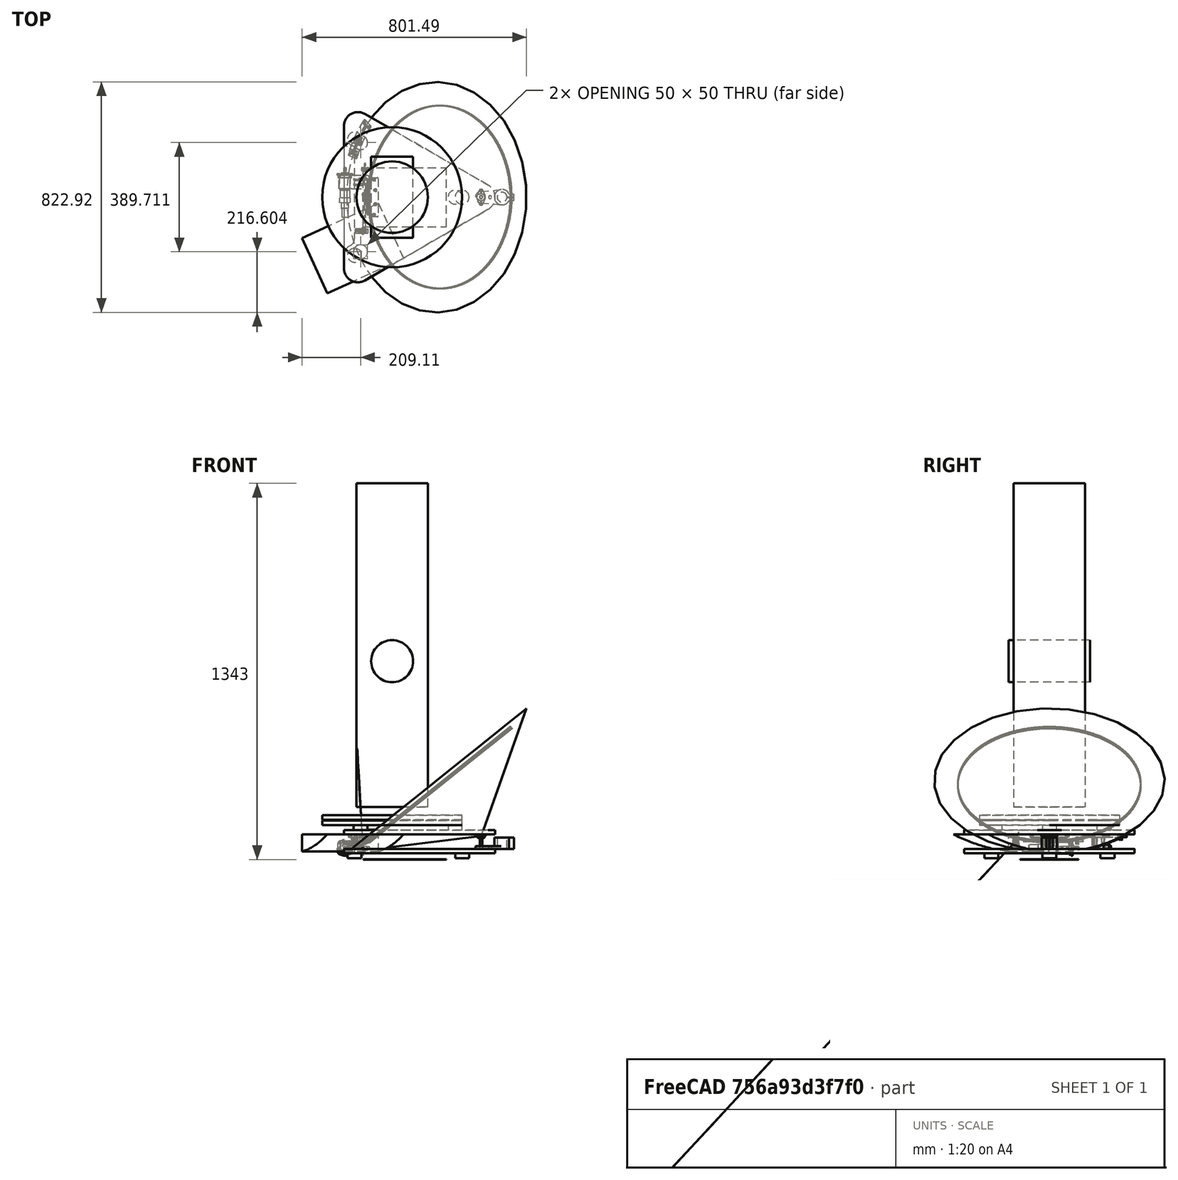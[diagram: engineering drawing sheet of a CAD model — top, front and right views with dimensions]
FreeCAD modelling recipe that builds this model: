
FCSTD DOCUMENT  (FreeCAD 2022.111R30764 (Git))
Label: DobsonEQPlatformGearBearing
License: All rights reserved
LicenseURL: http://en.wikipedia.org/wiki/All_rights_reserved
objects: Sketcher::SketchExport×38, PartDesign::Pad×30, Sketcher::SketchObject×28, PartDesign::Fillet×20, PartDesign::SubShapeBinder×17, PartDesign::Pocket×15, PartDesign::Body×14, PartDesign::Chamfer×13, Part::SubShapeBinder×10, TechDraw::DrawViewDimension×8, PartDesign::Plane×7, PartDesign::ShapeBinder×6, Part::FeaturePython×4, Part::Mirroring×4, Part::Cylinder×3, PartDesign::Revolution×3, TechDraw::DrawProjGroup×3, TechDraw::DrawProjGroupItem×3, TechDraw::DrawSVGTemplate×2, Part::Box×2, +7 more types
note: 381 computed .brp shape members not serialized (recipe doc carries the construction recipe); baked Part::Feature solids carry a one-line shape summary decoded from their .brp

FEATURE [Part::Cylinder] Cylinder  label="Newton"
  Angle = 360
  AttacherType = Attacher::AttachEngine3D
  FirstAngle = 0
  Height = 1155
  Placement = pos=(0,0,83) rot=(0,0,1;0rad)
  Radius = 127.5
  SecondAngle = 0
  TreeRank = 0
FEATURE [Part::Cylinder] Cylinder003
  Angle = 360
  AttacherType = Attacher::AttachEngine3D
  FirstAngle = 0
  Height = 290
  Placement = pos=(0,-145,603) rot=(-1,0,0;1.5708rad)
  Radius = 75
  SecondAngle = 0
  TreeRank = 0
FEATURE [Spreadsheet::Sheet] Spreadsheet  label="measures"
  PythonMode = false
  ShowCells = 0
  TreeRank = 0
  cells = A1=Foot of Elipse; D1=Newton; A2=Drill sIze; B2(FootDrillSize)=6.2; D2=Height; E2=1155; A3=Nut size radius; B3(elipsefeednutsizeradius)=11.25; D3=Center of Gravitiy; E3(CoG)==315 + 60; A4=Nut pcket size; B4(elipsefeednutpocket)=4.8; A5=Foot size; B5(elipsefootSize)=35; D5=Radius; E5=127.5; A6=Foot thickness; B6(elipsefootthickness)=10; D6=Over ground; E6=83; A7=Roundness; B7(elipsefootroundness)=4; A9=Elipse; D9=MidPart over ground; E9=603; A10=Elipse position angle; B10(ElipsePositionAngle)=36; D10=Midpart radius ; E10=75; A11=Elipse max deg; B11(ElipseMaxDeg)=17.5; D11=Midpart height; E11=290; A12=Elipse tickness; B12(ElipseThickness)=7.2; A13=Distance Center; B13(ElipseDistanceCenterP)=480; A14=Stopper max deg; B14(elipsestoppermaxdeg)=1; A15=StopperHeight; B15(ElipseStopperHeight)=10; A16=Screw head diameter; B16(elipsescrewheaddia)=10; A17=Screw hole diameter; B17(elipsescrewholedia)=6; A18=Screw distance; B18(elipsescrewdistance)=10; A20=Rockerbox; A21=Diameter; B21(RockerboxDiameter)=500; A22=FeedDiameter; B22(RockerboxFeedDiameter)=50; A23=Teflonpad gap; B23(teflonpadgap)=3; A24=Thickness; B24(Rockerboxthickness)=16; A25=MinFeedHight; B25(RockerboxMinFeedHight)=18; A26=Cone; A27=Midpoint to south bearing; B27(MidpointToSouthBearing)=300; A28=Pol Angle deg; B28(PolarisAngle)=51.3; A29=Cone Angle; B29(ConeAngle)=58.3; A30=South Bearing height; B30(southbearingheigt)=6.5; C30=for mid point of bearing; A31=South Bearing axis diameter; B31(southbearingaxisdia)=10; A32=Plattform; A33=Thickness; B33(plattformthickness)=15; A34=Platform gap; B34(platformgap)=52; A35=Midpoint to north end top; B35(platformmidpointnorth)=172; A36=Midpoint to north end bottom; B36(platformmidpointnorthbottom)=360; A37=Roller X from midpoint; B37(rollerXmidpoint)=130; A38=Roller Y from midpoint; B38(rollerYmidpoint)=190
FEATURE [Sketcher::SketchObject] Sketch  label="MasterXZ"
  FullyConstrained = true
  MapMode = 5
  Placement = pos=(0,0,0) rot=(1,0,0;1.5708rad)
  Support = -> [XZ_Plane]
  TreeRank = 11
  expr: Constraints[12] = <<measures>>.CoG
  expr: Constraints[3] = <<measures>>.PolarisAngle
  expr: Constraints[4] = <<measures>>.ConeAngle
  expr: Constraints[5] = -<<measures>>.plattformthickness - <<measures>>.southbearingheigt
  expr: Constraints[8] = <<measures>>.ElipseDistanceCenterP
  sketch-geometry (5):
    g0: LineSegment StartX=317.656 StartY=-21.5 StartZ=0 EndX=158.769 EndY=176.823 EndZ=0
    g1: LineSegment StartX=158.769 StartY=176.823 StartZ=0 EndX=-162.344 EndY=-80.4366 EndZ=0
    g2: LineSegment StartX=-162.344 StartY=-80.4366 StartZ=0 EndX=317.656 EndY=-21.5 EndZ=0
    g3: LineSegment [constr] StartX=158.769 StartY=176.823 StartZ=0 EndX=-245.062 EndY=680.887 EndZ=0
    g4: LineSegment [constr] StartX=0 StartY=0 StartZ=0 EndX=0 EndY=375 EndZ=0
  constraints (14):
    c: Coincident(g0,g1)
    c: Coincident(g1,g2)
    c: Coincident(g2,g0)
    c: Angle(g0,g-1) = 0.895354
    c: Angle(g0,g2) = 1.01753
    c: DistanceY(g0) = -21.5
    c: Perpendicular(g0,g1)
    c: Tangent(g3,g0) = -1.5708
    c: DistanceX(g1,g0) = 480
    c: Distance(g3,g0) = 900
    c: Coincident(g4,g-1)
    c: Vertical(g4)
    c: DistanceY(g4,g4) = 375
    c: PointOnObject(g4,g3)
FEATURE [Sketcher::SketchObject] Sketch001  label="MasterXY"
  ExternalGeometry = -> [Sketch]
  FullyConstrained = true
  MapMode = 5
  Support = -> [XY_Plane]
  TreeRank = 12
  expr: Constraints[35] = <<measures>>.southbearingaxisdia
  expr: Constraints[62] = <<measures>>.RockerboxDiameter - <<measures>>.RockerboxFeedDiameter
  expr: Constraints[63] = <<measures>>.RockerboxDiameter
  expr: Constraints[72] = <<measures>>.RockerboxFeedDiameter
  sketch-geometry (31):
    g0: Circle CenterX=317.656 CenterY=4.1e-15 CenterZ=0 NormalX=0 NormalY=0 NormalZ=1 AngleXU=0 Radius=5
    g1: Circle CenterX=317.656 CenterY=0 CenterZ=0 NormalX=0 NormalY=0 NormalZ=1 AngleXU=0 Radius=10.95
    g2: LineSegment [constr] StartX=330.656 StartY=13 StartZ=0 EndX=304.656 EndY=13 EndZ=0
    g3: LineSegment [constr] StartX=304.656 StartY=13 StartZ=0 EndX=304.656 EndY=-13 EndZ=0
    g4: LineSegment [constr] StartX=304.656 StartY=-13 StartZ=0 EndX=304.656 EndY=13 EndZ=0
    g5: LineSegment [constr] StartX=304.656 StartY=13 StartZ=0 EndX=330.656 EndY=13 EndZ=0
    g6: Circle [constr] CenterX=317.656 CenterY=4.8e-15 CenterZ=0 NormalX=0 NormalY=0 NormalZ=1 AngleXU=0 Radius=18.3848
    g7: Circle CenterX=304.656 CenterY=-13 CenterZ=0 NormalX=0 NormalY=0 NormalZ=1 AngleXU=0 Radius=2.65
    g8: Circle CenterX=304.656 CenterY=13 CenterZ=0 NormalX=0 NormalY=0 NormalZ=1 AngleXU=0 Radius=2.65
    g9: Circle CenterX=304.656 CenterY=13 CenterZ=0 NormalX=0 NormalY=0 NormalZ=1 AngleXU=0 Radius=2.65
    g10: Circle CenterX=330.656 CenterY=13 CenterZ=0 NormalX=0 NormalY=0 NormalZ=1 AngleXU=0 Radius=2.65
    g11: LineSegment StartX=298.656 StartY=-13 StartZ=0 EndX=298.656 EndY=13 EndZ=0
    g12: ArcOfCircle CenterX=304.656 CenterY=13 CenterZ=0 NormalX=0 NormalY=0 NormalZ=1 AngleXU=0 Radius=6 StartAngle=1.5708 EndAngle=3.14159
    g13: LineSegment StartX=304.656 StartY=19 StartZ=0 EndX=330.656 EndY=19 EndZ=0
    g14: ArcOfCircle CenterX=330.656 CenterY=13 CenterZ=0 NormalX=0 NormalY=0 NormalZ=1 AngleXU=0 Radius=6 StartAngle=2e-16 EndAngle=1.5708
    g15: LineSegment StartX=336.656 StartY=13 StartZ=0 EndX=336.656 EndY=-13 EndZ=0
    g16: ArcOfCircle CenterX=330.656 CenterY=-13 CenterZ=0 NormalX=0 NormalY=0 NormalZ=1 AngleXU=0 Radius=6 StartAngle=4.71239 EndAngle=6.28319
    g17: LineSegment StartX=330.656 StartY=-19 StartZ=0 EndX=304.656 EndY=-19 EndZ=0
    g18: ArcOfCircle CenterX=304.656 CenterY=-13 CenterZ=0 NormalX=0 NormalY=0 NormalZ=1 AngleXU=0 Radius=6 StartAngle=3.14159 EndAngle=4.71239
    g19: LineSegment [constr] StartX=330.656 StartY=13 StartZ=0 EndX=330.656 EndY=-13 EndZ=0
    g20: LineSegment [constr] StartX=330.656 StartY=-13 StartZ=0 EndX=304.656 EndY=-13 EndZ=0
    g21: Circle CenterX=330.656 CenterY=-13 CenterZ=0 NormalX=0 NormalY=0 NormalZ=1 AngleXU=0 Radius=2.65
    g22: Circle CenterX=0 CenterY=0 CenterZ=0 NormalX=0 NormalY=0 NormalZ=1 AngleXU=0 Radius=250
    g23: LineSegment StartX=-112.5 StartY=194.856 StartZ=0 EndX=-112.5 EndY=-194.856 EndZ=0
    g24: LineSegment StartX=-112.5 StartY=-194.856 StartZ=0 EndX=225 EndY=0 EndZ=0
    g25: LineSegment StartX=225 StartY=0 StartZ=0 EndX=-112.5 EndY=194.856 EndZ=0
    g26: Circle [constr] CenterX=0 CenterY=0 CenterZ=0 NormalX=0 NormalY=0 NormalZ=1 AngleXU=0 Radius=225
    g27: Circle CenterX=-112.5 CenterY=194.856 CenterZ=0 NormalX=0 NormalY=0 NormalZ=1 AngleXU=0 Radius=25
    g28: Circle CenterX=-112.5 CenterY=-194.856 CenterZ=0 NormalX=0 NormalY=0 NormalZ=1 AngleXU=0 Radius=7.1e-15
    g29: Circle CenterX=-112.5 CenterY=-194.856 CenterZ=0 NormalX=0 NormalY=0 NormalZ=1 AngleXU=0 Radius=25
    g30: Circle CenterX=225 CenterY=0 CenterZ=0 NormalX=0 NormalY=0 NormalZ=1 AngleXU=0 Radius=25
  constraints (73):
    c: Coincident(g0,g-3)
    c: Coincident(g1,g-3)
    c: Coincident(g2,g3)
    c: Coincident(g3,g4)
    c: Coincident(g4,g5)
    c: Coincident(g5,g2)
    c: Equal(g2,g3)
    c: Equal(g2,g4)
    c: Equal(g2,g5)
    c: PointOnObject(g2,g6)
    c: PointOnObject(g3,g6)
    c: PointOnObject(g5,g6)
    c: Coincident(g6,g-3)
    c: Coincident(g7,g3)
    c: Coincident(g8,g2)
    c: Coincident(g9,g4)
    c: Coincident(g10,g2)
    c: Tangent(g11,g12) = 1.5708
    c: Tangent(g12,g13) = 1.5708
    c: Tangent(g13,g14) = 1.5708
    c: Tangent(g14,g15) = 1.5708
    c: Tangent(g15,g16) = 1.5708
    c: Tangent(g16,g17) = 1.5708
    c: Tangent(g17,g18) = 1.5708
    c: Equal(g17,g13)
    c: Equal(g15,g11)
    c: Radius(g18) = 6
    c: Equal(g18,g16)
    c: Equal(g18,g12)
    c: Equal(g18,g14)
    c: Tangent(g11,g18) = 1.5708
    c: Equal(g7,g8)
    c: Equal(g8,g9)
    c: Equal(g9,g10)
    c: Diameter(g7) = 5.3
    c: Diameter(g0) = 10
    c: Diameter(g1) = 21.9
    c: Equal(g11,g17)
    c: Symmetric(g14,g15,g-1)
    c: Horizontal(g13)
    c: DistanceY(g16,g13) = 38
    c: DistanceY(g7,g8) = 26
    c: Vertical(g3)
    c: Horizontal(g2)
    c: Coincident(g19,g14)
    c: PointOnObject(g19,g6)
    c: Vertical(g19)
    c: Coincident(g20,g19)
    c: Coincident(g20,g7)
    c: Horizontal(g20)
    c: Coincident(g21,g16)
    c: Equal(g21,g10)
    c: Coincident(g23,g24)
    c: Coincident(g24,g25)
    c: Coincident(g25,g23)
    c: Equal(g23,g24)
    c: Equal(g23,g25)
    c: PointOnObject(g23,g26)
    c: PointOnObject(g24,g26)
    c: PointOnObject(g25,g26)
    c: Coincident(g26,g22)
    c: Vertical(g23)
    c: Diameter(g26) = 450
    c: Diameter(g22) = 500
    c: Coincident(g22,g-1)
    c: Coincident(g27,g23)
    c: Coincident(g28,g23)
    c: Tangent(g28,g26)
    c: Coincident(g29,g23)
    c: Coincident(g30,g24)
    c: Equal(g30,g27)
    c: Equal(g27,g29)
    c: Diameter(g29) = 50
FEATURE [PartDesign::ShapeBinder] ShapeBinder
  Support = -> [Sketch]
  TraceSupport = false
  TreeRank = 24
FEATURE [Part::SubShapeBinder] Import  label="Import(MasterXZ)"
  BindCopyOnChange = 0
  BindMode = 0
  ClaimChildren = false
  Context = -> Body001 [Import.]
  FillStyle = 0
  Fuse = false
  MakeFace = false
  PartialLoad = false
  Relative = true
  Support = -> [Body[Sketch.]]
  TreeRank = 26
  _Version = 8
FEATURE [Sketcher::SketchObject] Sketch002  label="ConeSkatch"
  ExternalGeometry = -> [ShapeBinder,Import]
  FullyConstrained = true
  MapMode = 5
  Placement = pos=(0,0,0) rot=(1,0,0;1.5708rad)
  Support = -> [XZ_Plane001]
  TreeRank = 27
  sketch-geometry (3):
    g0: LineSegment StartX=317.656 StartY=-21.5 StartZ=0 EndX=158.769 EndY=176.823 EndZ=0
    g1: LineSegment StartX=158.769 StartY=176.823 StartZ=0 EndX=-162.344 EndY=-80.4366 EndZ=0
    g2: LineSegment StartX=-162.344 StartY=-80.4366 StartZ=0 EndX=317.656 EndY=-21.5 EndZ=0
  constraints (6):
    c: Coincident(g0,g-3)
    c: Coincident(g0,g-4)
    c: Coincident(g0,g1)
    c: Coincident(g1,g-5)
    c: Coincident(g1,g2)
    c: Coincident(g2,g0)
FEATURE [PartDesign::Revolution] Revolution
  AddSubType = 0
  Angle = 360
  Axis = (-0.625243,-2e-16,0.78043)
  Base = (317.656,4.8e-15,-21.5)
  ClaimChildren = false
  Fit = 0
  FitJoin = 0
  InnerFit = 0
  InnerFitJoin = 0
  NewSolid = false
  Placement = pos=(0,0,0) rot=(1,0,0;1.5708rad)
  Profile = -> Sketch002
  ReferenceAxis = -> ShapeBinder [Edge2]
  Suppress = false
  TreeRank = 28
  _ProfileBasedVersion = 1
FEATURE [PartDesign::Body] Body001  label="Cone"
  AutoGroupSolids = false
  ExportMode = 0
  Group = -> [ShapeBinder,Import,Sketch002,Revolution]
  Origin = -> Origin001
  Tip = -> Revolution
  TreeRank = 23
  _ExportChildren = -> [ShapeBinder,Import,Revolution]
  _GroupVersion = 1
FEATURE [PartDesign::ShapeBinder] ShapeBinder001
  Support = -> [Sketch001]
  TraceSupport = false
  TreeRank = 39
FEATURE [Part::SubShapeBinder] Import001  label="Import001(MasterXY)"
  BindCopyOnChange = 0
  BindMode = 0
  ClaimChildren = false
  Context = -> Body002 [Import001.]
  FillStyle = 0
  Fuse = false
  MakeFace = false
  PartialLoad = false
  Relative = true
  Support = -> [Body[Sketch001.]]
  TreeRank = 41
  _Version = 8
FEATURE [Sketcher::SketchObject] Sketch004  label="PlatformTop"
  ExternalGeometry = -> [Sketch001]
  FullyConstrained = true
  MapMode = 5
  Support = -> [XY_Plane]
  TreeRank = 53
  expr: Constraints[15] = <<measures>>.platformmidpointnorth
  sketch-geometry (7):
    g0: LineSegment StartX=342.656 StartY=43.3013 StartZ=0 EndX=-97 EndY=297.137 EndZ=0
    g1: ArcOfCircle CenterX=-122 CenterY=253.836 CenterZ=0 NormalX=0 NormalY=0 NormalZ=1 AngleXU=0 Radius=50 StartAngle=1.0472 EndAngle=3.14159
    g2: LineSegment StartX=-172 StartY=253.836 StartZ=0 EndX=-172 EndY=-253.836 EndZ=0
    g3: ArcOfCircle CenterX=-122 CenterY=-253.836 CenterZ=0 NormalX=0 NormalY=0 NormalZ=1 AngleXU=0 Radius=50 StartAngle=3.14159 EndAngle=5.23599
    g4: LineSegment StartX=-97 StartY=-297.137 StartZ=0 EndX=342.656 EndY=-43.3013 EndZ=0
    g5: ArcOfCircle CenterX=317.656 CenterY=2e-16 CenterZ=0 NormalX=0 NormalY=0 NormalZ=1 AngleXU=0 Radius=50 StartAngle=5.23599 EndAngle=7.33038
    g6: LineSegment [constr] StartX=-172 StartY=0 StartZ=0 EndX=367.656 EndY=0 EndZ=0
  constraints (17):
    c: Tangent(g0,g1) = -1.5708
    c: Tangent(g1,g2) = -1.5708
    c: Tangent(g2,g3) = -1.5708
    c: Tangent(g3,g4) = -1.5708
    c: Tangent(g4,g5) = -1.5708
    c: Tangent(g5,g0) = -1.5708
    c: Symmetric(g0,g4,g-1)
    c: Symmetric(g1,g2,g-1)
    c: Radius(g5) = 50
    c: Radius(g1) = 50
    c: Equal(g4,g2)
    c: PointOnObject(g6,g5)
    c: Horizontal(g6)
    c: PointOnObject(g6,g2)
    c: DistanceX(g-3,g6) = 50
    c: DistanceX(g6,g-1) = 172
    c: PointOnObject(g6,g-1)
FEATURE [PartDesign::Body] Body  label="MasterBody"
  AutoGroupSolids = false
  ExportMode = 0
  Group = -> [Sketch,Sketch001,Sketch004]
  Origin = -> Origin
  TreeRank = 22
  _ExportChildren = -> [Sketch,Sketch001,Sketch004]
  _GroupVersion = 1
FEATURE [PartDesign::ShapeBinder] ShapeBinder002
  Support = -> [Sketch004,Sketch001]
  TraceSupport = false
  TreeRank = 100
FEATURE [Part::SubShapeBinder] Import002  label="Import002(PlatformTop)"
  BindCopyOnChange = 0
  BindMode = 0
  ClaimChildren = false
  Context = -> Body003 [Import002.]
  FillStyle = 0
  Fuse = false
  MakeFace = false
  PartialLoad = false
  Relative = true
  Support = -> [Sketch004]
  TreeRank = 102
  _Version = 8
FEATURE [Sketcher::SketchObject] Sketch005  label="plattop"
  ExternalGeometry = -> [Import002]
  FullyConstrained = true
  MapMode = 5
  Support = -> [XY_Plane003]
  TreeRank = 101
FEATURE [PartDesign::Pad] Pad006
  AddSubType = 0
  CheckUpToFaceLimits = true
  ClaimChildren = false
  Direction = (0,0,1)
  Fit = 0
  FitJoin = 0
  InnerFit = 0
  InnerFitJoin = 0
  InnerTaperAngle = 0
  InnerTaperAngleRev = 0
  Length = 15
  Length2 = 100
  Linearize = true
  NewSolid = false
  Profile = -> Sketch005
  Reversed = true
  Suppress = false
  TreeRank = 103
  Type = 0
  _ProfileBasedVersion = 1
  expr: Length = <<measures>>.plattformthickness
FEATURE [Part::SubShapeBinder] Import003  label="Import003(MasterXY)"
  BindCopyOnChange = 0
  BindMode = 0
  ClaimChildren = false
  Context = -> Body003 [Import003.]
  FillStyle = 0
  Fuse = false
  MakeFace = false
  PartialLoad = false
  Relative = true
  Support = -> [Sketch001]
  TreeRank = 105
  _Version = 8
FEATURE [PartDesign::ShapeBinder] ShapeBinder003
  Support = -> [Sketch004,Sketch001]
  TraceSupport = false
  TreeRank = 118
FEATURE [PartDesign::ShapeBinder] ShapeBinder004
  Support = -> [Sketch001]
  TraceSupport = false
  TreeRank = 120
FEATURE [PartDesign::SubShapeBinder] Binder001  label="Binder001(Pad037)"
  BindCopyOnChange = 0
  BindMode = 0
  ClaimChildren = false
  Context = -> Body004 [Binder001.]
  FillStyle = 0
  Fuse = false
  MakeFace = true
  PartialLoad = false
  Relative = true
  Support = -> [Pad037[Face41]]
  TreeRank = 176
  _Version = 8
FEATURE [PartDesign::SubShapeBinder] Binder  label="Binder(Revolution)"
  BindCopyOnChange = 0
  BindMode = 0
  ClaimChildren = false
  Context = -> Body008 [Binder.]
  FillStyle = 0
  Fuse = false
  MakeFace = true
  PartialLoad = false
  Relative = true
  Support = -> [Body001[Revolution.Edge1]]
  TreeRank = 290
  _Version = 8
FEATURE [PartDesign::SubShapeBinder] Binder004  label="Binder004(Fillet009)"
  BindCopyOnChange = 0
  BindMode = 0
  ClaimChildren = false
  Context = -> Body008 [Binder004.]
  FillStyle = 0
  Fuse = false
  MakeFace = true
  PartialLoad = false
  Relative = true
  Support = -> [Body003[Fillet009.Face33]]
  TreeRank = 318
  _Version = 8
FEATURE [Part::SubShapeBinder] Import009  label="Import009(Sketch011)"
  BindCopyOnChange = 0
  BindMode = 0
  ClaimChildren = false
  Context = -> Body006 [Import009.]
  FillStyle = 0
  Fuse = false
  MakeFace = false
  PartialLoad = false
  Relative = true
  Support = -> [Sketch011]
  TreeRank = 323
  _Version = 8
FEATURE [Part::SubShapeBinder] Import011  label="Import011(Fillet006)"
  BindCopyOnChange = 0
  BindMode = 0
  ClaimChildren = false
  Context = -> Body009 [Import011.]
  FillStyle = 0
  Fuse = false
  MakeFace = false
  PartialLoad = false
  Relative = true
  Support = -> [Body006[Fillet006.]]
  TreeRank = 357
  _Version = 8
FEATURE [PartDesign::Plane] DatumPlane002
  Length = 440.135
  MapMode = 5
  MinimumLength = 10
  MinimumWidth = 10
  Placement = pos=(-185.022,-83.9977,0) rot=(0.739203,-0.476224,-0.476224;1.86848rad)
  ResizeMode = 0
  Support = -> [Import011]
  TreeRank = 356
  Width = 75.6692
FEATURE [PartDesign::SubShapeBinder] Binder006  label="Binder006(Revolution)"
  BindCopyOnChange = 0
  BindMode = 0
  ClaimChildren = false
  Context = -> Body009 [Binder006.]
  FillStyle = 0
  Fuse = false
  MakeFace = true
  PartialLoad = false
  Relative = true
  Support = -> [Body001[Revolution.Edge1]]
  TreeRank = 359
  _Version = 8
FEATURE [Part::SubShapeBinder] Import012  label="Import012(MasterXZ)"
  BindCopyOnChange = 0
  BindMode = 0
  ClaimChildren = false
  Context = -> Body009 [Import012.]
  FillStyle = 0
  Fuse = false
  MakeFace = false
  PartialLoad = false
  Relative = true
  Support = -> [Body[Sketch.]]
  TreeRank = 360
  _Version = 8
FEATURE [Sketcher::SketchObject] Sketch013
  ExternalGeometry = -> [Binder006,Import012]
  FullyConstrained = true
  MapMode = 5
  Placement = pos=(-185.022,-83.9977,0) rot=(0.739203,-0.476224,-0.476224;1.86848rad)
  Support = -> [DatumPlane002]
  TreeRank = 358
  expr: Constraints[13] = <<measures>>.plattformthickness
  sketch-geometry (7):
    g0: ArcOfEllipse CenterX=65.6324 CenterY=176.823 CenterZ=0 NormalX=0 NormalY=0 NormalZ=1 MajorRadius=411.456 MinorRadius=234.25 AngleXU=0.319813 StartAngle=4.36015 EndAngle=4.91482
    g1: LineSegment [constr] StartX=456.226 StartY=306.181 StartZ=0 EndX=-324.961 EndY=47.4662 EndZ=0
    g2: LineSegment [constr] StartX=-8.01316 StartY=399.196 StartZ=0 EndX=139.278 EndY=-45.5488 EndZ=0
    g3: GeomPoint [constr] X=386.745 Y=283.17 Z=0
    g4: GeomPoint [constr] X=-255.481 Y=70.4767 Z=0
    g5: LineSegment StartX=-5.68e-14 StartY=-76.5242 StartZ=0 EndX=0 EndY=-15 EndZ=0
    g6: LineSegment StartX=0 StartY=-15 StartZ=0 EndX=216.305 EndY=-15 EndZ=0
  constraints (11):
    c: InternalAlignment(g1-g4 -> g0) x4
    c: Coincident(g0,g-4)
    c: PointOnObject(g0,g-2)
    c: Coincident(g5,g0)
    c: Coincident(g6,g0)
    c: PointOnObject(g2,g-3)
    c: Coincident(g5,g6)
    c: PointOnObject(g5,g-2)
    c: Tangent(g0,g-3) = -1.5708
    c: Horizontal(g6)
    c: DistanceY(g5,g-1) = 15
FEATURE [PartDesign::Pad] Pad031
  AddSubType = 0
  AlongSketchNormal = false
  CheckUpToFaceLimits = true
  ClaimChildren = false
  Direction = (-0.910558,-0.413382,0)
  Fit = 0
  FitJoin = 0
  InnerFit = 0
  InnerFitJoin = 0
  InnerTaperAngle = 0
  InnerTaperAngleRev = 0
  Length = 300
  Length2 = 100
  Linearize = true
  Midplane = true
  NewSolid = false
  Placement = pos=(-185.022,-83.9977,0) rot=(0.739203,-0.476224,-0.476224;1.86848rad)
  Profile = -> Sketch013
  Refine = true
  Suppress = false
  TreeRank = 361
  Type = 0
  _ProfileBasedVersion = 1
FEATURE [PartDesign::Body] Body009  label="CutterElipse"
  AutoGroupSolids = false
  ExportMode = 0
  Group = -> [DatumPlane002,Import011,Sketch013,Binder006,Import012,Pad031]
  Origin = -> Origin009
  Tip = -> Pad031
  TreeRank = 355
  _ExportChildren = -> [DatumPlane002,Import011,Binder006,Import012,Pad031]
  _GroupVersion = 1
FEATURE [PartDesign::SubShapeBinder] Binder007  label="Binder007(Pad031)"
  BindCopyOnChange = 0
  BindMode = 0
  ClaimChildren = false
  Context = -> Body008 [Binder007.]
  FillStyle = 0
  Fuse = false
  MakeFace = true
  PartialLoad = false
  Relative = true
  Support = -> [Body009[Pad031.]]
  TreeRank = 362
  _Version = 8
FEATURE [PartDesign::SubShapeBinder] Reference  label="Reference(Pad026)"
  BindCopyOnChange = 0
  BindMode = 0
  ClaimChildren = false
  Context = -> Body008 [Reference.]
  FillStyle = 0
  Fuse = false
  MakeFace = true
  PartialLoad = false
  Relative = true
  Support = -> [Pad026]
  TreeRank = 364
  _Version = 8
FEATURE [PartDesign::SubShapeBinder] Reference001  label="Reference001(*Pad031)"
  BindCopyOnChange = 0
  BindMode = 0
  ClaimChildren = false
  Context = -> Body008 [Reference001.]
  FillStyle = 0
  Fuse = false
  MakeFace = true
  PartialLoad = false
  Relative = true
  Support = -> [Binder007]
  TreeRank = 365
  _Version = 8
FEATURE [PartDesign::SubShapeBinder] Binder008  label="Binder008(Chamfer003)"
  BindCopyOnChange = 0
  BindMode = 0
  ClaimChildren = false
  Context = -> Body008 [Binder008.]
  FillStyle = 0
  Fuse = false
  MakeFace = true
  PartialLoad = false
  Relative = true
  Support = -> [Chamfer003[Edge12]]
  TreeRank = 380
  _Version = 8
FEATURE [TechDraw::DrawSVGTemplate] Template
  EditableTexts = AUTHOR_NAME=Sebastian Förster; DN=DN; DRAWING_TITLE=EQ Plattform; FC-DATE=28/01/2022; FC-REV=REV A; FC-SC=1:1; FC-SH=1 / 1; FC-SI=A0; FreeCAD_DRAWING=Drawing for wood cutting and drilling; PN=PN
  Height = 841
  Orientation = 1
  TreeRank = 382
  Width = 1189
FEATURE [PartDesign::SubShapeBinder] Binder009  label="Binder009(Pad025)"
  BindCopyOnChange = 0
  BindMode = 0
  ClaimChildren = false
  Context = -> Body006 [Binder009.]
  FillStyle = 0
  Fuse = false
  MakeFace = true
  PartialLoad = false
  Relative = true
  Support = -> [Pad025[Face4]]
  TreeRank = 389
  _Version = 8
FEATURE [PartDesign::Plane] DatumPlane
  AttachmentOffset = pos=(0,0,10) rot=(0,0,1;0rad)
  Length = 131.581
  MapMode = 5
  MinimumLength = 10
  MinimumWidth = 10
  Placement = pos=(0,0,-57) rot=(0,0,1;0rad)
  ResizeMode = 0
  Support = -> [Binder009]
  TreeRank = 216
  Width = 219.924
FEATURE [Part::SubShapeBinder] Import004  label="Import004(Pad006)"
  BindCopyOnChange = 0
  BindMode = 0
  ClaimChildren = false
  Context = -> Body004 [Import004.]
  FillStyle = 0
  Fuse = false
  MakeFace = false
  PartialLoad = false
  Relative = true
  Support = -> [Body003[Pad006.]]
  TreeRank = 391
  _Version = 8
FEATURE [Part::Box] Box  label="A4Ref"
  AttacherType = Attacher::AttachEngine3D
  Height = 1
  Length = 297
  Placement = pos=(-103,-105,0) rot=(0,0,1;0rad)
  TreeRank = 400
  Width = 210
  expr: Placement.Base.y = -210 / 2
FEATURE [Part::Box] Box001  label="A4Ref2"
  AttacherType = Attacher::AttachEngine3D
  Height = 1
  Length = 297
  Placement = pos=(-103,-105,-105) rot=(0,0,1;0rad)
  TreeRank = 413
  Width = 210
  expr: Placement.Base.y = -210 / 2
FEATURE [TechDraw::DrawSVGTemplate] Template001
  EditableTexts = AUTHOR_NAME=AUTHOR NAME; DN=DN; DRAWING_TITLE=DRAWING TITLE; FC-DATE=DD/MM/YYYY; FC-REV=REV A; FC-SC=SCALE; FC-SH=X / Y; FC-SI=A0; FreeCAD_DRAWING=FreeCAD DRAWING; PN=PN
  Height = 841
  Orientation = 1
  TreeRank = 415
  Width = 1189
FEATURE [TechDraw::DrawViewAnnotation] Annotation
  Font = osifont
  LineSpace = 80
  LockPosition = false
  MaxWidth = -1
  Rotation = 0
  ScaleType = 0
  Text = M10
  TextSize = 5
  TextStyle = 0
  TreeRank = 441
  X = 727.492
  Y = 684.045
FEATURE [Part::SubShapeBinder] Import013  label="Import013(Revolution)"
  BindCopyOnChange = 0
  BindMode = 0
  ClaimChildren = false
  Context = -> Body010 [Import013.]
  FillStyle = 0
  Fuse = false
  MakeFace = false
  PartialLoad = false
  Relative = true
  Support = -> [Body001[Revolution.]]
  TreeRank = 472
  _Version = 8
FEATURE [PartDesign::Plane] DatumPlane003
  AttachmentOffset = pos=(65,0,-27) rot=(0,0,1;0rad)
  Length = 162.579
  MapMode = 5
  MinimumLength = 10
  MinimumWidth = 10
  Placement = pos=(43.3945,0,49.7944) rot=(0,-1,0;0.675442rad)
  ResizeMode = 0
  Support = -> [Import013]
  TreeRank = 471
  Width = 140
FEATURE [PartDesign::SubShapeBinder] Binder010  label="Binder010(Pad037)"
  BindCopyOnChange = 0
  BindMode = 0
  ClaimChildren = false
  Context = -> Body010 [Binder010.]
  FillStyle = 0
  Fuse = false
  MakeFace = true
  PartialLoad = false
  Relative = true
  Support = -> [Body003[Pad037.Face33]]
  TreeRank = 475
  _Version = 8
FEATURE [Sketcher::SketchObject] Sketch018  label="GearCut"
  ExternalGeometry = -> [Binder010]
  FullyConstrained = true
  MapMode = 5
  Placement = pos=(0,0,0) rot=(0.57735,0.57735,0.57735;2.0944rad)
  Support = -> [YZ_Plane010]
  TreeRank = 477
  expr: Constraints[9] = <<measures>>.platformgap
  sketch-geometry (4):
    g0: LineSegment StartX=75 StartY=-15 StartZ=0 EndX=-75 EndY=-15 EndZ=0
    g1: LineSegment StartX=-75 StartY=-15 StartZ=0 EndX=-75 EndY=-67 EndZ=0
    g2: LineSegment StartX=-75 StartY=-67 StartZ=0 EndX=75 EndY=-67 EndZ=0
    g3: LineSegment StartX=75 StartY=-67 StartZ=0 EndX=75 EndY=-15 EndZ=0
  constraints (11):
    c: Coincident(g0,g1)
    c: Coincident(g1,g2)
    c: Coincident(g2,g3)
    c: Coincident(g3,g0)
    c: Horizontal(g2)
    c: Vertical(g1)
    c: Vertical(g3)
    c: Symmetric(g0,g0,g-2)
    c: PointOnObject(g0,g-3)
    c: DistanceY(g1,g1) = 52
    c: DistanceX(g2,g2) = 150
FEATURE [Part::SubShapeBinder] Import014  label="Import014(MasterXZ)"
  BindCopyOnChange = 0
  BindMode = 0
  ClaimChildren = false
  Context = -> Body010 [Import014.]
  FillStyle = 0
  Fuse = false
  MakeFace = false
  PartialLoad = false
  Relative = true
  Support = -> [Body[Sketch.]]
  TreeRank = 479
  _Version = 8
FEATURE [Part::FeaturePython] involutegear  # WARN: FeaturePython — macro-defined, semantics opaque (R4)
  AttacherType = Attacher::AttachEngine3D
  Placement = pos=(173.632,0,158.326) rot=(0,-1,0;0.675442rad)
  TreeRank = 488
  backlash = 0
  beta = 0
  clearance = 0.25
  da = 654.4
  df = 650.8
  double_helix = false
  dw = 652.8
  head = 0
  height = 10
  module = 0.8
  numpoints = 6
  pressure_angle = 20
  properties_from_tool = false
  reversed_backlash = false
  shift = 0
  simple = false
  teeth = 816
  transverse_pitch = 2.51327
  undercut = false
  version = 0.0.3
FEATURE [Sketcher::SketchObject] Sketch019
  FullyConstrained = true
  MapMode = 5
  Placement = pos=(0,0,0) rot=(0.57735,0.57735,0.57735;2.0944rad)
  Support = -> [YZ_Plane010]
  TreeRank = 490
FEATURE [PartDesign::SubShapeBinder] Binder011  label="Binder011(involutegear)"
  BindCopyOnChange = 0
  BindMode = 0
  ClaimChildren = false
  Context = -> Body010 [Binder011.]
  FillStyle = 0
  Fuse = false
  MakeFace = true
  PartialLoad = false
  Relative = true
  Support = -> [involutegear[Face3266]]
  TreeRank = 491
  _Version = 8
FEATURE [Sketcher::SketchObject] Sketch020
  ExternalGeometry = -> [Import014,Binder011]
  FullyConstrained = true
  MapMode = 5
  Placement = pos=(-15.6311,0,19.5108) rot=(0,-1,0;0.675442rad)
  Support = -> [Binder011]
  TreeRank = 492
  sketch-geometry (2):
    g0: LineSegment StartX=-84.6997 StartY=63.2197 StartZ=0 EndX=234.466 EndY=0 EndZ=0
    g1: LineSegment StartX=-84.6997 StartY=-63.2197 StartZ=0 EndX=234.466 EndY=0 EndZ=0
  constraints (4):
    c: Coincident(g0,g-210)
    c: Coincident(g1,g-170)
    c: Coincident(g0,g-68)
    c: Coincident(g1,g0)
FEATURE [PartDesign::Pad] Pad038
  AddSubType = 0
  AlongSketchNormal = false
  CheckUpToFaceLimits = true
  ClaimChildren = false
  Direction = (-0.625243,0,0.78043)
  Fit = 0
  FitJoin = 0
  InnerFit = 0
  InnerFitJoin = 0
  InnerTaperAngle = 0
  InnerTaperAngleRev = 0
  Length = 10
  Length2 = 100
  Linearize = true
  NewSolid = false
  Profile = -> Sketch020
  Refine = true
  Suppress = false
  TreeRank = 493
  Type = 0
  _ProfileBasedVersion = 1
FEATURE [PartDesign::Pocket] Pocket002
  AddSubType = 2
  BaseFeature = -> Pad038
  CheckUpToFaceLimits = true
  ClaimChildren = false
  Fit = 0
  FitJoin = 0
  InnerFit = 0
  InnerFitJoin = 0
  InnerTaperAngle = 0
  InnerTaperAngleRev = 0
  Length = 250
  Length2 = 100
  Linearize = true
  Midplane = true
  NewSolid = false
  Profile = -> Sketch018
  Refine = true
  Suppress = false
  TreeRank = 494
  Type = 0
  _ProfileBasedVersion = 1
  _Version = 1
FEATURE [PartDesign::SubShapeBinder] Binder012  label="Binder012(Pad025)"
  BindCopyOnChange = 0
  BindMode = 0
  ClaimChildren = false
  Context = -> Body011 [Binder012.]
  FillStyle = 0
  Fuse = false
  MakeFace = true
  PartialLoad = false
  Relative = true
  Support = -> [Body004[Pad025.Face4]]
  TreeRank = 515
  _Version = 8
FEATURE [Part::FeaturePython] wormgear  # WARN: FeaturePython — macro-defined, semantics opaque (R4)
  AttacherType = Attacher::AttachEngine3D
  Placement = pos=(-97,-14.5,-39) rot=(-1,0,0;1.5708rad)
  TreeRank = 553
  beta = 2.86241
  clearance = 0.25
  diameter = 16
  head = 0
  height = 30
  module = 0.8
  pressure_angle = 20
  reverse_pitch = false
  teeth = 1
  version = 0.0.3
FEATURE [Part::FeaturePython] timinggear  # WARN: FeaturePython — macro-defined, semantics opaque (R4)
  AttacherType = Attacher::AttachEngine3D
  Placement = pos=(-97,95,-38.5) rot=(-1,0,0;1.5708rad)
  TreeRank = 555
  h = 0.75
  height = 10
  offset = 0.4
  pitch = 2
  r0 = 0.555
  r1 = 1
  rs = 0.15
  teeth = 40
  type = 0
  u = 0.254
  version = 0.0.3
FEATURE [Part::Cylinder] Cylinder004  label="axel01"
  Angle = 360
  AttacherType = Attacher::AttachEngine3D
  FirstAngle = 0
  Height = 240
  Placement = pos=(-97,-120,-38.5) rot=(-1,0,0;1.5708rad)
  Radius = 3
  SecondAngle = 0
  TreeRank = 551
FEATURE [App::Part] Part  label="Axel"
  ExportMode = 1
  Group = -> [timinggear,wormgear,Cylinder004]
  Origin = -> Origin012
  TreeRank = 561
  _ExportChildren = -> [timinggear,wormgear,Cylinder004]
  _GroupVersion = 1
FEATURE [PartDesign::SubShapeBinder] Binder013  label="Binder013(Fillet020)"
  BindCopyOnChange = 0
  BindMode = 0
  ClaimChildren = false
  Context = -> Body012 [Binder013.]
  FillStyle = 0
  Fuse = false
  MakeFace = true
  PartialLoad = false
  Relative = true
  Support = -> [Body011[Fillet020.Face33]]
  TreeRank = 572
  _Version = 8
FEATURE [PartDesign::Plane] DatumPlane004  label="DatumPlanehole"
  AttachmentOffset = pos=(0,0,-5) rot=(0,0,1;0rad)
  Length = 10
  MapMode = 5
  MinimumLength = 10
  MinimumWidth = 10
  Placement = pos=(-3.69e-14,123,9.1e-15) rot=(0,0.707107,0.707107;3.14159rad)
  ResizeMode = 0
  Support = -> [Binder013]
  TreeRank = 579
  Width = 10
FEATURE [PartDesign::Plane] DatumPlane005  label="DatumPlanesupport"
  AttachmentOffset = pos=(0,0,-7.5) rot=(0,0,1;0rad)
  Length = 104.9
  MapMode = 5
  MinimumLength = 10
  MinimumWidth = 10
  Placement = pos=(-3.62e-14,120.5,8.6e-15) rot=(0,0.707107,0.707107;3.14159rad)
  ResizeMode = 0
  Support = -> [Binder013]
  TreeRank = 581
  Width = 45.5
FEATURE [PartDesign::SubShapeBinder] Binder014  label="Binder014(Pad025)"
  BindCopyOnChange = 0
  BindMode = 0
  ClaimChildren = false
  Context = -> Body013 [Binder014.]
  FillStyle = 0
  Fuse = false
  Group_EnableExport = false
  MakeFace = true
  PartialLoad = false
  Relative = true
  Support = -> [Body004[Pad025.Face4]]
  TreeRank = 622
  _Version = 8
FEATURE [PartDesign::Plane] DatumPlane006
  AttachmentOffset = pos=(0,0,4) rot=(0,0,1;0rad)
  Group_EnableExport = false
  Length = 564.778
  MapMode = 5
  MinimumLength = 10
  MinimumWidth = 10
  Placement = pos=(0,0,-63) rot=(0,0,1;0rad)
  ResizeMode = 0
  Support = -> [Binder014]
  TreeRank = 623
  Width = 607.502
FEATURE [Sketcher::SketchObject] Sketch024  label="driverot"
  AttachmentOffset = pos=(0,0,0) rot=(0,0,1;-1.5708rad)
  FullyConstrained = true
  MapMode = 5
  Placement = pos=(0,0,-63) rot=(0,0,1;4.71239rad)
  Support = -> [DatumPlane006]
  TreeRank = 603
  sketch-geometry (22):
    g0: LineSegment StartX=-104.5 StartY=-169 StartZ=0 EndX=-104.5 EndY=-165 EndZ=0
    g1: LineSegment StartX=-104.5 StartY=-165 StartZ=0 EndX=-89 EndY=-165 EndZ=0
    g2: LineSegment StartX=-89 StartY=-165 StartZ=0 EndX=-89 EndY=-164.5 EndZ=0
    g3: LineSegment StartX=-89 StartY=-164.5 StartZ=0 EndX=-86 EndY=-164.5 EndZ=0
    g4: LineSegment StartX=-86 StartY=-164.5 StartZ=0 EndX=-86 EndY=-156.5 EndZ=0
    g5: LineSegment StartX=-86 StartY=-156.5 StartZ=0 EndX=-83 EndY=-156.5 EndZ=0
    g6: LineSegment StartX=-83 StartY=-156.5 StartZ=0 EndX=-83 EndY=-140.5 EndZ=0
    g7: LineSegment StartX=-83 StartY=-140.5 StartZ=0 EndX=-78 EndY=-140.5 EndZ=0
    g8: LineSegment StartX=-78 StartY=-140.5 StartZ=0 EndX=-78 EndY=-150 EndZ=0
    g9: LineSegment StartX=-78 StartY=-150 StartZ=0 EndX=-27.5 EndY=-150 EndZ=0
    g10: LineSegment StartX=-27.5 StartY=-150 StartZ=0 EndX=-27.5 EndY=-153.2 EndZ=0
    g11: LineSegment StartX=-27.5 StartY=-153.2 StartZ=0 EndX=-25.5 EndY=-153.2 EndZ=0
    g12: LineSegment StartX=-25.5 StartY=-153.2 StartZ=0 EndX=-25.5 EndY=-151.5 EndZ=0
    g13: LineSegment StartX=-25.5 StartY=-151.5 StartZ=0 EndX=2.2 EndY=-151.5 EndZ=0
    g14: LineSegment StartX=2.2 StartY=-151.5 StartZ=0 EndX=2.2 EndY=-149.9 EndZ=0
    g15: LineSegment StartX=2.2 StartY=-149.9 StartZ=0 EndX=20.8 EndY=-149.9 EndZ=0
    g16: LineSegment StartX=20.8 StartY=-149.9 StartZ=0 EndX=20.8 EndY=-156.5 EndZ=0
    g17: LineSegment StartX=20.8 StartY=-156.5 StartZ=0 EndX=40.6 EndY=-156.5 EndZ=0
    g18: LineSegment StartX=40.6 StartY=-156.5 StartZ=0 EndX=40.6 EndY=-158 EndZ=0
    g19: LineSegment StartX=40.6 StartY=-158 StartZ=0 EndX=73.2 EndY=-158 EndZ=0
    g20: LineSegment StartX=73.2 StartY=-158 StartZ=0 EndX=73.2 EndY=-169 EndZ=0
    g21: LineSegment StartX=73.2 StartY=-169 StartZ=0 EndX=-104.5 EndY=-169 EndZ=0
  constraints (66):
    c: Vertical(g0)
    c: Coincident(g0,g1)
    c: Horizontal(g1)
    c: Coincident(g1,g2)
    c: Coincident(g2,g3)
    c: Coincident(g3,g4)
    c: Vertical(g4)
    c: Coincident(g4,g5)
    c: Coincident(g5,g6)
    c: Vertical(g6)
    c: Coincident(g6,g7)
    c: Coincident(g7,g8)
    c: Vertical(g8)
    c: Coincident(g8,g9)
    c: Horizontal(g9)
    c: Coincident(g9,g10)
    c: Vertical(g10)
    c: Coincident(g10,g11)
    c: Coincident(g11,g12)
    c: Coincident(g12,g13)
    c: Horizontal(g13)
    c: Coincident(g13,g14)
    c: Vertical(g14)
    c: Coincident(g14,g15)
    c: Horizontal(g15)
    c: Coincident(g15,g16)
    c: Vertical(g16)
    c: Coincident(g16,g17)
    c: Horizontal(g17)
    c: Coincident(g17,g18)
    c: Coincident(g18,g19)
    c: Horizontal(g19)
    c: Coincident(g19,g20)
    c: Coincident(g20,g21)
    c: Coincident(g21,g0)
    c: Horizontal(g21)
    c: Vertical(g20)
    c: Horizontal(g5)
    c: Horizontal(g3)
    c: Vertical(g2)
    c: Horizontal(g11)
    c: Vertical(g12)
    c: Vertical(g18)
    c: DistanceY(g0,g0) = 4
    c: DistanceY(g2,g2) = 0.5
    c: DistanceY(g0,g4) = 12.5
    c: DistanceY(g0,g6) = 28.5
    c: Horizontal(g7)
    c: DistanceY(g0,g8) = 19
    c: DistanceY(g0,g10) = 15.8
    c: DistanceY(g0,g12) = 17.5
    c: DistanceY(g20,g14) = 19.1
    c: DistanceY(g20,g16) = 12.5
    c: DistanceY(g20,g18) = 11
    c: DistanceX(g0,g1) = 15.5
    c: DistanceX(g1,g3) = 3
    c: DistanceX(g3,g5) = 3
    c: DistanceX(g5,g8) = 5
    c: DistanceX(g8,g9) = 50.5
    c: DistanceX(g10,g11) = 2
    c: DistanceX(g11,g13) = 27.7
    c: DistanceX(g13,g16) = 18.6
    c: DistanceX(g16,g17) = 19.8
    c: DistanceX(g18,g19) = 32.6
    c: DistanceX(g7,g-1) = 78
    c: DistanceY(g8,g-1) = 150
FEATURE [PartDesign::Revolution] Revolution002
  AddSubType = 0
  Angle = 360
  Axis = (2e-16,1,0)
  Base = (-169,-73.2,-63)
  ClaimChildren = false
  Fit = 0
  FitJoin = 0
  Group_EnableExport = false
  InnerFit = 0
  InnerFitJoin = 0
  Linearize = true
  NewSolid = false
  Placement = pos=(0,0,-63) rot=(0,0,1;0rad)
  Profile = -> Sketch024
  ReferenceAxis = -> Sketch024 [Edge22]
  Refine = true
  Suppress = false
  TreeRank = 604
  _ProfileBasedVersion = 1
FEATURE [PartDesign::Chamfer] Chamfer008
  AddSubType = 0
  Angle = 45
  Base = -> Revolution002 [Edge1]
  BaseFeature = -> Revolution002
  ChamferType = 0
  FlipDirection = false
  Group_EnableExport = false
  NewSolid = false
  Placement = pos=(0,0,-63) rot=(0,0,1;0rad)
  Refine = true
  Size = 0.2
  Size2 = 1
  SupportTransform = false
  Suppress = false
  TreeRank = 605
FEATURE [PartDesign::Chamfer] Chamfer009
  AddSubType = 0
  Angle = 45
  Base = -> Chamfer008 [Edge6]
  BaseFeature = -> Chamfer008
  ChamferType = 1
  FlipDirection = false
  Group_EnableExport = false
  NewSolid = false
  Placement = pos=(0,0,-63) rot=(0,0,1;0rad)
  Refine = true
  Size = 0.4
  Size2 = 2
  SupportTransform = false
  Suppress = false
  TreeRank = 606
FEATURE [PartDesign::Chamfer] Chamfer010
  AddSubType = 0
  Angle = 45
  Base = -> Chamfer009 [Edge11,Edge14,Edge15]
  BaseFeature = -> Chamfer009
  ChamferType = 0
  FlipDirection = false
  Group_EnableExport = false
  NewSolid = false
  Placement = pos=(0,0,-63) rot=(0,0,1;0rad)
  Refine = true
  Size = 0.4
  Size2 = 1
  SupportTransform = false
  Suppress = false
  TreeRank = 607
FEATURE [PartDesign::Chamfer] Chamfer011
  AddSubType = 0
  Angle = 45
  Base = -> Chamfer010 [Edge24,Edge36]
  BaseFeature = -> Chamfer010
  ChamferType = 0
  FlipDirection = false
  Group_EnableExport = false
  NewSolid = false
  Placement = pos=(0,0,-63) rot=(0,0,1;0rad)
  Refine = true
  Size = 0.8
  Size2 = 1
  SupportTransform = false
  Suppress = false
  TreeRank = 608
FEATURE [PartDesign::Chamfer] Chamfer012
  AddSubType = 0
  Angle = 45
  Base = -> Chamfer011 [Edge14]
  BaseFeature = -> Chamfer011
  ChamferType = 0
  FlipDirection = false
  Group_EnableExport = false
  NewSolid = false
  Placement = pos=(0,0,-63) rot=(0,0,1;0rad)
  Refine = true
  Size = 1
  Size2 = 1
  SupportTransform = false
  Suppress = false
  TreeRank = 609
FEATURE [PartDesign::Chamfer] Chamfer013
  AddSubType = 0
  Angle = 45
  Base = -> Chamfer012 [Edge13]
  BaseFeature = -> Chamfer012
  ChamferType = 1
  FlipDirection = false
  Group_EnableExport = false
  NewSolid = false
  Placement = pos=(0,0,-63) rot=(0,0,1;0rad)
  Refine = true
  Size = 1.5
  Size2 = 6
  SupportTransform = false
  Suppress = false
  TreeRank = 610
FEATURE [PartDesign::Fillet] Fillet021
  AddSubType = 0
  Base = -> Chamfer013 [Edge2]
  BaseFeature = -> Chamfer013
  Group_EnableExport = false
  NewSolid = false
  Placement = pos=(0,0,-63) rot=(0,0,1;0rad)
  Radius = 1.5
  Refine = true
  SupportTransform = false
  Suppress = false
  TreeRank = 611
FEATURE [Sketcher::SketchObject] Sketch025  label="holes"
  ExternalGeometry = -> [Fillet021]
  FullyConstrained = true
  MapMode = 5
  Placement = pos=(1.83e-14,83,-63) rot=(0,0.707107,0.707107;3.14159rad)
  Support = -> [Fillet021]
  TreeRank = 624
  sketch-geometry (9):
    g0: LineSegment [constr] StartX=151.5 StartY=-17.5 StartZ=0 EndX=151.5 EndY=17.5 EndZ=0
    g1: LineSegment [constr] StartX=151.5 StartY=17.5 StartZ=0 EndX=186.5 EndY=17.5 EndZ=0
    g2: LineSegment [constr] StartX=186.5 StartY=17.5 StartZ=0 EndX=186.5 EndY=-17.5 EndZ=0
    g3: LineSegment [constr] StartX=186.5 StartY=-17.5 StartZ=0 EndX=151.5 EndY=-17.5 EndZ=0
    g4: GeomPoint [constr] X=169 Y=0 Z=0
    g5: Circle CenterX=151.5 CenterY=17.5 CenterZ=0 NormalX=0 NormalY=0 NormalZ=1 AngleXU=0 Radius=2.5
    g6: Circle CenterX=186.5 CenterY=17.5 CenterZ=0 NormalX=0 NormalY=0 NormalZ=1 AngleXU=0 Radius=2.5
    g7: Circle CenterX=186.5 CenterY=-17.5 CenterZ=0 NormalX=0 NormalY=0 NormalZ=1 AngleXU=0 Radius=2.5
    g8: Circle CenterX=151.5 CenterY=-17.5 CenterZ=0 NormalX=0 NormalY=0 NormalZ=1 AngleXU=0 Radius=2.5
  constraints (20):
    c: Coincident(g0,g1)
    c: Coincident(g1,g2)
    c: Coincident(g2,g3)
    c: Coincident(g3,g0)
    c: Horizontal(g1)
    c: Horizontal(g3)
    c: Vertical(g0)
    c: Vertical(g2)
    c: Symmetric(g1,g0,g4)
    c: Coincident(g4,g-3)
    c: Equal(g3,g2)
    c: DistanceY(g2,g2) = 35
    c: Coincident(g5,g0)
    c: Coincident(g6,g1)
    c: Coincident(g7,g2)
    c: Coincident(g8,g0)
    c: Equal(g8,g5)
    c: Equal(g8,g7)
    c: Diameter(g8) = 5
    c: Equal(g7,g6)
FEATURE [PartDesign::Pocket] Pocket012
  AddSubType = 1
  BaseFeature = -> Fillet021
  CheckUpToFaceLimits = true
  ClaimChildren = false
  Fit = 0
  FitJoin = 0
  Group_EnableExport = false
  InnerFit = 0
  InnerFitJoin = 0
  InnerTaperAngle = 0
  InnerTaperAngleRev = 0
  Length = 6
  Length2 = 100
  Linearize = true
  NewSolid = false
  Placement = pos=(0,0,-63) rot=(0,0,1;0rad)
  Profile = -> Sketch025
  Refine = true
  Suppress = false
  TreeRank = 625
  Type = 0
  _ProfileBasedVersion = 1
  _Version = 1
FEATURE [PartDesign::Body] Body013  label="Drive"
  AutoGroupSolids = false
  ExportMode = 2
  Group = -> [Sketch024,Revolution002,Chamfer008,Chamfer009,Chamfer010,Chamfer011,Chamfer012,Chamfer013,Fillet021,Binder014,DatumPlane006,Sketch025,Pocket012]
  Origin = -> Origin014
  Tip = -> Pocket012
  TreeRank = 602
  _ExportChildren = -> [Revolution002,Chamfer008,Chamfer009,Chamfer010,Chamfer011,Chamfer012,Chamfer013,Fillet021,Binder014,DatumPlane006,Pocket012]
  _GroupVersion = 1
FEATURE [PartDesign::SubShapeBinder] Binder015  label="Binder015(Pocket012)..."
  BindCopyOnChange = 0
  BindMode = 0
  ClaimChildren = false
  Context = -> Body014 [Binder015.]
  FillStyle = 0
  Fuse = false
  MakeFace = true
  PartialLoad = false
  Relative = true
  Support = -> [Body013[Pocket012.Face25,Pocket012.Face17]]
  TreeRank = 626
  _Version = 8
FEATURE [PartDesign::Plane] DatumPlane007
  AttachmentOffset = pos=(0,0,-5) rot=(0,0,1;0rad)
  Length = 203.219
  MapMode = 5
  MinimumLength = 10
  MinimumWidth = 10
  Placement = pos=(1.72e-14,78,1.1e-15) rot=(0,0.707107,0.707107;3.14159rad)
  ResizeMode = 0
  Support = -> [Binder015]
  TreeRank = 627
  Width = 169.438
FEATURE [Sketcher::SketchObject] Sketch026  label="driveholdermaster"
  ExternalGeometry = -> [Binder015]
  FullyConstrained = true
  MapMode = 5
  Placement = pos=(1.72e-14,78,1.1e-15) rot=(0,0.707107,0.707107;3.14159rad)
  Support = -> [DatumPlane007]
  TreeRank = 628
  sketch-geometry (48):
    g0: Circle CenterX=169 CenterY=-63 CenterZ=0 NormalX=0 NormalY=0 NormalZ=1 AngleXU=0 Radius=19.15
    g1: LineSegment StartX=144.781 StartY=-38.7812 StartZ=0 EndX=144.781 EndY=-87.2188 EndZ=0
    g2: LineSegment StartX=144.781 StartY=-87.2188 StartZ=0 EndX=193.219 EndY=-87.2188 EndZ=0
    g3: LineSegment StartX=193.219 StartY=-87.2188 StartZ=0 EndX=193.219 EndY=-38.7812 EndZ=0
    g4: LineSegment StartX=193.219 StartY=-38.7812 StartZ=0 EndX=144.781 EndY=-38.7812 EndZ=0
    g5: GeomPoint [constr] X=169 Y=-63 Z=0
    g6: LineSegment StartX=189.222 StartY=-48.2224 StartZ=0 EndX=190.219 EndY=-44.5035 EndZ=0
    g7: LineSegment StartX=190.219 StartY=-44.5035 StartZ=0 EndX=187.496 EndY=-41.7812 EndZ=0
    g8: LineSegment StartX=187.496 StartY=-41.7812 StartZ=0 EndX=183.778 EndY=-42.7776 EndZ=0
    g9: LineSegment StartX=183.778 StartY=-42.7776 StartZ=0 EndX=182.781 EndY=-46.4965 EndZ=0
    g10: LineSegment StartX=182.781 StartY=-46.4965 StartZ=0 EndX=185.504 EndY=-49.2188 EndZ=0
    g11: LineSegment StartX=185.504 StartY=-49.2188 StartZ=0 EndX=189.222 EndY=-48.2224 EndZ=0
    g12: Circle [constr] CenterX=186.5 CenterY=-45.5 CenterZ=0 NormalX=0 NormalY=0 NormalZ=1 AngleXU=0 Radius=3.85
    g13: LineSegment StartX=155.156 StartY=-46.7075 StartZ=0 EndX=154.374 EndY=-42.9378 EndZ=0
    g14: LineSegment StartX=154.374 StartY=-42.9378 StartZ=0 EndX=150.718 EndY=-41.7303 EndZ=0
    g15: LineSegment StartX=150.718 StartY=-41.7303 StartZ=0 EndX=147.844 EndY=-44.2925 EndZ=0
    g16: LineSegment StartX=147.844 StartY=-44.2925 StartZ=0 EndX=148.626 EndY=-48.0622 EndZ=0
    g17: LineSegment StartX=148.626 StartY=-48.0622 StartZ=0 EndX=152.282 EndY=-49.2697 EndZ=0
    g18: LineSegment StartX=152.282 StartY=-49.2697 StartZ=0 EndX=155.156 EndY=-46.7075 EndZ=0
    g19: Circle [constr] CenterX=151.5 CenterY=-45.5 CenterZ=0 NormalX=0 NormalY=0 NormalZ=1 AngleXU=0 Radius=3.85
    g20: LineSegment StartX=154.374 StartY=-83.0622 StartZ=0 EndX=155.156 EndY=-79.2925 EndZ=0
    g21: LineSegment StartX=155.156 StartY=-79.2925 StartZ=0 EndX=152.282 EndY=-76.7303 EndZ=0
    g22: LineSegment StartX=152.282 StartY=-76.7303 StartZ=0 EndX=148.626 EndY=-77.9378 EndZ=0
    g23: LineSegment StartX=148.626 StartY=-77.9378 StartZ=0 EndX=147.844 EndY=-81.7075 EndZ=0
    g24: LineSegment StartX=147.844 StartY=-81.7075 StartZ=0 EndX=150.718 EndY=-84.2697 EndZ=0
    g25: LineSegment StartX=150.718 StartY=-84.2697 StartZ=0 EndX=154.374 EndY=-83.0622 EndZ=0
    g26: Circle [constr] CenterX=151.5 CenterY=-80.5 CenterZ=0 NormalX=0 NormalY=0 NormalZ=1 AngleXU=0 Radius=3.85
    g27: LineSegment StartX=187.496 StartY=-84.2188 StartZ=0 EndX=190.219 EndY=-81.4965 EndZ=0
    g28: LineSegment StartX=190.219 StartY=-81.4965 StartZ=0 EndX=189.222 EndY=-77.7776 EndZ=0
    g29: LineSegment StartX=189.222 StartY=-77.7776 StartZ=0 EndX=185.504 EndY=-76.7812 EndZ=0
    g30: LineSegment StartX=185.504 StartY=-76.7812 StartZ=0 EndX=182.781 EndY=-79.5035 EndZ=0
    g31: LineSegment StartX=182.781 StartY=-79.5035 StartZ=0 EndX=183.778 EndY=-83.2224 EndZ=0
    g32: LineSegment StartX=183.778 StartY=-83.2224 StartZ=0 EndX=187.496 EndY=-84.2188 EndZ=0
    g33: Circle [constr] CenterX=186.5 CenterY=-80.5 CenterZ=0 NormalX=0 NormalY=0 NormalZ=1 AngleXU=0 Radius=3.85
    g34: LineSegment [constr] StartX=144.781 StartY=-38.7812 StartZ=0 EndX=193.219 EndY=-87.2188 EndZ=0
    g35: LineSegment [constr] StartX=144.781 StartY=-87.2188 StartZ=0 EndX=193.219 EndY=-38.7812 EndZ=0
    g36: LineSegment StartX=154.958 StartY=-47.2512 StartZ=0 EndX=141.781 EndY=-59 EndZ=0
    g37: LineSegment StartX=141.781 StartY=-59 StartZ=0 EndX=81.7812 EndY=-59 EndZ=0
    g38: LineSegment StartX=81.7812 StartY=-59 StartZ=0 EndX=81.7812 EndY=-67 EndZ=0
    g39: LineSegment StartX=81.7812 StartY=-67 StartZ=0 EndX=141.781 EndY=-67 EndZ=0
    g40: LineSegment StartX=141.781 StartY=-67 StartZ=0 EndX=154.958 EndY=-78.7488 EndZ=0
    g41: LineSegment [constr] StartX=169 StartY=-63 StartZ=0 EndX=81.7812 EndY=-63 EndZ=0
    g42: GeomPoint [constr] X=141.781 Y=-63 Z=0
    g43: Circle CenterX=169 CenterY=-63 CenterZ=0 NormalX=0 NormalY=0 NormalZ=1 AngleXU=0 Radius=21.1
    g44: Circle CenterX=151.5 CenterY=-45.5 CenterZ=0 NormalX=0 NormalY=0 NormalZ=1 AngleXU=0 Radius=2.25
    g45: Circle CenterX=186.5 CenterY=-45.5 CenterZ=0 NormalX=0 NormalY=0 NormalZ=1 AngleXU=0 Radius=2.25
    g46: Circle CenterX=151.5 CenterY=-80.5 CenterZ=0 NormalX=0 NormalY=0 NormalZ=1 AngleXU=0 Radius=2.25
    g47: Circle CenterX=186.5 CenterY=-80.5 CenterZ=0 NormalX=0 NormalY=0 NormalZ=1 AngleXU=0 Radius=2.25
  constraints (111):
    c: Coincident(g0,g-4)
    c: Coincident(g1,g2)
    c: Coincident(g2,g3)
    c: Coincident(g3,g4)
    c: Coincident(g4,g1)
    c: Horizontal(g2)
    c: Horizontal(g4)
    c: Vertical(g1)
    c: Vertical(g3)
    c: Symmetric(g2,g1,g5)
    c: Coincident(g5,g0)
    c: Coincident(g6,g7)
    c: Coincident(g7,g8)
    c: Coincident(g8,g9)
    c: Coincident(g9,g10)
    c: Coincident(g10,g11)
    c: Coincident(g11,g6)
    c: Equal(g6, g7-g11) x5
    c: PointOnObject(g6,g12)
    c: PointOnObject(g7,g12)
    c: PointOnObject(g8,g12)
    c: PointOnObject(g9,g12)
    c: PointOnObject(g10,g12)
    c: PointOnObject(g11,g12)
    c: Coincident(g12,g-5)
    c: Coincident(g13,g14)
    c: Coincident(g14,g15)
    c: Coincident(g15,g16)
    c: Coincident(g16,g17)
    c: Coincident(g17,g18)
    c: Coincident(g18,g13)
    c: Equal(g13, g14-g18) x5
    c: PointOnObject(g13,g19)
    c: PointOnObject(g14,g19)
    c: PointOnObject(g15,g19)
    c: PointOnObject(g16,g19)
    c: PointOnObject(g17,g19)
    c: PointOnObject(g18,g19)
    c: Coincident(g19,g-6)
    c: Coincident(g20,g21)
    c: Coincident(g21,g22)
    c: Coincident(g22,g23)
    c: Coincident(g23,g24)
    c: Coincident(g24,g25)
    c: Coincident(g25,g20)
    c: Equal(g20, g21-g25) x5
    c: PointOnObject(g20,g26)
    c: PointOnObject(g21,g26)
    c: PointOnObject(g22,g26)
    c: PointOnObject(g23,g26)
    c: PointOnObject(g24,g26)
    c: PointOnObject(g25,g26)
    c: Coincident(g26,g-7)
    c: Coincident(g27,g28)
    c: Coincident(g28,g29)
    c: Coincident(g29,g30)
    c: Coincident(g30,g31)
    c: Coincident(g31,g32)
    c: Coincident(g32,g27)
    c: Equal(g27, g28-g32) x5
    c: PointOnObject(g27,g33)
    c: PointOnObject(g28,g33)
    c: PointOnObject(g29,g33)
    c: PointOnObject(g30,g33)
    c: PointOnObject(g31,g33)
    c: PointOnObject(g32,g33)
    c: Coincident(g33,g-8)
    c: Equal(g26,g19)
    c: Equal(g26,g12)
    c: Equal(g26,g33)
    c: Diameter(g26) = 7.7
    c: DistanceX(g6,g3) = 3
    c: DistanceY(g2,g27) = 3
    c: Diameter(g-4) = 38
    c: Diameter(g0) = 38.3
    c: Coincident(g34,g1)
    c: Coincident(g34,g2)
    c: Perpendicular(g34,g30)
    c: Coincident(g35,g1)
    c: Coincident(g35,g3)
    c: Perpendicular(g35,g10)
    c: Coincident(g36,g37)
    c: Horizontal(g37)
    c: Coincident(g37,g38)
    c: Vertical(g38)
    c: Coincident(g38,g39)
    c: Horizontal(g39)
    c: Coincident(g39,g40)
    c: DistanceY(g38,g38) = 8
    c: Equal(g39,g37)
    c: Coincident(g41,g0)
    c: PointOnObject(g41,g38)
    c: Horizontal(g41)
    c: PointOnObject(g42,g41)
    c: Symmetric(g36,g39,g42)
    c: DistanceX(g36,g1) = 3
    c: DistanceX(g38,g39) = 60
    c: Coincident(g43,g0)
    c: Diameter(g43) = 42.2
    c: Tangent(g36,g43) = -1.5708
    c: Tangent(g40,g43) = -1.5708
    c: Parallel(g21,g40)
    c: Parallel(g18,g36)
    c: Coincident(g44,g-6)
    c: Coincident(g45,g-5)
    c: Coincident(g46,g-7)
    c: Coincident(g47,g-8)
    c: Equal(g46,g44)
    c: Equal(g46,g45)
    c: Equal(g46,g47)
    c: Diameter(g46) = 4.5
FEATURE [Sketcher::SketchObject] Sketch027  label="driveholderscrewface"
  ExternalGeometry = -> [Sketch026]
  FullyConstrained = true
  MapMode = 5
  Placement = pos=(1.72e-14,78,1.1e-15) rot=(0,0.707107,0.707107;3.14159rad)
  Support = -> [DatumPlane007]
  TreeRank = 629
FEATURE [PartDesign::Pad] Pad046
  AddSubType = 0
  AlongSketchNormal = false
  CheckUpToFaceLimits = true
  ClaimChildren = false
  Direction = (2e-16,1,-2e-16)
  Fit = 0
  FitJoin = 0
  InnerFit = 0
  InnerFitJoin = 0
  InnerTaperAngle = 0
  InnerTaperAngleRev = 0
  Length = 8
  Length2 = 100
  Linearize = true
  NewSolid = false
  Placement = pos=(1.73e-14,78,1.1e-15) rot=(0,0.707107,0.707107;3.14159rad)
  Profile = -> Sketch027
  Refine = true
  Reversed = true
  Suppress = false
  TreeRank = 630
  Type = 0
  _ProfileBasedVersion = 1
FEATURE [Sketcher::SketchObject] Sketch028  label="driveholderextrude"
  ExternalGeometry = -> [Sketch026]
  FullyConstrained = true
  MapMode = 5
  Placement = pos=(1.72e-14,78,1.1e-15) rot=(0,0.707107,0.707107;3.14159rad)
  Support = -> [DatumPlane007]
  TreeRank = 631
  sketch-geometry (1):
    g0: ArcOfCircle CenterX=169 CenterY=-63 CenterZ=0 NormalX=0 NormalY=0 NormalZ=1 AngleXU=0 Radius=21.1 StartAngle=3.98421 EndAngle=8.58216
  constraints (2):
    c: Tangent(g0,g-4) = -1.5708
    c: Tangent(g0,g-3) = -1.5708
FEATURE [PartDesign::Pad] Pad047
  AddSubType = 0
  AlongSketchNormal = false
  BaseFeature = -> Pad046
  CheckUpToFaceLimits = true
  ClaimChildren = false
  Direction = (2e-16,1,-2e-16)
  Fit = 0
  FitJoin = 0
  InnerFit = 0
  InnerFitJoin = 0
  InnerTaperAngle = 0
  InnerTaperAngleRev = 0
  Length = 48
  Length2 = 100
  Linearize = true
  NewSolid = false
  Placement = pos=(1.73e-14,78,1.1e-15) rot=(0,0.707107,0.707107;3.14159rad)
  Profile = -> Sketch028
  Refine = true
  Reversed = true
  Suppress = false
  TreeRank = 632
  Type = 0
  _ProfileBasedVersion = 1
FEATURE [Sketcher::SketchObject] Sketch029  label="drivescrewholes"
  ExternalGeometry = -> [Sketch026]
  FullyConstrained = true
  MapMode = 5
  Placement = pos=(1.71e-14,70,3.7e-15) rot=(0,-0.707107,0.707107;3.14159rad)
  Support = -> [Pad047]
  TreeRank = 633
FEATURE [Part::FeaturePython] timinggear001  label="motorgearbelt"  # WARN: FeaturePython — macro-defined, semantics opaque (R4)
  AttacherType = Attacher::AttachEngine3D
  Placement = pos=(-169,96,-63) rot=(-1,0,0;1.5708rad)
  TreeRank = 641
  h = 0.75
  height = 9
  offset = 0.4
  pitch = 2
  r0 = 0.555
  r1 = 1
  rs = 0.15
  teeth = 16
  type = 0
  u = 0.254
  version = 0.0.3
FEATURE [PartDesign::Fillet] Fillet024
  AddSubType = 0
  Base = -> Pad047 [Edge13]
  BaseFeature = -> Pad047
  NewSolid = false
  Placement = pos=(1.73e-14,78,1.1e-15) rot=(0,0.707107,0.707107;3.14159rad)
  Radius = 1.3
  Refine = true
  SupportTransform = false
  Suppress = false
  TreeRank = 643
FEATURE [PartDesign::Pocket] Pocket013
  AddSubType = 1
  BaseFeature = -> Fillet024
  CheckUpToFaceLimits = true
  ClaimChildren = false
  Fit = 0
  FitJoin = 0
  InnerFit = 0
  InnerFitJoin = 0
  InnerTaperAngle = 0
  InnerTaperAngleRev = 0
  Length = 5
  Length2 = 100
  Linearize = true
  Midplane = true
  NewSolid = false
  Placement = pos=(1.73e-14,78,1.1e-15) rot=(0,0.707107,0.707107;3.14159rad)
  Profile = -> Sketch029
  Refine = true
  Suppress = false
  TreeRank = 634
  Type = 0
  _ProfileBasedVersion = 1
  _Version = 1
FEATURE [PartDesign::Fillet] Fillet022
  AddSubType = 0
  Base = -> Pocket013 [Edge100,Edge96,Edge102,Edge104,Edge135,Edge127]
  BaseFeature = -> Pocket013
  NewSolid = false
  Placement = pos=(1.73e-14,78,1.1e-15) rot=(0,0.707107,0.707107;3.14159rad)
  Radius = 8
  Refine = true
  SupportTransform = false
  Suppress = false
  TreeRank = 635
FEATURE [PartDesign::SubShapeBinder] Binder016  label="Binder016(MasterXZ)"
  BindCopyOnChange = 0
  BindMode = 0
  ClaimChildren = false
  Context = -> Body015 [Binder016.]
  FillStyle = 0
  Fuse = false
  MakeFace = true
  PartialLoad = false
  Relative = true
  Support = -> [Body[Sketch.]]
  TreeRank = 655
  _Version = 8
FEATURE [PartDesign::SubShapeBinder] Binder017  label="Binder017(Pad025)"
  BindCopyOnChange = 0
  BindMode = 0
  ClaimChildren = false
  Context = -> Body015 [Binder017.]
  FillStyle = 0
  Fuse = false
  MakeFace = true
  PartialLoad = false
  Relative = true
  Support = -> [Body004[Pad025.Face4]]
  TreeRank = 657
  _Version = 8
FEATURE [PartDesign::Body] Body002  label="Rockerbox"
  AutoGroupSolids = false
  ExportMode = 0
  Group = -> [ShapeBinder001,Sketch003,Import001,Export,Export001,Pad003,Pad,Export002,Export003,Pad004,Pad005]
  Origin = -> Origin002
  Tip = -> Pad005
  TreeRank = 38
  _ExportChildren = -> [ShapeBinder001,Sketch003,Import001,Pad003,Pad,Pad004,Pad005]
  _GroupVersion = 1
FEATURE [Sketcher::SketchObject] Sketch003  label="Rockerbox001"
  Exports = -> [Export,Export001,Export002,Export003]
  ExternalGeometry = -> [Import001]
  FullyConstrained = true
  MapMode = 2
  Support = -> [XY_Plane002]
  TreeRank = 40
FEATURE [Sketcher::SketchExport] Export  label="feeds"
  Base = -> Sketch003
  BaseRefs = -> Sketch003 [ExternalEdge2,ExternalEdge4,ExternalEdge3]
  Refs = ;e2.ExternalEdge2 | ;e4.ExternalEdge4 | ;e3.ExternalEdge3
  SyncPlacement = true
  TreeRank = 42
FEATURE [Sketcher::SketchExport] Export001  label="rotbottom"
  Base = -> Sketch003
  BaseRefs = -> Sketch003 [ExternalEdge1]
  MapMode = 5
  Placement = pos=(0,0,18) rot=(0,0,1;0rad)
  Refs = ;e1.ExternalEdge1
  Support = -> [Pad003]
  SyncPlacement = true
  TreeRank = 43
FEATURE [PartDesign::Pad] Pad
  AddSubType = 0
  BaseFeature = -> Pad003
  CheckUpToFaceLimits = true
  ClaimChildren = false
  Direction = (0,0,1)
  Fit = 0
  FitJoin = 0
  InnerFit = 0
  InnerFitJoin = 0
  InnerTaperAngle = 0
  InnerTaperAngleRev = 0
  Length = 16
  Length2 = 100
  Linearize = true
  NewSolid = false
  Profile = -> Export001
  Suppress = false
  TreeRank = 44
  Type = 0
  _ProfileBasedVersion = 1
  expr: Length = <<measures>>.Rockerboxthickness
FEATURE [PartDesign::Pad] Pad003
  AddSubType = 0
  CheckUpToFaceLimits = true
  ClaimChildren = false
  Direction = (0,0,1)
  Fit = 0
  FitJoin = 0
  InnerFit = 0
  InnerFitJoin = 0
  InnerTaperAngle = 0
  InnerTaperAngleRev = 0
  Length = 18
  Length2 = 100
  Linearize = true
  NewSolid = false
  Profile = -> Export
  Suppress = false
  TreeRank = 48
  Type = 0
  _ProfileBasedVersion = 1
  expr: Length = <<measures>>.RockerboxMinFeedHight
FEATURE [Sketcher::SketchExport] Export002  label="rottop"
  Base = -> Sketch003
  BaseRefs = -> Sketch003 [ExternalEdge1]
  MapMode = 5
  Placement = pos=(0,0,37) rot=(0,0,1;0rad)
  Refs = ;e1.ExternalEdge1
  Support = -> [Pad004]
  SyncPlacement = true
  TreeRank = 49
FEATURE [Sketcher::SketchExport] Export003  label="teflonpads"
  Base = -> Sketch003
  BaseRefs = -> Sketch003 [ExternalEdge2,ExternalEdge3,ExternalEdge4]
  MapMode = 5
  Placement = pos=(0,0,34) rot=(0,0,1;0rad)
  Refs = ;e2.ExternalEdge2 | ;e3.ExternalEdge3 | ;e4.ExternalEdge4
  Support = -> [Pad]
  SyncPlacement = true
  TreeRank = 50
FEATURE [PartDesign::Pad] Pad004
  AddSubType = 0
  BaseFeature = -> Pad
  CheckUpToFaceLimits = true
  ClaimChildren = false
  Direction = (0,0,1)
  Fit = 0
  FitJoin = 0
  InnerFit = 0
  InnerFitJoin = 0
  InnerTaperAngle = 0
  InnerTaperAngleRev = 0
  Length = 3
  Length2 = 100
  Linearize = true
  NewSolid = false
  Profile = -> Export003
  Suppress = false
  TreeRank = 51
  Type = 0
  _ProfileBasedVersion = 1
  expr: Length = <<measures>>.teflonpadgap
FEATURE [PartDesign::Pad] Pad005
  AddSubType = 0
  BaseFeature = -> Pad004
  CheckUpToFaceLimits = true
  ClaimChildren = false
  Direction = (0,0,1)
  Fit = 0
  FitJoin = 0
  InnerFit = 0
  InnerFitJoin = 0
  InnerTaperAngle = 0
  InnerTaperAngleRev = 0
  Length = 16
  Length2 = 100
  Linearize = true
  NewSolid = false
  Profile = -> Export002
  Suppress = false
  TreeRank = 52
  Type = 0
  _ProfileBasedVersion = 1
  expr: Length = <<measures>>.Rockerboxthickness
FEATURE [Sketcher::SketchObject] Sketch006  label="bearing"
  Exports = -> [Export009,Export032,Export033,Export034]
  ExternalGeometry = -> [Import003]
  FullyConstrained = true
  MapMode = 5
  Placement = pos=(0,0,-15) rot=(1,0,0;3.14159rad)
  Support = -> [Pad006]
  TreeRank = 104
  expr: Constraints[1] = <<measures>>.southbearingaxisdia - 0.5
  sketch-geometry (26):
    g0: Circle CenterX=317.656 CenterY=-4.1e-15 CenterZ=0 NormalX=0 NormalY=0 NormalZ=1 AngleXU=0 Radius=4.75
    g1: LineSegment [constr] StartX=317.656 StartY=20.5 StartZ=0 EndX=317.656 EndY=-20.5 EndZ=0
    g2: ArcOfCircle CenterX=317.656 CenterY=21.85 CenterZ=0 NormalX=0 NormalY=0 NormalZ=1 AngleXU=0 Radius=2.65 StartAngle=-1.208e-13 EndAngle=3.14159
    g3: ArcOfCircle CenterX=317.656 CenterY=19.15 CenterZ=0 NormalX=0 NormalY=0 NormalZ=1 AngleXU=0 Radius=2.65 StartAngle=3.14159 EndAngle=6.28319
    g4: LineSegment StartX=315.006 StartY=21.85 StartZ=0 EndX=315.006 EndY=19.15 EndZ=0
    g5: LineSegment StartX=320.306 StartY=19.15 StartZ=0 EndX=320.306 EndY=21.85 EndZ=0
    g6: ArcOfCircle CenterX=317.656 CenterY=-21.85 CenterZ=0 NormalX=0 NormalY=0 NormalZ=1 AngleXU=0 Radius=2.65 StartAngle=3.14159 EndAngle=6.28319
    g7: ArcOfCircle CenterX=317.656 CenterY=-19.15 CenterZ=0 NormalX=0 NormalY=0 NormalZ=1 AngleXU=0 Radius=2.65 StartAngle=-6.84e-14 EndAngle=3.14159
    g8: LineSegment StartX=320.306 StartY=-21.85 StartZ=0 EndX=320.306 EndY=-19.15 EndZ=0
    g9: LineSegment StartX=315.006 StartY=-19.15 StartZ=0 EndX=315.006 EndY=-21.85 EndZ=0
    g10: Circle CenterX=317.656 CenterY=-4.1e-15 CenterZ=0 NormalX=0 NormalY=0 NormalZ=1 AngleXU=0 Radius=6
    g11: Circle CenterX=317.656 CenterY=-4.1e-15 CenterZ=0 NormalX=0 NormalY=0 NormalZ=1 AngleXU=0 Radius=12.5
    g12: LineSegment [constr] StartX=317.656 StartY=20.5 StartZ=0 EndX=317.656 EndY=24.5 EndZ=0
    g13: LineSegment [constr] StartX=317.656 StartY=-20.5 StartZ=0 EndX=317.656 EndY=-24.5 EndZ=0
    g14: ArcOfCircle CenterX=317.656 CenterY=20.5 CenterZ=0 NormalX=0 NormalY=0 NormalZ=1 AngleXU=0 Radius=7.85 StartAngle=0.382423 EndAngle=2.75917
    g15: LineSegment StartX=324.939 StartY=23.4294 StartZ=0 EndX=332.037 EndY=5.78414 EndZ=0
    g16: ArcOfCircle CenterX=317.656 CenterY=-2.9e-15 CenterZ=0 NormalX=0 NormalY=0 NormalZ=1 AngleXU=0 Radius=15.5 StartAngle=5.90076 EndAngle=6.66561
    g17: LineSegment StartX=332.037 StartY=-5.78414 StartZ=0 EndX=324.939 EndY=-23.4294 EndZ=0
    g18: ArcOfCircle CenterX=317.656 CenterY=-20.5 CenterZ=0 NormalX=0 NormalY=0 NormalZ=1 AngleXU=0 Radius=7.85 StartAngle=3.52402 EndAngle=5.90076
    g19: LineSegment StartX=310.373 StartY=-23.4294 StartZ=0 EndX=303.276 EndY=-5.78417 EndZ=0
    g20: ArcOfCircle CenterX=317.656 CenterY=-4.1e-15 CenterZ=0 NormalX=0 NormalY=0 NormalZ=1 AngleXU=0 Radius=15.5 StartAngle=2.75917 EndAngle=3.52402
    g21: LineSegment StartX=303.276 StartY=5.78417 StartZ=0 EndX=310.373 EndY=23.4294 EndZ=0
    g22: LineSegment [constr] StartX=317.656 StartY=-24.5 StartZ=0 EndX=317.656 EndY=-28.35 EndZ=0
    g23: LineSegment [constr] StartX=317.656 StartY=24.5 StartZ=0 EndX=317.656 EndY=28.35 EndZ=0
    g24: LineSegment [constr] StartX=317.656 StartY=-4.1e-15 StartZ=0 EndX=302.156 EndY=-4.1e-15 EndZ=0
    g25: LineSegment [constr] StartX=317.656 StartY=-4.1e-15 StartZ=0 EndX=333.156 EndY=-4.1e-15 EndZ=0
  constraints (63):
    c: Coincident(g0,g-3)
    c: Diameter(g0) = 9.5
    c: Vertical(g1)
    c: Symmetric(g1,g1,g0)
    c: Tangent(g2,g4) = -1.5708
    c: Tangent(g4,g3) = -1.5708
    c: Tangent(g3,g5) = -1.5708
    c: Tangent(g5,g2) = -1.5708
    c: Equal(g2,g3)
    c: PointOnObject(g3,g1)
    c: Tangent(g6,g8) = -1.5708
    c: Tangent(g8,g7) = -1.5708
    c: Tangent(g7,g9) = -1.5708
    c: Tangent(g9,g6) = -1.5708
    c: Equal(g6,g7)
    c: PointOnObject(g7,g1)
    c: Symmetric(g6,g7,g1)
    c: Symmetric(g3,g2,g1)
    c: Coincident(g10,g0)
    c: Diameter(g10) = 12
    c: Coincident(g11,g0)
    c: Diameter(g11) = 25
    c: DistanceY(g1,g1) = 41
    c: Equal(g2,g6)
    c: DistanceX(g2,g2) = 5.3
    c: Equal(g8,g5)
    c: Coincident(g12,g1)
    c: PointOnObject(g12,g2)
    c: Vertical(g12)
    c: Coincident(g13,g1)
    c: PointOnObject(g13,g6)
    c: Vertical(g13)
    c: DistanceY(g13,g1) = 4
    c: Tangent(g14,g15) = 1.5708
    c: Tangent(g15,g16) = 1.5708
    c: Tangent(g16,g17) = 1.5708
    c: Tangent(g17,g18) = 1.5708
    c: Tangent(g18,g19) = 1.5708
    c: Tangent(g19,g20) = 1.5708
    c: Tangent(g20,g21) = 1.5708
    c: Tangent(g14,g21) = 1.5708
    c: Coincident(g18,g1)
    c: Equal(g21,g15)
    c: Equal(g15,g19)
    c: Equal(g19,g17)
    c: Equal(g20,g16)
    c: Equal(g14,g18)
    c: Coincident(g22,g13)
    c: PointOnObject(g22,g18)
    c: Vertical(g22)
    c: Coincident(g23,g12)
    c: Vertical(g23)
    c: PointOnObject(g23,g14)
    c: DistanceY(g22,g23) = 56.7
    c: Coincident(g24,g0)
    c: PointOnObject(g24,g20)
    c: Horizontal(g24)
    c: Coincident(g25,g0)
    c: PointOnObject(g25,g16)
    c: Horizontal(g25)
    c: DistanceX(g24,g25) = 31
    c: Coincident(g20,g0)
    c: PointOnObject(g14,g1)
FEATURE [Sketcher::SketchExport] Export009  label="axis"
  Base = -> Sketch006
  BaseRefs = -> Sketch006 [edge1]
  Placement = pos=(0,0,-15) rot=(1,0,0;3.14159rad)
  Refs = ;g15.edge1
  SyncPlacement = true
  TreeRank = 98
FEATURE [PartDesign::Body] Body003  label="Platformtop"
  AutoGroupSolids = false
  ExportMode = 0
  Group = -> [ShapeBinder002,Sketch005,Import002,Pad006,Sketch006,Import003,Export009,Export032,Export033,Export034,Pad035,Pad036,Pocket,Fillet008,Fillet009,Pad037]
  Origin = -> Origin003
  Tip = -> Pad037
  TreeRank = 117
  _ExportChildren = -> [ShapeBinder002,Import002,Pad006,Sketch006,Import003,Pad035,Pad036,Pocket,Fillet008,Fillet009,Pad037]
  _GroupVersion = 1
FEATURE [Sketcher::SketchObject] Sketch007
  Exports = -> [Export021,Export030]
  ExternalGeometry = -> [ShapeBinder003,ShapeBinder004]
  FullyConstrained = true
  MapMode = 5
  Support = -> [XY_Plane004]
  TreeRank = 121
  expr: Constraints[14] = <<measures>>.RockerboxFeedDiameter
  expr: Constraints[28] = <<measures>>.RockerboxFeedDiameter
  expr: Constraints[3] = <<measures>>.platformmidpointnorthbottom
  expr: Constraints[8] = <<measures>>.RockerboxFeedDiameter / 2
  sketch-geometry (14):
    g0: LineSegment StartX=-172 StartY=-253.836 StartZ=0 EndX=-172 EndY=-207.356 EndZ=0
    g1: LineSegment StartX=-172 StartY=253.836 StartZ=0 EndX=-172 EndY=207.356 EndZ=0
    g2: LineSegment [constr] StartX=225 StartY=0 StartZ=0 EndX=-135 EndY=0 EndZ=0
    g3: LineSegment [constr] StartX=225 StartY=0 StartZ=0 EndX=-134.151 EndY=207.356 EndZ=0
    g4: LineSegment [constr] StartX=225 StartY=0 StartZ=0 EndX=-134.151 EndY=-207.356 EndZ=0
    g5: LineSegment [constr] StartX=225 StartY=0 StartZ=0 EndX=250 EndY=0 EndZ=0
    g6: Circle CenterX=250 CenterY=0 CenterZ=0 NormalX=0 NormalY=0 NormalZ=1 AngleXU=0 Radius=25
    g7: Circle CenterX=-134.151 CenterY=207.356 CenterZ=0 NormalX=0 NormalY=0 NormalZ=1 AngleXU=0 Radius=25
    g8: Circle CenterX=-134.151 CenterY=-207.356 CenterZ=0 NormalX=0 NormalY=0 NormalZ=1 AngleXU=0 Radius=25
    g9: ArcOfCircle CenterX=-134.151 CenterY=207.356 CenterZ=0 NormalX=0 NormalY=0 NormalZ=1 AngleXU=0 Radius=37.8494 StartAngle=3.14159 EndAngle=4.28852
    g10: ArcOfCircle CenterX=-134.151 CenterY=-207.356 CenterZ=0 NormalX=0 NormalY=0 NormalZ=1 AngleXU=0 Radius=37.8494 StartAngle=1.99467 EndAngle=3.14159
    g11: ArcOfCircle CenterX=-160 CenterY=150.068 CenterZ=0 NormalX=0 NormalY=0 NormalZ=1 AngleXU=0 Radius=25 StartAngle=0 EndAngle=1.14693
    g12: ArcOfCircle CenterX=-160 CenterY=-150.068 CenterZ=0 NormalX=0 NormalY=0 NormalZ=1 AngleXU=0 Radius=25 StartAngle=5.13626 EndAngle=6.28319
    g13: LineSegment StartX=-135 StartY=-150.068 StartZ=0 EndX=-135 EndY=150.068 EndZ=0
  constraints (32):
    c: Tangent(g-7,g0) = 1.5708
    c: Coincident(g2,g-10)
    c: Tangent(g1,g-3) = -1.5708
    c: DistanceX(g2,g2) = 360
    c: Coincident(g3,g-10)
    c: Coincident(g4,g-10)
    c: Coincident(g5,g-10)
    c: PointOnObject(g5,g-1)
    c: Distance(g5,g-10) = 25
    c: Coincident(g6,g5)
    c: Coincident(g7,g3)
    c: Coincident(g8,g4)
    c: Equal(g8,g6)
    c: Equal(g8,g7)
    c: Diameter(g8) = 50
    c: PointOnObject(g-8,g4)
    c: PointOnObject(g-9,g3)
    c: PointOnObject(g7,g-9)
    c: Coincident(g10,g8)
    c: Tangent(g10,g0) = 1.5708
    c: Tangent(g9,g1) = -1.5708
    c: Coincident(g9,g7)
    c: Vertical(g13)
    c: Tangent(g13,g12) = -1.5708
    c: Tangent(g12,g10) = 1.5708
    c: PointOnObject(g8,g-8)
    c: Tangent(g11,g9) = 1.5708
    c: Tangent(g13,g11) = -1.5708
    c: Diameter(g11) = 50
    c: Equal(g11,g12)
    c: PointOnObject(g2,g13)
    c: PointOnObject(g2,g-1)
FEATURE [PartDesign::Body] Body004  label="Platformbottom"
  AutoGroupSolids = false
  ExportMode = 0
  Group = -> [ShapeBinder003,ShapeBinder004,Sketch007,Import004,Binder001,Export021,Pad034,Pad025,Export030]
  Origin = -> Origin004
  Tip = -> Pad025
  TreeRank = 135
  _ExportChildren = -> [ShapeBinder003,ShapeBinder004,Sketch007,Import004,Binder001,Pad034,Pad025]
  _GroupVersion = 1
FEATURE [PartDesign::Body] Body006  label="Roller"
  AutoGroupSolids = false
  ExportMode = 0
  Group = -> [Sketch009,Export017,Export018,ShapeBinder005,Pad020,Pad021,DatumPlane,Revolution001,Fillet006,Import009,Export029,Binder009]
  Origin = -> Origin006
  Tip = -> Fillet006
  TreeRank = 338
  _ExportChildren = -> [Sketch009,ShapeBinder005,Pad020,Pad021,DatumPlane,Revolution001,Fillet006,Import009,Binder009]
  _GroupVersion = 1
FEATURE [Sketcher::SketchObject] Sketch009  label="rollercage"
  Exports = -> [Export017,Export018,Export029]
  ExternalGeometry = -> [Import009]
  FullyConstrained = true
  MapMode = 5
  Placement = pos=(0,0,-67) rot=(0,0,1;0rad)
  Support = -> [Binder009]
  TreeRank = 192
  sketch-geometry (18):
    g0: LineSegment StartX=-118.833 StartY=-195.925 StartZ=0 EndX=-110.565 EndY=-214.137 EndZ=0
    g1: LineSegment StartX=-110.565 StartY=-214.137 StartZ=0 EndX=-118.76 EndY=-217.857 EndZ=0
    g2: LineSegment StartX=-118.76 StartY=-217.857 StartZ=0 EndX=-127.028 EndY=-199.646 EndZ=0
    g3: LineSegment StartX=-127.028 StartY=-199.646 StartZ=0 EndX=-118.833 EndY=-195.925 EndZ=0
    g4: LineSegment StartX=-118.833 StartY=-195.925 StartZ=0 EndX=-114.28 EndY=-193.859 EndZ=0
    g5: LineSegment StartX=-114.28 StartY=-193.859 StartZ=0 EndX=-106.012 EndY=-212.07 EndZ=0
    g6: LineSegment StartX=-106.012 StartY=-212.07 StartZ=0 EndX=-110.565 EndY=-214.137 EndZ=0
    g7: LineSegment StartX=-127.028 StartY=-199.646 StartZ=0 EndX=-131.581 EndY=-201.713 EndZ=0
    g8: LineSegment StartX=-131.581 StartY=-201.713 StartZ=0 EndX=-123.313 EndY=-219.924 EndZ=0
    g9: LineSegment StartX=-123.313 StartY=-219.924 StartZ=0 EndX=-118.76 EndY=-217.857 EndZ=0
    g10: LineSegment StartX=-118.797 StartY=-206.891 StartZ=0 EndX=-121.984 EndY=-208.338 EndZ=0
    g11: LineSegment StartX=-121.984 StartY=-208.338 StartZ=0 EndX=-125.291 EndY=-201.054 EndZ=0
    g12: LineSegment StartX=-118.917 StartY=-198.16 StartZ=0 EndX=-115.61 EndY=-205.444 EndZ=0
    g13: LineSegment StartX=-115.61 StartY=-205.444 StartZ=0 EndX=-118.797 EndY=-206.891 EndZ=0
    g14: LineSegment [constr] StartX=-122.517 StartY=-198.696 StartZ=0 EndX=-118.797 EndY=-206.891 EndZ=0
    g15: LineSegment StartX=-125.291 StartY=-201.054 StartZ=0 EndX=-123.681 EndY=-200.323 EndZ=0
    g16: LineSegment StartX=-120.526 StartY=-198.891 StartZ=0 EndX=-118.917 EndY=-198.16 EndZ=0
    g17: ArcOfCircle CenterX=-122.517 CenterY=-198.696 CenterZ=0 NormalX=0 NormalY=0 NormalZ=1 AngleXU=0 Radius=2 StartAngle=4.09136 EndAngle=6.18575
  constraints (49):
    c: Coincident(g0,g1)
    c: Coincident(g1,g2)
    c: Coincident(g2,g3)
    c: Coincident(g3,g0)
    c: Distance(g0,g0) = 20
    c: Distance(g1) = 9
    c: Coincident(g0,g4)
    c: Coincident(g4,g5)
    c: Coincident(g5,g6)
    c: Coincident(g6,g0)
    c: Distance(g4) = 5
    c: Coincident(g2,g7)
    c: Coincident(g7,g8)
    c: Coincident(g8,g9)
    c: Coincident(g9,g1)
    c: Coincident(g10,g11)
    c: Coincident(g12,g13)
    c: Distance(g13) = 3.5
    c: Perpendicular(g11,g10)
    c: Perpendicular(g13,g12)
    c: Coincident(g14,g10)
    c: Symmetric(g10,g12,g10)
    c: Coincident(g13,g10)
    c: Distance(g14) = 9
    c: Perpendicular(g2,g1)
    c: Perpendicular(g8,g9)
    c: Perpendicular(g0,g1)
    c: Perpendicular(g6,g5)
    c: Perpendicular(g9,g2)
    c: Perpendicular(g4,g0)
    c: Perpendicular(g2,g7)
    c: Perpendicular(g3,g2)
    c: Perpendicular(g6,g0)
    c: Distance(g7) = 5
    c: Symmetric(g0,g2,g10)
    c: Perpendicular(g10,g-4) = 1.5708
    c: PointOnObject(g10,g-3)
    c: Parallel(g12,g0)
    c: Equal(g11,g12)
    c: Coincident(g11,g15)
    c: Coincident(g16,g12)
    c: Equal(g16,g15)
    c: Perpendicular(g16,g12)
    c: Perpendicular(g15,g11)
    c: Coincident(g17,g14)
    c: Coincident(g17,g15)
    c: Coincident(g17,g16)
    c: Diameter(g17) = 4
    c: Distance(g12) = 8
FEATURE [Sketcher::SketchExport] Export017  label="rollercagefeet"
  Base = -> Sketch009
  BaseRefs = -> Sketch009 [edge9,edge8,edge4,edge5,edge6,edge7,edge2,edge10]
  MapMode = 5
  Placement = pos=(0,0,-67) rot=(0,0,1;0rad)
  Refs = ;g13.edge9 | ;g12.edge8 | ;g7.edge4 | ;g9.edge5 | ;g10.edge6 | ;g11.edge7 | ;g5.edge2 | ;g14.edge10
  Support = -> [Binder009]
  SyncPlacement = true
  TreeRank = 194
FEATURE [Sketcher::SketchExport] Export018  label="rollercageaxissupport"
  Base = -> Sketch009
  BaseRefs = -> Sketch009 [edge10,edge9,edge3,edge8,edge5,edge6,edge1,edge7]
  MapMode = 5
  Placement = pos=(0,0,-67) rot=(0,0,1;0rad)
  Refs = ;g14.edge10 | ;g13.edge9 | ;g6.edge3 | ;g12.edge8 | ;g9.edge5 | ;g10.edge6 | ;g4.edge1 | ;g11.edge7
  Support = -> [Binder009]
  SyncPlacement = true
  TreeRank = 195
FEATURE [PartDesign::Pad] Pad020
  AddSubType = 0
  AlongSketchNormal = false
  CheckUpToFaceLimits = true
  ClaimChildren = false
  Direction = (0,0,1)
  Fit = 0
  FitJoin = 0
  InnerFit = 0
  InnerFitJoin = 0
  InnerTaperAngle = 0
  InnerTaperAngleRev = 0
  Length = 1
  Length2 = 100
  Linearize = true
  NewSolid = false
  Profile = -> Export017
  Suppress = false
  TreeRank = 196
  Type = 0
  _ProfileBasedVersion = 1
FEATURE [PartDesign::Pad] Pad021
  AddSubType = 0
  AlongSketchNormal = false
  BaseFeature = -> Pad020
  CheckUpToFaceLimits = true
  ClaimChildren = false
  Direction = (0,0,1)
  Fit = 0
  FitJoin = 0
  InnerFit = 0
  InnerFitJoin = 0
  InnerTaperAngle = 0
  InnerTaperAngleRev = 0
  Length = 16
  Length2 = 100
  Linearize = true
  NewSolid = false
  Profile = -> Export018
  Suppress = false
  TreeRank = 197
  Type = 0
  _ProfileBasedVersion = 1
FEATURE [Sketcher::SketchObject] Sketch011  label="eli"
  Exports = -> [Export022,Export023,Export024,Export025]
  ExternalGeometry = -> [Binder]
  FullyConstrained = true
  MapMode = 5
  Placement = pos=(0,0,-15) rot=(1,0,0;3.14159rad)
  Support = -> [Binder004]
  TreeRank = 273
  expr: Constraints[0] = <<measures>>.ElipsePositionAngle
  expr: Constraints[128] = 10
  expr: Constraints[134] = <<measures>>.elipsefootSize
  expr: Constraints[166] = <<measures>>.elipsescrewholedia
  expr: Constraints[167] = <<measures>>.elipsescrewdistance
  expr: Constraints[168] = <<measures>>.elipsescrewdistance
  expr: Constraints[169] = <<measures>>.elipsescrewdistance
  expr: Constraints[170] = <<measures>>.elipsescrewdistance
  expr: Constraints[24] = <<measures>>.ElipseThickness / 2
  expr: Constraints[26] = <<measures>>.ElipseThickness / 2
  expr: Constraints[286] = <<measures>>.elipsefeednutsizeradius
  expr: Constraints[296] = <<measures>>.ElipsePositionAngle + 0.7
  expr: Constraints[328] = (<<measures>>.elipsefootSize - <<measures>>.ElipseThickness) / 4
  expr: Constraints[331] = (<<measures>>.elipsefootSize - <<measures>>.ElipseThickness) / 4
  expr: Constraints[333] = (<<measures>>.elipsefootSize - <<measures>>.ElipseThickness) / 4
  expr: Constraints[335] = (<<measures>>.elipsefootSize - <<measures>>.ElipseThickness) / 4
  expr: Constraints[38] = <<measures>>.ElipseThickness / 2
  expr: Constraints[39] = <<measures>>.ElipseThickness / 2
  expr: Constraints[57] = <<measures>>.ElipseMaxDeg / 2
  expr: Constraints[58] = <<measures>>.ElipseMaxDeg / 2
  expr: Constraints[90] = <<measures>>.elipsestoppermaxdeg
  expr: Constraints[95] = <<measures>>.elipsefootSize
  sketch-geometry (149):
    g0: LineSegment StartX=158.769 StartY=2.84e-14 StartZ=0 EndX=-245.739 EndY=293.893 EndZ=0
    g1: GeomPoint [constr] X=-120.564 Y=202.948 Z=0
    g2: LineSegment [constr] StartX=158.769 StartY=2.84e-14 StartZ=0 EndX=158.769 EndY=411.456 EndZ=0
    g3: LineSegment [constr] StartX=158.769 StartY=2.84e-14 StartZ=0 EndX=-162.344 EndY=2.84e-14 EndZ=0
    g4: ArcOfEllipse CenterX=158.769 CenterY=2.84e-14 CenterZ=0 NormalX=0 NormalY=0 NormalZ=1 MajorRadius=411.456 MinorRadius=321.113 AngleXU=1.5708 StartAngle=0.912331 EndAngle=1.18861
    g5: LineSegment [constr] StartX=158.769 StartY=411.456 StartZ=0 EndX=158.769 EndY=-411.456 EndZ=0
    g6: LineSegment [constr] StartX=-162.344 StartY=1.36215e-11 StartZ=0 EndX=479.882 EndY=-1.3543e-11 EndZ=0
    g7: GeomPoint [constr] X=158.769 Y=257.26 Z=0
    g8: GeomPoint [constr] X=158.769 Y=-257.26 Z=0
    g9: GeomPoint [constr] X=-158.744 Y=3.93e-14 Z=0
    g10: GeomPoint [constr] X=158.769 Y=407.856 Z=0
    g11: ArcOfEllipse CenterX=158.769 CenterY=2.84e-14 CenterZ=0 NormalX=0 NormalY=0 NormalZ=1 MajorRadius=407.856 MinorRadius=317.513 AngleXU=1.5708 StartAngle=0.913534 EndAngle=1.18947
    g12: LineSegment [constr] StartX=158.769 StartY=407.856 StartZ=0 EndX=158.769 EndY=-407.856 EndZ=0
    g13: LineSegment [constr] StartX=-158.744 StartY=5.41e-14 StartZ=0 EndX=476.282 EndY=2.44e-14 EndZ=0
    g14: GeomPoint [constr] X=158.769 Y=255.993 Z=0
    g15: GeomPoint [constr] X=158.769 Y=-255.993 Z=0
    g16: LineSegment [constr] StartX=-162.344 StartY=2.84e-14 StartZ=0 EndX=-165.944 EndY=0 EndZ=0
    g17: LineSegment [constr] StartX=158.769 StartY=411.456 StartZ=0 EndX=158.769 EndY=415.056 EndZ=0
    g18: LineSegment StartX=-139.176 StartY=153.452 StartZ=0 EndX=-142.414 EndY=155.12 EndZ=0
    g19: LineSegment StartX=-95.2091 StartY=251.772 StartZ=0 EndX=-97.8219 EndY=254.362 EndZ=0
    g20: ArcOfEllipse CenterX=158.769 CenterY=2.84e-14 CenterZ=0 NormalX=0 NormalY=0 NormalZ=1 MajorRadius=415.056 MinorRadius=324.713 AngleXU=1.5708 StartAngle=0.911151 EndAngle=1.18777
    g21: LineSegment [constr] StartX=158.769 StartY=415.056 StartZ=0 EndX=158.769 EndY=-415.056 EndZ=0
    g22: LineSegment [constr] StartX=-165.944 StartY=3.82e-14 StartZ=0 EndX=483.482 EndY=4.03e-14 EndZ=0
    g23: GeomPoint [constr] X=158.769 Y=258.521 Z=0
    g24: GeomPoint [constr] X=158.769 Y=-258.521 Z=0
    g25: LineSegment [constr] StartX=158.769 StartY=2.84e-14 StartZ=0 EndX=-92.5953 EndY=249.181 EndZ=0
    g26: LineSegment StartX=-92.5953 StartY=249.181 StartZ=0 EndX=-95.2091 EndY=251.772 EndZ=0
    g27: LineSegment [constr] StartX=158.769 StartY=2.84e-14 StartZ=0 EndX=-135.937 EndY=151.784 EndZ=0
    g28: LineSegment StartX=-135.937 StartY=151.784 StartZ=0 EndX=-139.176 EndY=153.452 EndZ=0
    g29: ArcOfEllipse CenterX=158.769 CenterY=2.84e-14 CenterZ=0 NormalX=0 NormalY=0 NormalZ=1 MajorRadius=411.456 MinorRadius=321.113 AngleXU=1.5708 StartAngle=0.895364 EndAngle=0.912331
    g30: LineSegment [constr] StartX=158.769 StartY=411.456 StartZ=0 EndX=158.769 EndY=-411.456 EndZ=0
    g31: LineSegment [constr] StartX=-162.344 StartY=7.85e-14 StartZ=0 EndX=479.882 EndY=0 EndZ=0
    g32: GeomPoint [constr] X=158.769 Y=257.26 Z=0
    g33: GeomPoint [constr] X=158.769 Y=-257.26 Z=0
    g34: ArcOfEllipse CenterX=158.769 CenterY=2.84e-14 CenterZ=0 NormalX=0 NormalY=0 NormalZ=1 MajorRadius=407.856 MinorRadius=317.513 AngleXU=1.5708 StartAngle=0.896577 EndAngle=0.913534
    g35: LineSegment [constr] StartX=158.769 StartY=407.856 StartZ=0 EndX=158.769 EndY=-407.856 EndZ=0
    g36: LineSegment [constr] StartX=-158.744 StartY=7.85e-14 StartZ=0 EndX=476.282 EndY=0 EndZ=0
    g37: GeomPoint [constr] X=158.769 Y=255.993 Z=0
    g38: GeomPoint [constr] X=158.769 Y=-255.993 Z=0
    g39: ArcOfEllipse CenterX=158.769 CenterY=2.84e-14 CenterZ=0 NormalX=0 NormalY=0 NormalZ=1 MajorRadius=415.056 MinorRadius=324.713 AngleXU=1.5708 StartAngle=0.894175 EndAngle=0.911151
    g40: LineSegment [constr] StartX=158.769 StartY=415.056 StartZ=0 EndX=158.769 EndY=-415.056 EndZ=0
    g41: LineSegment [constr] StartX=-165.944 StartY=7.85e-14 StartZ=0 EndX=483.482 EndY=0 EndZ=0
    g42: GeomPoint [constr] X=158.769 Y=258.521 Z=0
    g43: GeomPoint [constr] X=158.769 Y=-258.521 Z=0
    g44: LineSegment [constr] StartX=158.769 StartY=2.84e-14 StartZ=0 EndX=-89.2701 EndY=254.62 EndZ=0
    g45: LineSegment StartX=-89.2701 StartY=254.62 StartZ=0 EndX=-94.4069 EndY=259.893 EndZ=0
    g46: LineSegment StartX=-162.344 StartY=2.84e-14 StartZ=0 EndX=-179.844 EndY=0 EndZ=0
    g47: LineSegment StartX=-162.344 StartY=2.84e-14 StartZ=0 EndX=-144.844 EndY=7.85e-14 EndZ=0
    g48: ArcOfEllipse CenterX=158.769 CenterY=2.84e-14 CenterZ=0 NormalX=0 NormalY=0 NormalZ=1 MajorRadius=429.056 MinorRadius=338.613 AngleXU=1.5708 StartAngle=0.863362 EndAngle=1.20988
    g49: LineSegment [constr] StartX=158.769 StartY=429.056 StartZ=0 EndX=158.769 EndY=-429.056 EndZ=0
    g50: LineSegment [constr] StartX=-179.844 StartY=7.85e-14 StartZ=0 EndX=497.382 EndY=0 EndZ=0
    g51: GeomPoint [constr] X=158.769 Y=263.497 Z=0
    g52: GeomPoint [constr] X=158.769 Y=-263.497 Z=0
    g53: ArcOfEllipse CenterX=158.769 CenterY=2.84e-14 CenterZ=0 NormalX=0 NormalY=0 NormalZ=1 MajorRadius=393.856 MinorRadius=303.613 AngleXU=1.5708 StartAngle=0.874948 EndAngle=1.21758
    g54: LineSegment [constr] StartX=158.769 StartY=393.856 StartZ=0 EndX=158.769 EndY=-393.856 EndZ=0
    g55: LineSegment [constr] StartX=-144.844 StartY=7.85e-14 StartZ=0 EndX=462.382 EndY=0 EndZ=0
    g56: GeomPoint [constr] X=158.769 Y=250.882 Z=0
    g57: GeomPoint [constr] X=158.769 Y=-250.882 Z=0
    g58: ArcOfEllipse CenterX=158.769 CenterY=2.84e-14 CenterZ=0 NormalX=0 NormalY=0 NormalZ=1 MajorRadius=411.456 MinorRadius=321.113 AngleXU=1.5708 StartAngle=1.18861 EndAngle=1.21356
    g59: LineSegment [constr] StartX=158.769 StartY=411.456 StartZ=0 EndX=158.769 EndY=-411.456 EndZ=0
    g60: LineSegment [constr] StartX=-162.344 StartY=7.85e-14 StartZ=0 EndX=479.882 EndY=0 EndZ=0
    g61: GeomPoint [constr] X=158.769 Y=257.26 Z=0
    g62: GeomPoint [constr] X=158.769 Y=-257.26 Z=0
    g63: ArcOfEllipse CenterX=158.769 CenterY=2.84e-14 CenterZ=0 NormalX=0 NormalY=0 NormalZ=1 MajorRadius=411.456 MinorRadius=321.113 AngleXU=1.5708 StartAngle=0.868879 EndAngle=0.895364
    g64: LineSegment [constr] StartX=158.769 StartY=411.456 StartZ=0 EndX=158.769 EndY=-411.456 EndZ=0
    g65: LineSegment [constr] StartX=-162.344 StartY=7.85e-14 StartZ=0 EndX=479.882 EndY=0 EndZ=0
    g66: GeomPoint [constr] X=158.769 Y=257.26 Z=0
    g67: GeomPoint [constr] X=158.769 Y=-257.26 Z=0
    g68: LineSegment StartX=158.769 StartY=411.456 StartZ=0 EndX=158.769 EndY=428.956 EndZ=0
    g69: LineSegment StartX=158.769 StartY=411.456 StartZ=0 EndX=158.769 EndY=393.956 EndZ=0
    g70: GeomPoint [constr] X=-132.37 Y=139.241 Z=0
    g71: GeomPoint [constr] X=-78.9704 Y=257.583 Z=0
    g72: ArcOfEllipse CenterX=158.769 CenterY=2.84e-14 CenterZ=0 NormalX=0 NormalY=0 NormalZ=1 MajorRadius=400.416 MinorRadius=310.518 AngleXU=1.5708 StartAngle=0.872008 EndAngle=1.21564
    g73: LineSegment [constr] StartX=158.769 StartY=400.416 StartZ=0 EndX=158.769 EndY=-400.416 EndZ=0
    g74: LineSegment [constr] StartX=-151.749 StartY=7.85e-14 StartZ=0 EndX=469.288 EndY=0 EndZ=0
    g75: GeomPoint [constr] X=158.769 Y=252.806 Z=0
    g76: GeomPoint [constr] X=158.769 Y=-252.806 Z=0
    g77: GeomPoint [constr] X=-151.759 Y=148.513 Z=0
    g78: GeomPoint [constr] X=-93.8735 Y=273.73 Z=0
    g79: ArcOfEllipse CenterX=158.769 CenterY=2.84e-14 CenterZ=0 NormalX=0 NormalY=0 NormalZ=1 MajorRadius=422.434 MinorRadius=331.703 AngleXU=-1.5708 StartAngle=4.00746 EndAngle=4.35315
    g80: LineSegment [constr] StartX=158.769 StartY=-422.434 StartZ=0 EndX=158.769 EndY=422.434 EndZ=0
    g81: LineSegment [constr] StartX=490.472 StartY=0 StartZ=0 EndX=-172.933 EndY=7.85e-14 EndZ=0
    g82: GeomPoint [constr] X=158.769 Y=-261.58 Z=0
    g83: GeomPoint [constr] X=158.769 Y=261.58 Z=0
    g84: Circle CenterX=-84.3235 CenterY=249.137 CenterZ=0 NormalX=0 NormalY=0 NormalZ=1 AngleXU=0 Radius=3
    g85: Circle CenterX=-99.328 CenterY=265.349 CenterZ=0 NormalX=0 NormalY=0 NormalZ=1 AngleXU=0 Radius=3
    g86: Circle CenterX=-111.764 CenterY=196.554 CenterZ=0 NormalX=0 NormalY=0 NormalZ=1 AngleXU=0 Radius=3
    g87: Circle CenterX=-129.345 CenterY=209.328 CenterZ=0 NormalX=0 NormalY=0 NormalZ=1 AngleXU=0 Radius=3
    g88: Circle CenterX=-129.505 CenterY=148.821 CenterZ=0 NormalX=0 NormalY=0 NormalZ=1 AngleXU=0 Radius=3
    g89: Circle CenterX=-148.834 CenterY=158.076 CenterZ=0 NormalX=0 NormalY=0 NormalZ=1 AngleXU=0 Radius=3
    g90: LineSegment StartX=-81.6177 StartY=244.205 StartZ=0 EndX=-78.6999 EndY=249.015 EndZ=0
    g91: LineSegment StartX=-78.6999 StartY=249.015 StartZ=0 EndX=-81.4057 EndY=253.946 EndZ=0
    g92: LineSegment StartX=-81.4057 StartY=253.946 StartZ=0 EndX=-87.0294 EndY=254.068 EndZ=0
    g93: LineSegment StartX=-87.0294 StartY=254.068 StartZ=0 EndX=-89.9472 EndY=249.259 EndZ=0
    g94: LineSegment StartX=-89.9472 StartY=249.259 StartZ=0 EndX=-87.2414 EndY=244.328 EndZ=0
    g95: LineSegment StartX=-87.2414 StartY=244.328 StartZ=0 EndX=-81.6177 EndY=244.205 EndZ=0
    g96: Circle [constr] CenterX=-84.3235 CenterY=249.137 CenterZ=0 NormalX=0 NormalY=0 NormalZ=1 AngleXU=0 Radius=5.625
    g97: LineSegment StartX=-96.6861 StartY=260.383 StartZ=0 EndX=-93.7063 EndY=265.154 EndZ=0
    g98: LineSegment StartX=-93.7063 StartY=265.154 StartZ=0 EndX=-96.3482 EndY=270.12 EndZ=0
    g99: LineSegment StartX=-96.3482 StartY=270.12 StartZ=0 EndX=-101.97 EndY=270.315 EndZ=0
    g100: LineSegment StartX=-101.97 StartY=270.315 StartZ=0 EndX=-104.95 EndY=265.544 EndZ=0
    g101: LineSegment StartX=-104.95 StartY=265.544 StartZ=0 EndX=-102.308 EndY=260.578 EndZ=0
    g102: LineSegment StartX=-102.308 StartY=260.578 StartZ=0 EndX=-96.6861 EndY=260.383 EndZ=0
    g103: Circle [constr] CenterX=-99.328 CenterY=265.349 CenterZ=0 NormalX=0 NormalY=0 NormalZ=1 AngleXU=0 Radius=5.625
    g104: LineSegment StartX=-108.455 StartY=192.005 StartZ=0 EndX=-106.17 EndY=197.145 EndZ=0
    g105: LineSegment StartX=-106.17 StartY=197.145 StartZ=0 EndX=-109.479 EndY=201.694 EndZ=0
    g106: LineSegment StartX=-109.479 StartY=201.694 StartZ=0 EndX=-115.073 EndY=201.103 EndZ=0
    g107: LineSegment StartX=-115.073 StartY=201.103 StartZ=0 EndX=-117.357 EndY=195.962 EndZ=0
    g108: LineSegment StartX=-117.357 StartY=195.962 StartZ=0 EndX=-114.048 EndY=191.414 EndZ=0
    g109: LineSegment StartX=-114.048 StartY=191.414 StartZ=0 EndX=-108.455 EndY=192.005 EndZ=0
    g110: Circle [constr] CenterX=-111.764 CenterY=196.554 CenterZ=0 NormalX=0 NormalY=0 NormalZ=1 AngleXU=0 Radius=5.625
    g111: LineSegment StartX=-126.077 StartY=204.749 StartZ=0 EndX=-123.746 EndY=209.869 EndZ=0
    g112: LineSegment StartX=-123.746 StartY=209.869 StartZ=0 EndX=-127.014 EndY=214.447 EndZ=0
    g113: LineSegment StartX=-127.014 StartY=214.447 StartZ=0 EndX=-132.613 EndY=213.906 EndZ=0
    g114: LineSegment StartX=-132.613 StartY=213.906 StartZ=0 EndX=-134.944 EndY=208.786 EndZ=0
    g115: LineSegment StartX=-134.944 StartY=208.786 StartZ=0 EndX=-131.676 EndY=204.208 EndZ=0
    g116: LineSegment StartX=-131.676 StartY=204.208 StartZ=0 EndX=-126.077 EndY=204.749 EndZ=0
    g117: Circle [constr] CenterX=-129.345 CenterY=209.328 CenterZ=0 NormalX=0 NormalY=0 NormalZ=1 AngleXU=0 Radius=5.625
    g118: LineSegment StartX=-125.711 StartY=144.668 StartZ=0 EndX=-124.012 EndY=150.03 EndZ=0
    g119: LineSegment StartX=-124.012 StartY=150.03 StartZ=0 EndX=-127.806 EndY=154.183 EndZ=0
    g120: LineSegment StartX=-127.806 StartY=154.183 StartZ=0 EndX=-133.299 EndY=152.974 EndZ=0
    g121: LineSegment StartX=-133.299 StartY=152.974 StartZ=0 EndX=-134.999 EndY=147.612 EndZ=0
    g122: LineSegment StartX=-134.999 StartY=147.612 StartZ=0 EndX=-131.205 EndY=143.459 EndZ=0
    g123: LineSegment StartX=-131.205 StartY=143.459 StartZ=0 EndX=-125.711 EndY=144.668 EndZ=0
    g124: Circle [constr] CenterX=-129.505 CenterY=148.821 CenterZ=0 NormalX=0 NormalY=0 NormalZ=1 AngleXU=0 Radius=5.625
    g125: LineSegment StartX=-145.063 StartY=153.902 StartZ=0 EndX=-143.334 EndY=159.255 EndZ=0
    g126: LineSegment StartX=-143.334 StartY=159.255 StartZ=0 EndX=-147.105 EndY=163.429 EndZ=0
    g127: LineSegment StartX=-147.105 StartY=163.429 StartZ=0 EndX=-152.605 EndY=162.25 EndZ=0
    g128: LineSegment StartX=-152.605 StartY=162.25 StartZ=0 EndX=-154.334 EndY=156.898 EndZ=0
    g129: LineSegment StartX=-154.334 StartY=156.898 StartZ=0 EndX=-150.564 EndY=152.724 EndZ=0
    g130: LineSegment StartX=-150.564 StartY=152.724 StartZ=0 EndX=-145.063 EndY=153.902 EndZ=0
    g131: Circle [constr] CenterX=-148.834 CenterY=158.076 CenterZ=0 NormalX=0 NormalY=0 NormalZ=1 AngleXU=0 Radius=5.625
    g132: LineSegment StartX=158.769 StartY=2.84e-14 StartZ=0 EndX=-74.2567 EndY=252.476 EndZ=0
    g133: LineSegment StartX=-74.2567 StartY=252.476 StartZ=0 EndX=-98.5872 EndY=278.838 EndZ=0
    g134: LineSegment StartX=158.769 StartY=2.84e-14 StartZ=0 EndX=-126.1 EndY=136.242 EndZ=0
    g135: LineSegment StartX=-126.1 StartY=136.242 StartZ=0 EndX=-158.028 EndY=151.512 EndZ=0
    g136: LineSegment StartX=158.769 StartY=2.84e-14 StartZ=0 EndX=-242.118 EndY=298.813 EndZ=0
    g137: LineSegment [constr] StartX=-133.299 StartY=152.974 StartZ=0 EndX=-124.012 EndY=150.03 EndZ=0
    g138: LineSegment [constr] StartX=-152.605 StartY=162.25 StartZ=0 EndX=-143.334 EndY=159.255 EndZ=0
    g139: GeomPoint [constr] X=-147.977 Y=160.755 Z=0
    g140: GeomPoint [constr] X=-128.663 Y=151.505 Z=0
    g141: LineSegment [constr] StartX=-132.613 StartY=213.906 StartZ=0 EndX=-123.746 EndY=209.869 EndZ=0
    g142: LineSegment [constr] StartX=-115.073 StartY=201.103 StartZ=0 EndX=-106.17 EndY=197.145 EndZ=0
    g143: GeomPoint [constr] X=-110.629 Y=199.127 Z=0
    g144: GeomPoint [constr] X=-128.188 Y=211.891 Z=0
    g145: LineSegment [constr] StartX=-104.95 StartY=265.544 StartZ=0 EndX=-96.6861 EndY=260.383 EndZ=0
    g146: LineSegment [constr] StartX=-89.9472 StartY=249.259 StartZ=0 EndX=-81.6177 EndY=244.205 EndZ=0
    g147: GeomPoint [constr] X=-85.7908 Y=246.738 Z=0
    g148: GeomPoint [constr] X=-100.826 Y=262.969 Z=0
  constraints (276):
    c: Angle(g0,g-1) = 0.628319
    c: PointOnObject(g1,g0)
    c: Coincident(g2,g0)
    c: Vertical(g2)
    c: Coincident(g3,g0)
    c: Horizontal(g3)
    c: Distance(g0) = 500
    c: Coincident(g0,g-3)
    c: PointOnObject(g3,g-3)
    c: PointOnObject(g2,g-3)
    c: PointOnObject(g1,g-3)
    c: Coincident(g27,g0)
    c: PointOnObject(g28,g-3)
    c: Coincident(g25,g0)
    c: PointOnObject(g26,g-3)
    c: InternalAlignment(g5-g8 -> g4) x4
    c: Coincident(g4,g0)
    c: PointOnObject(g3,g4)
    c: Coincident(g4,g28)
    c: Coincident(g4,g26)
    c: PointOnObject(g9,g3)
    c: DistanceX(g3,g9) = 3.6
    c: PointOnObject(g10,g2)
    c: DistanceY(g10,g2) = 3.6
    c: InternalAlignment(g12-g15 -> g11) x4
    c: Coincident(g11,g0)
    c: PointOnObject(g9,g11)
    c: Coincident(g12,g10)
    c: Coincident(g16,g3)
    c: PointOnObject(g16,g-1)
    c: Coincident(g17,g2)
    c: Vertical(g17)
    c: DistanceY(g2,g17) = 3.6
    c: DistanceX(g16,g3) = 3.6
    c: Tangent(g18,g28) = -1.5708
    c: Tangent(g19,g26) = -1.5708
    c: InternalAlignment(g21-g24 -> g20) x4
    c: Coincident(g20,g0)
    c: PointOnObject(g16,g20)
    c: Coincident(g21,g17)
    c: Coincident(g19,g20)
    c: Coincident(g18,g20)
    c: PointOnObject(g11,g26)
    c: PointOnObject(g25,g11)
    c: Tangent(g25,g26) = -1.5708
    c: PointOnObject(g11,g28)
    c: PointOnObject(g27,g11)
    c: Tangent(g27,g28) = -1.5708
    c: Angle(g25,g0) = 0.152716
    c: Angle(g0,g27) = 0.152716
    c: Coincident(g44,g0)
    c: InternalAlignment(g30-g33 -> g29) x4
    c: Coincident(g29,g0)
    c: PointOnObject(g3,g29)
    c: Coincident(g29,g4)
    c: PointOnObject(g31,g-1)
    c: InternalAlignment(g35-g38 -> g34) x4
    c: Coincident(g34,g0)
    c: PointOnObject(g9,g34)
    c: Coincident(g34,g11)
    c: PointOnObject(g36,g-1)
    c: InternalAlignment(g40-g43 -> g39) x4
    c: Coincident(g39,g0)
    c: PointOnObject(g16,g39)
    c: Coincident(g39,g19)
    c: PointOnObject(g41,g-1)
    c: PointOnObject(g29,g45)
    c: PointOnObject(g34,g45)
    c: PointOnObject(g39,g45)
    c: PointOnObject(g45,g39)
    c: PointOnObject(g44,g34)
    c: Tangent(g44,g45) = -1.5708
    c: Angle(g44,g25) = 0.0174533
    c: Coincident(g46,g3)
    c: Coincident(g47,g46)
    c: Symmetric(g47,g46,g46)
    c: PointOnObject(g46,g-1)
    c: DistanceX(g46,g47) = 35
    c: Coincident(g134,g0)
    c: Coincident(g132,g0)
    c: InternalAlignment(g49-g52 -> g48) x4
    c: Coincident(g48,g0)
    c: PointOnObject(g46,g48)
    c: PointOnObject(g50,g-1)
    c: InternalAlignment(g54-g57 -> g53) x4
    c: Coincident(g53,g0)
    c: PointOnObject(g47,g53)
    c: PointOnObject(g55,g-1)
    c: InternalAlignment(g59-g62 -> g58) x4
    c: Coincident(g58,g0)
    c: PointOnObject(g46,g58)
    c: Coincident(g58,g4)
    c: PointOnObject(g60,g-1)
    c: InternalAlignment(g64-g67 -> g63) x4
    c: Coincident(g63,g0)
    c: PointOnObject(g46,g63)
    c: Coincident(g63,g29)
    c: PointOnObject(g65,g-1)
    c: Distance(g58,g4) = 10
    c: Distance(g29,g63) = 10
    c: Coincident(g68,g2)
    c: Vertical(g68)
    c: Coincident(g69,g68)
    c: Symmetric(g69,g68,g68)
    c: DistanceY(g69,g68) = 35
    c: DistanceY(g54,g69) = 0.1
    c: DistanceY(g68,g49) = 0.1
    c: Coincident(g133,g48)
    c: Coincident(g135,g48)
    c: InternalAlignment(g73-g76 -> g72) x4
    c: Coincident(g72,g0)
    c: Coincident(g72,g70)
    c: Coincident(g72,g71)
    c: PointOnObject(g74,g-1)
    c: InternalAlignment(g80-g83 -> g79) x4
    c: Coincident(g79,g0)
    c: PointOnObject(g81,g-1)
    c: Coincident(g79,g77)
    c: Coincident(g79,g78)
    c: PointOnObject(g84,g72)
    c: PointOnObject(g85,g79)
    c: PointOnObject(g86,g72)
    c: PointOnObject(g87,g79)
    c: PointOnObject(g88,g72)
    c: PointOnObject(g89,g79)
    c: Equal(g84,g85)
    c: Equal(g84,g87)
    c: Equal(g84,g86)
    c: Equal(g84,g89)
    c: Equal(g84,g88)
    c: Diameter(g84) = 6
    c: Distance(g88,g72) = 10
    c: Distance(g89,g79) = 10
    c: Distance(g84,g72) = 10
    c: Distance(g85,g79) = 10
    c: PointOnObject(g86,g0)
    c: PointOnObject(g87,g0)
    c: Coincident(g90,g91)
    c: Coincident(g91,g92)
    c: Coincident(g92,g93)
    c: Coincident(g93,g94)
    c: Coincident(g94,g95)
    c: Coincident(g95,g90)
    c: Equal(g90, g91-g95) x5
    c: PointOnObject(g90,g96)
    c: PointOnObject(g91,g96)
    c: PointOnObject(g92,g96)
    c: PointOnObject(g93,g96)
    c: PointOnObject(g94,g96)
    c: PointOnObject(g95,g96)
    c: Coincident(g96,g84)
    c: Coincident(g97,g98)
    c: Coincident(g98,g99)
    c: Coincident(g99,g100)
    c: Coincident(g100,g101)
    c: Coincident(g101,g102)
    c: Coincident(g102,g97)
    c: Equal(g97, g98-g102) x5
    c: PointOnObject(g97,g103)
    c: PointOnObject(g98,g103)
    c: PointOnObject(g99,g103)
    c: PointOnObject(g100,g103)
    c: PointOnObject(g101,g103)
    c: PointOnObject(g102,g103)
    c: Coincident(g103,g85)
    c: Coincident(g104,g105)
    c: Coincident(g105,g106)
    c: Coincident(g106,g107)
    c: Coincident(g107,g108)
    c: Coincident(g108,g109)
    c: Coincident(g109,g104)
    c: Equal(g104, g105-g109) x5
    c: PointOnObject(g104,g110)
    c: PointOnObject(g105,g110)
    c: PointOnObject(g106,g110)
    c: PointOnObject(g107,g110)
    c: PointOnObject(g108,g110)
    c: PointOnObject(g109,g110)
    c: Coincident(g110,g86)
    c: Coincident(g111,g112)
    c: Coincident(g112,g113)
    c: Coincident(g113,g114)
    c: Coincident(g114,g115)
    c: Coincident(g115,g116)
    c: Coincident(g116,g111)
    c: Equal(g111, g112-g116) x5
    c: PointOnObject(g111,g117)
    c: PointOnObject(g112,g117)
    c: PointOnObject(g113,g117)
    c: PointOnObject(g114,g117)
    c: PointOnObject(g115,g117)
    c: PointOnObject(g116,g117)
    c: Coincident(g117,g87)
    c: Coincident(g118,g119)
    c: Coincident(g119,g120)
    c: Coincident(g120,g121)
    c: Coincident(g121,g122)
    c: Coincident(g122,g123)
    c: Coincident(g123,g118)
    c: Equal(g118, g119-g123) x5
    c: PointOnObject(g118,g124)
    c: PointOnObject(g119,g124)
    c: PointOnObject(g120,g124)
    c: PointOnObject(g121,g124)
    c: PointOnObject(g122,g124)
    c: PointOnObject(g123,g124)
    c: Coincident(g124,g88)
    c: Coincident(g125,g126)
    c: Coincident(g126,g127)
    c: Coincident(g127,g128)
    c: Coincident(g128,g129)
    c: Coincident(g129,g130)
    c: Coincident(g130,g125)
    c: Equal(g125, g126-g130) x5
    c: PointOnObject(g125,g131)
    c: PointOnObject(g126,g131)
    c: PointOnObject(g127,g131)
    c: PointOnObject(g128,g131)
    c: PointOnObject(g129,g131)
    c: PointOnObject(g130,g131)
    c: Coincident(g131,g89)
    c: Equal(g96,g103)
    c: Equal(g96,g117)
    c: Equal(g96,g110)
    c: Equal(g96,g131)
    c: Equal(g96,g124)
    c: Diameter(g96) = 11.25
    c: PointOnObject(g53,g133)
    c: PointOnObject(g63,g133)
    c: PointOnObject(g53,g135)
    c: PointOnObject(g58,g135)
    c: Tangent(g134,g135) = -1.5708
    c: Tangent(g132,g133) = -1.5708
    c: PointOnObject(g132,g53)
    c: PointOnObject(g134,g53)
    c: Coincident(g136,g0)
    c: Angle(g136,g3) = 0.640536
    c: Equal(g0,g136)
    c: Coincident(g137,g120)
    c: Coincident(g137,g118)
    c: Coincident(g138,g127)
    c: Coincident(g138,g125)
    c: PointOnObject(g139,g79)
    c: PointOnObject(g139,g138)
    c: Perpendicular(g79,g138,g139) = 1.5708
    c: PointOnObject(g140,g72)
    c: PointOnObject(g140,g137)
    c: Perpendicular(g72,g137,g140) = 1.5708
    c: Coincident(g141,g113)
    c: Coincident(g141,g111)
    c: Coincident(g142,g106)
    c: Coincident(g142,g104)
    c: PointOnObject(g143,g72)
    c: PointOnObject(g143,g142)
    c: Perpendicular(g72,g142,g143) = 1.5708
    c: PointOnObject(g144,g79)
    c: PointOnObject(g144,g141)
    c: Perpendicular(g79,g141,g144) = 1.5708
    c: Coincident(g145,g100)
    c: Coincident(g145,g97)
    c: Coincident(g146,g93)
    c: Coincident(g146,g90)
    c: PointOnObject(g147,g72)
    c: PointOnObject(g147,g146)
    c: Perpendicular(g72,g146,g147) = 1.5708
    c: PointOnObject(g148,g79)
    c: PointOnObject(g148,g145)
    c: Perpendicular(g79,g145,g148) = 1.5708
    c: Distance(g53,g72) = 6.95
    c: PointOnObject(g72,g133)
    c: PointOnObject(g72,g135)
    c: Distance(g72,g53) = 6.95
    c: PointOnObject(g79,g135)
    c: Distance(g79,g48) = 6.95
    c: PointOnObject(g79,g133)
    c: Distance(g79,g48) = 6.95
FEATURE [PartDesign::Body] Body008  label="elipseXZbody"
  AutoGroupSolids = false
  ExportMode = 0
  Group = -> [Sketch011,Binder,Export022,Pad026,Export023,Binder004,Binder007,Boolean,Pad027,Export024,Export025,Pad028,Pad032,Pad033,Pocket001,Sketch012,Fillet,Fillet005,Chamfer,Chamfer003,Export027,Export028,Sketch014,Pipe,Fillet010,Fillet011,Fillet012,Fillet013,Binder008]
  Origin = -> Origin008
  Tip = -> Fillet013
  TreeRank = 339
  _ExportChildren = -> [Sketch011,Binder,Pad026,Binder004,Binder007,Boolean,Pad027,Pad028,Pad032,Pad033,Pocket001,Sketch012,Fillet,Fillet005,Chamfer,Chamfer003,Pipe,Fillet010,Fillet011,Fillet012,Fillet013]
  _GroupVersion = 1
FEATURE [Sketcher::SketchExport] Export021  label="feedsplat"
  Base = -> Sketch007
  BaseRefs = -> Sketch007 [edge8,edge9,edge7]
  MapMode = 5
  Placement = pos=(0,0,-82) rot=(1,0,0;3.14159rad)
  Refs = ;g32.edge8 | ;g33.edge9 | ;g31.edge7
  Support = -> [Pad034]
  SyncPlacement = true
  TreeRank = 298
FEATURE [PartDesign::Pad] Pad025
  AddSubType = 0
  AlongSketchNormal = false
  BaseFeature = -> Pad034
  CheckUpToFaceLimits = true
  ClaimChildren = false
  Direction = (0,0,-1)
  Fit = 0
  FitJoin = 0
  InnerFit = 0
  InnerFitJoin = 0
  InnerTaperAngle = 0
  InnerTaperAngleRev = 0
  Length = 18
  Length2 = 100
  Linearize = true
  NewSolid = false
  Profile = -> Export021
  Suppress = false
  TreeRank = 299
  Type = 0
  _ProfileBasedVersion = 1
  expr: Length = <<measures>>.RockerboxMinFeedHight
FEATURE [Sketcher::SketchExport] Export022  label="elips"
  Base = -> Sketch011
  BaseRefs = -> Sketch011 [edge19,edge29,edge12,edge21,edge20,edge27]
  MapMode = 5
  Placement = pos=(0,0,-15) rot=(1,0,0;3.14159rad)
  Refs = ;g139.edge19 | ;g149.edge29 | ;g132.edge12 | ;g141.edge21 | ;g140.edge20 | ;g147.edge27
  Support = -> [Binder004]
  SyncPlacement = true
  TreeRank = 312
FEATURE [PartDesign::Pad] Pad026
  AddSubType = 0
  AlongSketchNormal = false
  CheckUpToFaceLimits = true
  ClaimChildren = false
  Direction = (0,0,-1)
  Fit = 0
  FitJoin = 0
  InnerFit = 0
  InnerFitJoin = 0
  InnerTaperAngle = 0
  InnerTaperAngleRev = 0
  Length = 200
  Length2 = 100
  Linearize = true
  Midplane = true
  NewSolid = false
  Profile = -> Export022
  Suppress = false
  TreeRank = 313
  Type = 0
  _ProfileBasedVersion = 1
FEATURE [Sketcher::SketchExport] Export023  label="stopper"
  Base = -> Sketch011
  BaseRefs = -> Sketch011 [edge20,edge27,edge35,edge40,edge46]
  MapMode = 5
  Placement = pos=(0,0,-15) rot=(1,0,0;3.14159rad)
  Refs = ;g140.edge20 | ;g147.edge27 | ;g156.edge35 | ;g161.edge40 | ;g168.edge46
  Support = -> [Binder004]
  SyncPlacement = true
  TreeRank = 317
FEATURE [PartDesign::Pad] Pad027
  AddSubType = 0
  AlongSketchNormal = false
  BaseFeature = -> Boolean
  CheckUpToFaceLimits = true
  ClaimChildren = false
  Direction = (0,0,-1)
  Fit = 0
  FitJoin = 0
  InnerFit = 0
  InnerFitJoin = 0
  InnerTaperAngle = 0
  InnerTaperAngleRev = 0
  Length = 20
  Length2 = 100
  Linearize = true
  NewSolid = false
  Profile = -> Export023
  Suppress = false
  TreeRank = 319
  Type = 0
  _ProfileBasedVersion = 1
  expr: Length = <<measures>>.ElipseStopperHeight + <<measures>>.elipsefootthickness
FEATURE [PartDesign::ShapeBinder] ShapeBinder005
  Placement = pos=(0,0,-15) rot=(1,0,0;3.14159rad)
  Support = -> [Sketch011]
  TraceSupport = false
  TreeRank = 324
FEATURE [Sketcher::SketchExport] Export024  label="elipsefeet"
  Base = -> Sketch011
  BaseRefs = -> Sketch011 [edge54,edge136,edge49,edge134,edge86,edge85,edge88,edge87,edge90,edge89]
  Placement = pos=(0,0,-15) rot=(1,0,0;3.14159rad)
  Refs = ;g178.edge54 | ;g287.edge136 | ;g173.edge49 | ;g285.edge134 | ;g235.edge86 | ;g234.edge85 | ;g237.edge88 | ;g236.edge87 | ;g239.edge90 | ;g238.edge89
  SyncPlacement = true
  TreeRank = 325
FEATURE [Sketcher::SketchExport] Export025  label="nutholes"
  Base = -> Sketch011
  BaseRefs = -> Sketch011 [edge91,edge92,edge93,edge94,edge95,edge96,edge98,edge99,edge100,edge101,edge102,edge103,edge105,edge106,edge107,edge108,edge109,edge110,edge112,edge113,edge114,edge115,edge116,edge117,edge119,edge120,edge121,edge122,edge123,edge124,edge126,edge127,edge128,edge129,edge130,edge131]
  MapMode = 5
  Placement = pos=(0,0,-25) rot=(1,0,0;3.14159rad)
  Refs = ;g240.edge91 | ;g241.edge92 | ;g242.edge93 | ;g243.edge94 | ;g244.edge95 | ;g245.edge96 | ;g247.edge98 | ;g248.edge99 | ;g249.edge100 | ;g250.edge101 | ;g251.edge102 | ;g252.edge103 | ;g254.edge105 | ;g255.edge106 | ;g256.edge107 | ;g257.edge108 | ;g258.edge109 | ;g259.edge110 | ;g261.edge112 | ;g262.edge113 | ;g263.edge114 | ;g264.edge115 | ;g265.edge116 | ;g266.edge117 | ;g268.edge119 | ;g269.edge120 | ;g270.edge121 | ;g271.edge122 | ;g272.edge123 | ;g273.edge124 | ;g275.edge126 | ;g276.edge127 | ;g277.edge128 | ;g278.edge129 | ;g279.edge130 | ;g280.edge131
  Support = -> [Pad028]
  SyncPlacement = true
  TreeRank = 326
FEATURE [PartDesign::Pad] Pad028
  AddSubType = 0
  AlongSketchNormal = false
  BaseFeature = -> Pad027
  CheckUpToFaceLimits = true
  ClaimChildren = false
  Direction = (0,0,-1)
  Fit = 0
  FitJoin = 0
  InnerFit = 0
  InnerFitJoin = 0
  InnerTaperAngle = 0
  InnerTaperAngleRev = 0
  Length = 10
  Length2 = 100
  Linearize = true
  NewSolid = false
  Profile = -> Export024
  Suppress = false
  TreeRank = 327
  Type = 0
  _ProfileBasedVersion = 1
  expr: Length = <<measures>>.elipsefootthickness
FEATURE [PartDesign::Pocket] Pocket001
  AddSubType = 1
  BaseFeature = -> Pad033
  CheckUpToFaceLimits = true
  ClaimChildren = false
  Fit = 0
  FitJoin = 0
  InnerFit = 0
  InnerFitJoin = 0
  InnerTaperAngle = 0
  InnerTaperAngleRev = 0
  Length = 4.8
  Length2 = 100
  Linearize = true
  NewSolid = false
  Profile = -> Export025
  Suppress = false
  TreeRank = 328
  Type = 0
  _ProfileBasedVersion = 1
  _Version = 1
  expr: Length = <<measures>>.elipsefeednutpocket
FEATURE [Sketcher::SketchObject] Sketch012  label="support"
  Exports = -> [Export027,Export028]
  ExternalGeometry = -> [Sketch011]
  FullyConstrained = true
  MapMode = 5
  Placement = pos=(0,0,-15) rot=(1,0,0;3.14159rad)
  Support = -> [Binder004]
  TreeRank = 333
  sketch-geometry (16):
    g0: LineSegment StartX=-132.858 StartY=161.298 StartZ=0 EndX=-126.209 EndY=159.027 EndZ=0
    g1: LineSegment StartX=-131.244 StartY=166.031 StartZ=0 EndX=-124.593 EndY=163.759 EndZ=0
    g2: LineSegment StartX=-144.677 StartY=170.61 StartZ=0 EndX=-138.035 EndY=168.346 EndZ=0
    g3: LineSegment StartX=-146.291 StartY=165.878 StartZ=0 EndX=-139.65 EndY=163.614 EndZ=0
    g4: LineSegment StartX=-124.593 StartY=163.759 StartZ=0 EndX=-126.209 EndY=159.027 EndZ=0
    g5: LineSegment StartX=-144.677 StartY=170.61 StartZ=0 EndX=-146.291 EndY=165.878 EndZ=0
    g6: LineSegment StartX=-138.035 StartY=168.346 StartZ=0 EndX=-131.244 EndY=166.031 EndZ=0
    g7: LineSegment StartX=-139.65 StartY=163.614 StartZ=0 EndX=-132.858 EndY=161.298 EndZ=0
    g8: LineSegment StartX=-136.425 StartY=192.665 StartZ=0 EndX=-129.92 EndY=190.008 EndZ=0
    g9: LineSegment StartX=-129.92 StartY=190.008 StartZ=0 EndX=-123.284 EndY=187.296 EndZ=0
    g10: LineSegment StartX=-123.284 StartY=187.296 StartZ=0 EndX=-116.768 EndY=184.634 EndZ=0
    g11: LineSegment StartX=-134.534 StartY=197.294 StartZ=0 EndX=-128.027 EndY=194.635 EndZ=0
    g12: LineSegment StartX=-128.027 StartY=194.635 StartZ=0 EndX=-121.392 EndY=191.925 EndZ=0
    g13: LineSegment StartX=-121.392 StartY=191.925 StartZ=0 EndX=-114.873 EndY=189.261 EndZ=0
    g14: LineSegment StartX=-134.534 StartY=197.294 StartZ=0 EndX=-136.425 EndY=192.665 EndZ=0
    g15: LineSegment StartX=-114.873 StartY=189.261 StartZ=0 EndX=-116.768 EndY=184.634 EndZ=0
  constraints (45):
    c: PointOnObject(g0,g-4)
    c: PointOnObject(g0,g-3)
    c: PointOnObject(g2,g-5)
    c: PointOnObject(g2,g-6)
    c: PointOnObject(g3,g-5)
    c: PointOnObject(g3,g-6)
    c: PointOnObject(g1,g-4)
    c: PointOnObject(g1,g-3)
    c: Distance(g0,g1) = 5
    c: Distance(g0,g1) = 5
    c: Distance(g2,g3) = 5
    c: Distance(g2,g3) = 5
    c: Coincident(g4,g1)
    c: Coincident(g4,g0)
    c: Coincident(g5,g2)
    c: Coincident(g5,g3)
    c: Perpendicular(g4,g1)
    c: Perpendicular(g2,g5)
    c: Distance(g-4,g0) = 10
    c: Coincident(g6,g1)
    c: Coincident(g7,g3)
    c: Coincident(g7,g0)
    c: Tangent(g6,g2) = -1.5708
    c: PointOnObject(g8,g-5)
    c: PointOnObject(g8,g-6)
    c: Coincident(g9,g8)
    c: PointOnObject(g9,g-4)
    c: Coincident(g10,g9)
    c: PointOnObject(g10,g-3)
    c: PointOnObject(g11,g-5)
    c: PointOnObject(g11,g-6)
    c: PointOnObject(g12,g-4)
    c: PointOnObject(g13,g-3)
    c: Coincident(g14,g11)
    c: Coincident(g15,g13)
    c: Coincident(g15,g10)
    c: Distance(g15) = 5
    c: Distance(g9,g12) = 5
    c: Distance(g11,g8) = 5
    c: Distance(g14) = 5
    c: Coincident(g14,g8)
    c: Tangent(g12,g11) = -1.5708
    c: Tangent(g13,g12) = -1.5708
    c: Perpendicular(g11,g14)
    c: Distance(g10,g-3) = 48
FEATURE [PartDesign::Fillet] Fillet
  AddSubType = 0
  Base = -> Pocket001 [Edge117,Edge114,Edge115,Edge119]
  BaseFeature = -> Pocket001
  NewSolid = false
  Radius = 4
  SupportTransform = false
  Suppress = false
  TreeRank = 336
  expr: Radius = <<measures>>.elipsefootroundness
FEATURE [PartDesign::Fillet] Fillet005
  AddSubType = 0
  Base = -> Fillet [Edge3,Edge1,Edge2,Edge4,Edge6,Edge8,Edge7,Edge5]
  BaseFeature = -> Fillet
  NewSolid = false
  Radius = 1
  SupportTransform = false
  Suppress = false
  TreeRank = 337
FEATURE [Part::Mirroring] Part__Mirroring  label="Roller (Mirror #1)"
  Base = (0,0,0)
  Normal = (0,1,0)
  Source = -> Body006
  TreeRank = 342
FEATURE [Part::Mirroring] Part__Mirroring001  label="elipseXZbody (Mirror #2)"
  Base = (0,0,0)
  Normal = (0,1,0)
  Source = -> Body008
  TreeRank = 343
FEATURE [PartDesign::Boolean] Boolean
  BaseFeature = -> Pad026
  ExportMode = 0
  Group = -> [Reference,Reference001]
  NewSolid = false
  Refine = true
  Suppress = false
  TreeRank = 366
  Type = 2
  _ExportChildren = -> [Reference,Reference001]
  _GroupVersion = 1
FEATURE [Sketcher::SketchExport] Export027  label="supportlarge"
  Base = -> Sketch012
  BaseRefs = -> Sketch012 [edge1,edge5,edge2,edge7,edge3,edge6,edge4,edge8]
  MapMode = 5
  Placement = pos=(0,0,-15) rot=(1,0,0;3.14159rad)
  Refs = ;g5.edge1 | ;g9.edge5 | ;g6.edge2 | ;g11.edge7 | ;g7.edge3 | ;g10.edge6 | ;g8.edge4 | ;g12.edge8
  Support = -> [Binder004]
  SyncPlacement = true
  TreeRank = 367
FEATURE [Sketcher::SketchExport] Export028  label="supportsmall"
  Base = -> Sketch012
  BaseRefs = -> Sketch012 [edge15,edge12,edge9,edge13,edge10,edge11,edge14,edge16]
  MapMode = 5
  Placement = pos=(0,0,-15) rot=(1,0,0;3.14159rad)
  Refs = ;g19.edge15 | ;g16.edge12 | ;g13.edge9 | ;g17.edge13 | ;g14.edge10 | ;g15.edge11 | ;g18.edge14 | ;g20.edge16
  Support = -> [Binder004]
  SyncPlacement = true
  TreeRank = 368
FEATURE [PartDesign::Pad] Pad032
  AddSubType = 0
  AlongSketchNormal = false
  BaseFeature = -> Pad028
  CheckUpToFaceLimits = true
  ClaimChildren = false
  Direction = (0,0,-1)
  Fit = 0
  FitJoin = 0
  InnerFit = 0
  InnerFitJoin = 0
  InnerTaperAngle = 0
  InnerTaperAngleRev = 0
  Length = 40
  Length2 = 100
  Linearize = true
  NewSolid = false
  Profile = -> Export027
  Refine = true
  Suppress = false
  TreeRank = 369
  Type = 0
  _ProfileBasedVersion = 1
FEATURE [PartDesign::Pad] Pad033
  AddSubType = 0
  AlongSketchNormal = false
  BaseFeature = -> Pad032
  CheckUpToFaceLimits = true
  ClaimChildren = false
  Direction = (0,0,-1)
  Fit = 0
  FitJoin = 0
  InnerFit = 0
  InnerFitJoin = 0
  InnerTaperAngle = 0
  InnerTaperAngleRev = 0
  Length = 30
  Length2 = 100
  Linearize = true
  NewSolid = false
  Profile = -> Export028
  Refine = true
  Suppress = false
  TreeRank = 370
  Type = 0
  _ProfileBasedVersion = 1
FEATURE [PartDesign::Chamfer] Chamfer
  AddSubType = 0
  Angle = 45
  Base = -> Fillet005 [Edge141,Edge146]
  BaseFeature = -> Fillet005
  ChamferType = 1
  FlipDirection = false
  NewSolid = false
  Refine = true
  Size = 26
  Size2 = 4
  SupportTransform = false
  Suppress = false
  TreeRank = 371
FEATURE [PartDesign::Chamfer] Chamfer003
  AddSubType = 0
  Angle = 45
  Base = -> Chamfer [Edge156,Edge161]
  BaseFeature = -> Chamfer
  ChamferType = 1
  FlipDirection = false
  NewSolid = false
  Refine = true
  Size = 16
  Size2 = 4
  SupportTransform = false
  Suppress = false
  TreeRank = 372
FEATURE [Sketcher::SketchObject] Sketch014  label="profile"
  ExternalGeometry = -> [Chamfer003]
  FullyConstrained = true
  MapMode = 5
  Placement = pos=(33.2858,-64.6283,-1.5e-15) rot=(-0.16893,0.696944,0.696944;3.47629rad)
  Support = -> [Chamfer003]
  TreeRank = 373
  sketch-geometry (6):
    g0: LineSegment StartX=190.349 StartY=-61.8693 StartZ=0 EndX=197.634 EndY=-61.7823 EndZ=0
    g1: LineSegment StartX=197.634 StartY=-61.7823 StartZ=0 EndX=197.634 EndY=-61.8823 EndZ=0
    g2: LineSegment StartX=190.349 StartY=-61.8693 StartZ=0 EndX=190.349 EndY=-61.9693 EndZ=0
    g3: LineSegment StartX=190.349 StartY=-61.9693 StartZ=0 EndX=192.042 EndY=-62.2678 EndZ=0
    g4: LineSegment StartX=197.634 StartY=-61.8823 StartZ=0 EndX=195.941 EndY=-62.1808 EndZ=0
    g5: ArcOfCircle CenterX=193.991 CenterY=-62.2243 CenterZ=0 NormalX=0 NormalY=0 NormalZ=1 AngleXU=0 Radius=1.95 StartAngle=3.1639 EndAngle=6.30549
  constraints (19):
    c: Coincident(g1,g0)
    c: Coincident(g2,g0)
    c: Coincident(g3,g2)
    c: Coincident(g4,g1)
    c: Coincident(g5,g3)
    c: Coincident(g5,g4)
    c: Diameter(g5) = 3.9
    c: Symmetric(g4,g3,g5)
    c: Equal(g3,g4)
    c: Angle(g3,g2) = 1.74533
    c: Angle(g1,g4) = 1.74533
    c: Distance(g2) = 0.1
    c: DistanceY(g1,g0) = 0.1
    c: Parallel(g2,g-6)
    c: Parallel(g1,g-3)
    c: PointOnObject(g0,g-3)
    c: PointOnObject(g0,g-6)
    c: Distance(g-6,g0) = 0.05
    c: Distance(g-4,g0) = 0.05
FEATURE [Sketcher::SketchExport] Export029  label="roller"
  Base = -> Sketch009
  BaseRefs = -> Sketch009 [edge16,edge12,edge18,edge17,edge13,edge14,edge11]
  MapMode = 5
  Placement = pos=(0,0,-57) rot=(0,0,1;0rad)
  Refs = ;g62.edge16 | ;g17.edge12 | ;g66.edge18 | ;g65.edge17 | ;g26.edge13 | ;g27.edge14 | ;g16.edge11
  Support = -> [DatumPlane]
  SyncPlacement = true
  TreeRank = 376
FEATURE [PartDesign::Revolution] Revolution001
  AddSubType = 0
  Angle = 360
  Axis = (-0.910558,-0.413382,0)
  Base = (-115.61,-205.444,-57)
  BaseFeature = -> Pad021
  ClaimChildren = false
  Fit = 0
  FitJoin = 0
  InnerFit = 0
  InnerFitJoin = 0
  Linearize = true
  NewSolid = false
  Profile = -> Export029
  ReferenceAxis = -> Export029 [Edge7]
  Refine = true
  Suppress = false
  TreeRank = 377
  _ProfileBasedVersion = 1
FEATURE [PartDesign::Fillet] Fillet006
  AddSubType = 0
  Base = -> Revolution001 [Edge11,Edge13,Edge15,Edge16]
  BaseFeature = -> Revolution001
  NewSolid = false
  Radius = 9
  Refine = true
  SupportTransform = false
  Suppress = false
  TreeRank = 378
FEATURE [PartDesign::AdditivePipe] Pipe
  AddSubType = 0
  AuxilleryCurvelinear = true
  AuxillerySpineTangent = false
  BaseFeature = -> Chamfer003
  Binormal = (0,0,0)
  ClaimChildren = false
  Fit = 0
  FitJoin = 0
  InnerFit = 0
  InnerFitJoin = 0
  Linearize = true
  Mode = 0
  NewSolid = false
  Profile = -> Sketch014
  Refine = true
  Spine = -> Binder008
  SpineTangent = false
  Suppress = false
  Transformation = 0
  Transition = 1
  TreeRank = 379
  _ProfileBasedVersion = 2
FEATURE [TechDraw::DrawPage] Page  label="CuttingAndDrillingFirst"
  KeepUpdated = true
  NextBalloonIndex = 1
  ProjectionType = 0
  Template = -> Template
  TreeRank = 383
  Views = -> [ProjGroup,Dimension,Dimension008,DimExtent,ProjGroup004,DimExtent001,Dimension009,Dimension010,Dimension011,Annotation,Dimension012]
FEATURE [Sketcher::SketchExport] Export030  label="platbot"
  Base = -> Sketch007
  BaseRefs = -> Sketch007 [edge10,edge2,ExternalEdge1,ExternalEdge2,ExternalEdge3,ExternalEdge4,ExternalEdge5,edge12,edge14,edge13,edge11,edge1]
  MapMode = 5
  Placement = pos=(0,0,-67) rot=(1,0,0;3.14159rad)
  Refs = ;g34.edge10 | ;g23.edge2 | ;e13.ExternalEdge1 | ;e14.ExternalEdge2 | ;e15.ExternalEdge3 | ;e16.ExternalEdge4 | ;e17.ExternalEdge5 | ;g36.edge12 | ;g38.edge14 | ;g37.edge13 | ;g35.edge11 | ;g22.edge1
  Support = -> [Binder001]
  SyncPlacement = true
  TreeRank = 387
FEATURE [PartDesign::Pad] Pad034
  AddSubType = 0
  AlongSketchNormal = false
  CheckUpToFaceLimits = true
  ClaimChildren = false
  Direction = (0,0,-1)
  Fit = 0
  FitJoin = 0
  InnerFit = 0
  InnerFitJoin = 0
  InnerTaperAngle = 0
  InnerTaperAngleRev = 0
  Length = 15
  Length2 = 100
  Linearize = true
  NewSolid = false
  Profile = -> Export030
  Refine = true
  Suppress = false
  TreeRank = 388
  Type = 0
  _ProfileBasedVersion = 1
  expr: Length = <<measures>>.plattformthickness
FEATURE [Sketcher::SketchExport] Export032  label="bearingcir"
  Base = -> Sketch006
  BaseRefs = -> Sketch006 [edge12]
  Placement = pos=(0,0,-15) rot=(1,0,0;3.14159rad)
  Refs = ;g26.edge12
  Support = -> [Pad006]
  SyncPlacement = true
  TreeRank = 404
FEATURE [Sketcher::SketchExport] Export033  label="bearingholes"
  Base = -> Sketch006
  BaseRefs = -> Sketch006 [edge3,edge6,edge5,edge4,edge8,edge9,edge10,edge7,edge11]
  Placement = pos=(0,0,-15) rot=(1,0,0;3.14159rad)
  Refs = ;g17.edge3 | ;g20.edge6 | ;g19.edge5 | ;g18.edge4 | ;g22.edge8 | ;g23.edge9 | ;g24.edge10 | ;g21.edge7 | ;g25.edge11
  Support = -> [Pad006]
  SyncPlacement = true
  TreeRank = 405
FEATURE [Sketcher::SketchExport] Export034  label="bearingout"
  Base = -> Sketch006
  BaseRefs = -> Sketch006 [edge16,edge15,edge22,edge21,edge17,edge18,edge20,edge19]
  Placement = pos=(0,0,-15) rot=(1,0,0;3.14159rad)
  Refs = ;g30.edge16 | ;g29.edge15 | ;g36.edge22 | ;g35.edge21 | ;g31.edge17 | ;g32.edge18 | ;g34.edge20 | ;g33.edge19
  Support = -> [Pad006]
  SyncPlacement = true
  TreeRank = 406
FEATURE [PartDesign::Pad] Pad035
  AddSubType = 0
  AlongSketchNormal = false
  CheckUpToFaceLimits = true
  ClaimChildren = false
  Direction = (0,0,-1)
  Fit = 0
  FitJoin = 0
  InnerFit = 0
  InnerFitJoin = 0
  InnerTaperAngle = 0
  InnerTaperAngleRev = 0
  Length = 13
  Length2 = 100
  Linearize = true
  NewSolid = false
  Profile = -> Export032
  Refine = true
  Suppress = false
  TreeRank = 407
  Type = 0
  _ProfileBasedVersion = 1
FEATURE [PartDesign::Pad] Pad036
  AddSubType = 0
  AlongSketchNormal = false
  BaseFeature = -> Pad035
  CheckUpToFaceLimits = true
  ClaimChildren = false
  Direction = (0,0,-1)
  Fit = 0
  FitJoin = 0
  InnerFit = 0
  InnerFitJoin = 0
  InnerTaperAngle = 0
  InnerTaperAngleRev = 0
  Length = 7
  Length2 = 100
  Linearize = true
  NewSolid = false
  Profile = -> Export034
  Refine = true
  Suppress = false
  TreeRank = 408
  Type = 0
  _ProfileBasedVersion = 1
FEATURE [PartDesign::Pocket] Pocket
  AddSubType = 1
  BaseFeature = -> Pad036
  CheckUpToFaceLimits = true
  ClaimChildren = false
  Fit = 0
  FitJoin = 0
  InnerFit = 0
  InnerFitJoin = 0
  InnerTaperAngle = 0
  InnerTaperAngleRev = 0
  Length = 20
  Length2 = 100
  Linearize = true
  NewSolid = false
  Profile = -> Export033
  Refine = true
  Reversed = true
  Suppress = false
  TreeRank = 409
  Type = 0
  _ProfileBasedVersion = 1
  _Version = 1
FEATURE [PartDesign::Fillet] Fillet008
  AddSubType = 0
  Base = -> Pocket [Edge33,Edge35,Edge37,Edge31,Edge29,Edge42,Edge41,Edge39]
  BaseFeature = -> Pocket
  NewSolid = false
  Radius = 1
  Refine = true
  SupportTransform = false
  Suppress = false
  TreeRank = 410
FEATURE [PartDesign::Fillet] Fillet009
  AddSubType = 0
  Base = -> Fillet008 [Edge77]
  BaseFeature = -> Fillet008
  NewSolid = false
  Radius = 2
  Refine = true
  SupportTransform = false
  Suppress = false
  TreeRank = 411
FEATURE [PartDesign::Pad] Pad037
  AddSubType = 0
  AlongSketchNormal = false
  BaseFeature = -> Fillet009
  CheckUpToFaceLimits = true
  ClaimChildren = false
  Direction = (0,0,-1)
  Fit = 0
  FitJoin = 0
  InnerFit = 0
  InnerFitJoin = 0
  InnerTaperAngle = 0
  InnerTaperAngleRev = 0
  Length = 52
  Length2 = 100
  Linearize = true
  NewSolid = false
  Profile = -> Export009
  Refine = true
  Suppress = false
  TreeRank = 412
  Type = 0
  _ProfileBasedVersion = 1
  expr: Length = <<measures>>.platformgap
FEATURE [TechDraw::DrawPage] Page001  label="CuttingAndDrillingFeeds"
  KeepUpdated = true
  NextBalloonIndex = 1
  ProjectionType = 0
  Template = -> Template001
  TreeRank = 399
  Views = -> [ProjGroup002,Dimension006,Dimension007]
FEATURE [TechDraw::DrawProjGroup] ProjGroup002
  Anchor = -> ProjItem002
  AutoDistribute = true
  LockPosition = false
  ProjectionType = 0
  Rotation = 0
  ScaleType = 2
  Source = -> [Body004]
  TreeRank = 418
  Views = -> [ProjItem002]
  X = 594.5
  Y = 420.5
  spacingX = 15
  spacingY = 15
FEATURE [TechDraw::DrawProjGroupItem] ProjItem002  label="Front002"
  CoarseView = false
  Direction = (0,-2e-16,-1)
  Focus = 100
  HardHidden = false
  IsoCount = 0
  IsoHidden = false
  IsoVisible = false
  LockPosition = true
  Perspective = false
  Rotation = 0
  RotationVector = (0,-1,0)
  ScaleType = 2
  SeamHidden = false
  SeamVisible = true
  SmoothHidden = false
  SmoothVisible = true
  Source = -> [Body004,Box001]
  TreeRank = 417
  Type = 0
  X = 0
  XDirection = (0,1,-2e-16)
  Y = 0
FEATURE [TechDraw::DrawViewDimension] Dimension006
  Arbitrary = false
  ArbitraryTolerances = false
  EqualTolerance = true
  FormatSpec = %.2f
  FormatSpecOverTolerance = %+.2f
  FormatSpecUnderTolerance = %+.2f
  Inverted = false
  LockPosition = false
  MeasureType = 1
  OverTolerance = 0
  References2D = -> [ProjItem002]
  Rotation = 0
  ScaleType = 0
  TheoreticalExact = false
  TreeRank = 419
  Type = 2
  UnderTolerance = 0
  X = 115.601
  Y = -53.5061
FEATURE [TechDraw::DrawViewDimension] Dimension007
  Arbitrary = false
  ArbitraryTolerances = false
  EqualTolerance = true
  FormatSpec = %.2f
  FormatSpecOverTolerance = %+.2f
  FormatSpecUnderTolerance = %+.2f
  Inverted = false
  LockPosition = false
  MeasureType = 1
  OverTolerance = 0
  References2D = -> [ProjItem002]
  Rotation = 0
  ScaleType = 0
  TheoreticalExact = false
  TreeRank = 420
  Type = 1
  UnderTolerance = 0
  X = 1.29635
  Y = -207.742
FEATURE [PartDesign::Fillet] Fillet010
  AddSubType = 0
  Base = -> Pipe [Edge20,Edge50,Edge52,Edge54,Edge16,Edge21,Edge14,Edge64,Edge5,Edge59,Edge63,Edge61,Edge60,Edge58,Edge57,Edge56,Edge55,Edge53,Edge51,Edge49,Edge3,Edge7,Edge15,Edge19,Edge18,Edge17,Edge159,Edge158,Edge157,Edge156,Edge155,Edge154]
  BaseFeature = -> Pipe
  NewSolid = false
  Radius = 0.5
  Refine = true
  SupportTransform = false
  Suppress = false
  TreeRank = 421
FEATURE [PartDesign::Fillet] Fillet011
  AddSubType = 0
  Base = -> Fillet010 [Face94]
  BaseFeature = -> Fillet010
  NewSolid = false
  Radius = 1
  Refine = true
  SupportTransform = false
  Suppress = false
  TreeRank = 422
FEATURE [PartDesign::Fillet] Fillet012
  AddSubType = 0
  Base = -> Fillet011 [Edge23,Edge126]
  BaseFeature = -> Fillet011
  NewSolid = false
  Radius = 0.5
  Refine = true
  SupportTransform = false
  Suppress = false
  TreeRank = 423
FEATURE [PartDesign::Fillet] Fillet013
  AddSubType = 0
  Base = -> Fillet012 [Edge380,Edge337,Edge344,Edge336,Edge341,Edge323,Edge324,Edge379,Edge331,Edge328,Edge162,Edge169,Edge166,Edge167,Edge163,Edge141,Edge140,Edge138,Edge132,Edge130]
  BaseFeature = -> Fillet012
  NewSolid = false
  Radius = 0.5
  Refine = true
  SupportTransform = false
  Suppress = false
  TreeRank = 424
FEATURE [TechDraw::DrawProjGroup] ProjGroup
  Anchor = -> ProjItem
  AutoDistribute = true
  LockPosition = false
  ProjectionType = 0
  Rotation = 0
  ScaleType = 2
  Source = -> [Box,Box001,Part__Mirroring001,Body008,Body003]
  TreeRank = 427
  Views = -> [ProjItem]
  X = 340.08
  Y = 462.903
  spacingX = 15
  spacingY = 15
FEATURE [TechDraw::DrawProjGroupItem] ProjItem  label="Front"
  CoarseView = false
  Direction = (0,0,-1)
  Focus = 100
  HardHidden = false
  IsoCount = 0
  IsoHidden = false
  IsoVisible = false
  LockPosition = true
  Perspective = false
  Rotation = 0
  RotationVector = (0,-1,0)
  ScaleType = 2
  SeamHidden = false
  SeamVisible = true
  SmoothHidden = false
  SmoothVisible = true
  Source = -> [Box,Box001,Part__Mirroring001,Body008,Body003]
  TreeRank = 426
  Type = 0
  X = 0
  XDirection = (0,-1,0)
  Y = 0
FEATURE [TechDraw::DrawViewDimension] Dimension
  Arbitrary = false
  ArbitraryTolerances = false
  EqualTolerance = true
  FormatSpec = %.2f
  FormatSpecOverTolerance = %+.2f
  FormatSpecUnderTolerance = %+.2f
  Inverted = false
  LockPosition = false
  MeasureType = 1
  OverTolerance = 0
  References2D = -> [ProjItem]
  Rotation = 0
  ScaleType = 0
  TheoreticalExact = false
  TreeRank = 428
  Type = 2
  UnderTolerance = 0
  X = 119.201
  Y = 49.488
FEATURE [TechDraw::DrawViewDimension] Dimension008
  Arbitrary = false
  ArbitraryTolerances = false
  EqualTolerance = true
  FormatSpec = %.2f
  FormatSpecOverTolerance = %+.2f
  FormatSpecUnderTolerance = %+.2f
  Inverted = false
  LockPosition = false
  MeasureType = 1
  OverTolerance = 0
  References2D = -> [ProjItem]
  Rotation = 0
  ScaleType = 0
  TheoreticalExact = false
  TreeRank = 429
  Type = 1
  UnderTolerance = 0
  X = 0.94672
  Y = -102.799
FEATURE [TechDraw::DrawViewDimExtent] DimExtent
  Arbitrary = false
  ArbitraryTolerances = false
  CosmeticTags = 0c86164e-b992-46f0-90af-b0427da2ad0d | 4116bbcb-3ee0-4115-a3bc-487646d43aa5
  DirExtent = 1
  EqualTolerance = true
  FormatSpec = %.2f
  FormatSpecOverTolerance = %+.2f
  FormatSpecUnderTolerance = %+.2f
  Inverted = false
  LockPosition = false
  MeasureType = 1
  OverTolerance = 0
  References2D = -> [ProjItem]
  Rotation = 0
  ScaleType = 0
  Source = -> [ProjItem]
  TheoreticalExact = false
  TreeRank = 430
  Type = 2
  UnderTolerance = 0
  X = -34.4078
  Y = 1.07524
FEATURE [TechDraw::DrawProjGroup] ProjGroup004
  Anchor = -> ProjItem004
  AutoDistribute = true
  LockPosition = false
  ProjectionType = 0
  Rotation = 0
  ScaleType = 2
  Source = -> [Body004,Binder001,Part__Mirroring,Body006,Box,Box001]
  TreeRank = 436
  Views = -> [ProjItem004]
  X = 710.295
  Y = 463.436
  spacingX = 15
  spacingY = 15
FEATURE [TechDraw::DrawProjGroupItem] ProjItem004  label="Front004"
  CoarseView = false
  Direction = (0,0,1)
  Focus = 100
  HardHidden = false
  IsoCount = 0
  IsoHidden = false
  IsoVisible = false
  LockPosition = true
  Perspective = false
  Rotation = 0
  RotationVector = (0,1,0)
  ScaleType = 2
  SeamHidden = false
  SeamVisible = true
  SmoothHidden = false
  SmoothVisible = true
  Source = -> [Body004,Binder001,Part__Mirroring,Body006,Box,Box001]
  TreeRank = 435
  Type = 0
  X = 0
  XDirection = (-1e-16,-1,0)
  Y = 0
FEATURE [TechDraw::DrawViewDimExtent] DimExtent001
  Arbitrary = false
  ArbitraryTolerances = false
  CosmeticTags = 62a62827-16e6-4395-9f08-818e34e1cbe7 | 41ec334b-eab6-4c16-9df5-482181a0e0cb
  DirExtent = 1
  EqualTolerance = true
  FormatSpec = %.2f
  FormatSpecOverTolerance = %+.2f
  FormatSpecUnderTolerance = %+.2f
  Inverted = false
  LockPosition = false
  MeasureType = 1
  OverTolerance = 0
  References2D = -> [ProjItem004]
  Rotation = 0
  ScaleType = 0
  Source = -> [ProjItem004]
  TheoreticalExact = false
  TreeRank = 437
  Type = 2
  UnderTolerance = 0
  X = -43.8168
  Y = 7.06723
FEATURE [TechDraw::DrawViewDimension] Dimension009
  Arbitrary = false
  ArbitraryTolerances = false
  EqualTolerance = true
  FormatSpec = ⌀%.2f
  FormatSpecOverTolerance = %+.2f
  FormatSpecUnderTolerance = %+.2f
  Inverted = false
  LockPosition = false
  MeasureType = 1
  OverTolerance = 0
  References2D = -> [ProjItem]
  Rotation = 0
  ScaleType = 0
  TheoreticalExact = false
  TreeRank = 438
  Type = 5
  UnderTolerance = 0
  X = 20.4296
  Y = -191.393
FEATURE [TechDraw::DrawViewDimension] Dimension010
  Arbitrary = false
  ArbitraryTolerances = false
  EqualTolerance = true
  FormatSpec = %.2f
  FormatSpecOverTolerance = %+.2f
  FormatSpecUnderTolerance = %+.2f
  Inverted = false
  LockPosition = false
  MeasureType = 1
  OverTolerance = 0
  References2D = -> [ProjItem004]
  Rotation = 0
  ScaleType = 0
  TheoreticalExact = false
  TreeRank = 439
  Type = 2
  UnderTolerance = 0
  X = 111.544
  Y = -53.9641
FEATURE [TechDraw::DrawViewDimension] Dimension011
  Arbitrary = false
  ArbitraryTolerances = false
  EqualTolerance = true
  FormatSpec = %.2f
  FormatSpecOverTolerance = %+.2f
  FormatSpecUnderTolerance = %+.2f
  Inverted = false
  LockPosition = false
  MeasureType = 1
  OverTolerance = 0
  References2D = -> [ProjItem004]
  Rotation = 0
  ScaleType = 0
  TheoreticalExact = false
  TreeRank = 440
  Type = 1
  UnderTolerance = 0
  X = -1.42e-14
  Y = -207.372
FEATURE [TechDraw::DrawViewDimension] Dimension012
  Arbitrary = false
  ArbitraryTolerances = false
  EqualTolerance = true
  FormatSpec = %.2f
  FormatSpecOverTolerance = %+.2f
  FormatSpecUnderTolerance = %+.2f
  Inverted = false
  LockPosition = false
  MeasureType = 1
  OverTolerance = 0
  References2D = -> [ProjItem]
  Rotation = 0
  ScaleType = 0
  TheoreticalExact = false
  TreeRank = 442
  Type = 1
  UnderTolerance = 0
  X = 2.27e-14
  Y = -241.392
FEATURE [PartDesign::Body] Body010  label="Gear"
  AutoGroupSolids = false
  ExportMode = 0
  Group = -> [Sketch016,DatumPlane003,Import013,Binder010,Sketch018,Import014,Export036,Export037,Sketch019,Binder011,Sketch020,Pad038,Pocket002,Export038,Pad039,Fillet015,Pocket003,Pocket004,Fillet014,Fillet016,Chamfer004,Chamfer005]
  Origin = -> Origin010
  Tip = -> Chamfer005
  TreeRank = 453
  _ExportChildren = -> [Sketch016,DatumPlane003,Import013,Binder010,Import014,Sketch019,Binder011,Pad038,Pocket002,Pad039,Fillet015,Pocket003,Pocket004,Fillet014,Fillet016,Chamfer004,Chamfer005]
  _GroupVersion = 1
FEATURE [Sketcher::SketchObject] Sketch016  label="GearFeed"
  Exports = -> [Export036,Export037,Export038]
  ExternalGeometry = -> [Pocket002]
  FullyConstrained = true
  MapMode = 5
  Placement = pos=(0,0,-15) rot=(1,0,0;3.14159rad)
  Support = -> [Binder010]
  TreeRank = 464
  expr: Constraints[68] = <<measures>>.elipsefeednutsizeradius
  expr: Constraints[85] = <<measures>>.elipsescrewholedia
  sketch-geometry (42):
    g0: LineSegment StartX=-49.7013 StartY=70 StartZ=0 EndX=-74.7013 EndY=70 EndZ=0
    g1: LineSegment StartX=-74.7013 StartY=-70 StartZ=0 EndX=-49.7013 EndY=-70 EndZ=0
    g2: LineSegment StartX=-49.7013 StartY=-70 StartZ=0 EndX=-49.7013 EndY=70 EndZ=0
    g3: LineSegment StartX=-70.1853 StartY=-64.2517 StartZ=0 EndX=-67.1419 EndY=-68.0679 EndZ=0
    g4: LineSegment StartX=-67.1419 StartY=-68.0679 StartZ=0 EndX=-62.2607 EndY=-68.0679 EndZ=0
    g5: LineSegment StartX=-62.2607 StartY=-68.0679 StartZ=0 EndX=-59.2174 EndY=-64.2517 EndZ=0
    g6: LineSegment StartX=-59.2174 StartY=-64.2517 StartZ=0 EndX=-60.3035 EndY=-59.4929 EndZ=0
    g7: LineSegment StartX=-60.3035 StartY=-59.4929 StartZ=0 EndX=-64.7013 EndY=-57.375 EndZ=0
    g8: LineSegment StartX=-64.7013 StartY=-57.375 StartZ=0 EndX=-69.0991 EndY=-59.4929 EndZ=0
    g9: LineSegment StartX=-69.0991 StartY=-59.4929 StartZ=0 EndX=-70.1853 EndY=-64.2517 EndZ=0
    g10: Circle [constr] CenterX=-64.7013 CenterY=-63 CenterZ=0 NormalX=0 NormalY=0 NormalZ=1 AngleXU=0 Radius=5.625
    g11: LineSegment StartX=-60.953 StartY=19.516 StartZ=0 EndX=-56.1942 EndY=20.6022 EndZ=0
    g12: LineSegment StartX=-56.1942 StartY=20.6022 StartZ=0 EndX=-54.0763 EndY=25 EndZ=0
    g13: LineSegment StartX=-54.0763 StartY=25 StartZ=0 EndX=-56.1942 EndY=29.3978 EndZ=0
    g14: LineSegment StartX=-56.1942 StartY=29.3978 StartZ=0 EndX=-60.953 EndY=30.484 EndZ=0
    g15: LineSegment StartX=-60.953 StartY=30.484 StartZ=0 EndX=-64.7693 EndY=27.4406 EndZ=0
    g16: LineSegment StartX=-64.7693 StartY=27.4406 StartZ=0 EndX=-64.7693 EndY=22.5594 EndZ=0
    g17: LineSegment StartX=-64.7693 StartY=22.5594 StartZ=0 EndX=-60.953 EndY=19.516 EndZ=0
    g18: Circle [constr] CenterX=-59.7013 CenterY=25 CenterZ=0 NormalX=0 NormalY=0 NormalZ=1 AngleXU=0 Radius=5.625
    g19: LineSegment StartX=-62.2607 StartY=68.0679 StartZ=0 EndX=-67.1419 EndY=68.0679 EndZ=0
    g20: LineSegment StartX=-67.1419 StartY=68.0679 StartZ=0 EndX=-70.1853 EndY=64.2517 EndZ=0
    g21: LineSegment StartX=-70.1853 StartY=64.2517 StartZ=0 EndX=-69.0991 EndY=59.4929 EndZ=0
    g22: LineSegment StartX=-69.0991 StartY=59.4929 StartZ=0 EndX=-64.7013 EndY=57.375 EndZ=0
    g23: LineSegment StartX=-64.7013 StartY=57.375 StartZ=0 EndX=-60.3035 EndY=59.4929 EndZ=0
    g24: LineSegment StartX=-60.3035 StartY=59.4929 StartZ=0 EndX=-59.2174 EndY=64.2517 EndZ=0
    g25: LineSegment StartX=-59.2174 StartY=64.2517 StartZ=0 EndX=-62.2607 EndY=68.0679 EndZ=0
    g26: Circle [constr] CenterX=-64.7013 CenterY=63 CenterZ=0 NormalX=0 NormalY=0 NormalZ=1 AngleXU=0 Radius=5.625
    g27: LineSegment [constr] StartX=-64.7013 StartY=-70 StartZ=0 EndX=-64.7013 EndY=70 EndZ=0
    g28: LineSegment [constr] StartX=-59.7013 StartY=-70 StartZ=0 EndX=-59.7013 EndY=70 EndZ=0
    g29: Circle CenterX=-64.7013 CenterY=-63 CenterZ=0 NormalX=0 NormalY=0 NormalZ=1 AngleXU=0 Radius=3
    g30: Circle CenterX=-59.7013 CenterY=25 CenterZ=0 NormalX=0 NormalY=0 NormalZ=1 AngleXU=0 Radius=3
    g31: Circle CenterX=-64.7013 CenterY=63 CenterZ=0 NormalX=0 NormalY=0 NormalZ=1 AngleXU=0 Radius=3
    g32: LineSegment StartX=-54.0763 StartY=-25 StartZ=0 EndX=-56.1942 EndY=-20.6022 EndZ=0
    g33: LineSegment StartX=-56.1942 StartY=-20.6022 StartZ=0 EndX=-60.953 EndY=-19.516 EndZ=0
    g34: LineSegment StartX=-60.953 StartY=-19.516 StartZ=0 EndX=-64.7693 EndY=-22.5594 EndZ=0
    g35: LineSegment StartX=-64.7693 StartY=-22.5594 StartZ=0 EndX=-64.7693 EndY=-27.4406 EndZ=0
    g36: LineSegment StartX=-64.7693 StartY=-27.4406 StartZ=0 EndX=-60.953 EndY=-30.484 EndZ=0
    g37: LineSegment StartX=-60.953 StartY=-30.484 StartZ=0 EndX=-56.1942 EndY=-29.3978 EndZ=0
    g38: LineSegment StartX=-56.1942 StartY=-29.3978 StartZ=0 EndX=-54.0763 EndY=-25 EndZ=0
    g39: Circle [constr] CenterX=-59.7013 CenterY=-25 CenterZ=0 NormalX=0 NormalY=0 NormalZ=1 AngleXU=0 Radius=5.625
    g40: Circle CenterX=-59.7013 CenterY=-25 CenterZ=0 NormalX=0 NormalY=0 NormalZ=1 AngleXU=0 Radius=3
    g41: LineSegment StartX=-74.7013 StartY=70 StartZ=0 EndX=-74.7013 EndY=-70 EndZ=0
  constraints (102):
    c: Coincident(g1,g2)
    c: Coincident(g2,g0)
    c: Horizontal(g0)
    c: Horizontal(g1)
    c: Symmetric(g0,g1,g-1)
    c: DistanceX(g0,g0) = 25
    c: DistanceY(g1,g0) = 140
    c: Coincident(g3,g4)
    c: Coincident(g4,g5)
    c: Coincident(g5,g6)
    c: Coincident(g6,g7)
    c: Coincident(g7,g8)
    c: Coincident(g8,g9)
    c: Coincident(g9,g3)
    c: Equal(g3, g4-g9) x6
    c: PointOnObject(g3,g10)
    c: PointOnObject(g4,g10)
    c: PointOnObject(g5,g10)
    c: PointOnObject(g6,g10)
    c: PointOnObject(g7,g10)
    c: PointOnObject(g8,g10)
    c: PointOnObject(g9,g10)
    c: Coincident(g11,g12)
    c: Coincident(g12,g13)
    c: Coincident(g13,g14)
    c: Coincident(g14,g15)
    c: Coincident(g15,g16)
    c: Coincident(g16,g17)
    c: Coincident(g17,g11)
    c: Equal(g11, g12-g17) x6
    c: PointOnObject(g11,g18)
    c: PointOnObject(g12,g18)
    c: PointOnObject(g13,g18)
    c: PointOnObject(g14,g18)
    c: PointOnObject(g15,g18)
    c: PointOnObject(g16,g18)
    c: Coincident(g19,g20)
    c: Coincident(g20,g21)
    c: Coincident(g21,g22)
    c: Coincident(g22,g23)
    c: Coincident(g23,g24)
    c: Coincident(g24,g25)
    c: Coincident(g25,g19)
    c: Equal(g19, g20-g25) x6
    c: PointOnObject(g19,g26)
    c: PointOnObject(g20,g26)
    c: PointOnObject(g21,g26)
    c: PointOnObject(g22,g26)
    c: PointOnObject(g23,g26)
    c: PointOnObject(g24,g26)
    c: PointOnObject(g25,g26)
    c: Equal(g26,g18)
    c: Equal(g26,g10)
    c: Diameter(g26) = 11.25
    c: Vertical(g27)
    c: PointOnObject(g28,g1)
    c: PointOnObject(g28,g0)
    c: Vertical(g28)
    c: DistanceX(g28,g0) = 10
    c: PointOnObject(g26,g27)
    c: PointOnObject(g10,g27)
    c: DistanceY(g26,g27) = 7
    c: DistanceY(g27,g10) = 7
    c: PointOnObject(g27,g0)
    c: DistanceX(g27,g0) = 15
    c: Coincident(g29,g10)
    c: Coincident(g30,g18)
    c: Coincident(g31,g26)
    c: Equal(g29,g30)
    c: Equal(g29,g31)
    c: Diameter(g29) = 6
    c: Horizontal(g19)
    c: Horizontal(g4)
    c: PointOnObject(g11,g18)
    c: PointOnObject(g27,g1)
    c: Coincident(g32,g33)
    c: Coincident(g33,g34)
    c: Coincident(g34,g35)
    c: Coincident(g35,g36)
    c: Coincident(g36,g37)
    c: Coincident(g37,g38)
    c: Coincident(g38,g32)
    c: Equal(g32, g33-g38) x6
    c: PointOnObject(g32,g39)
    c: PointOnObject(g33,g39)
    c: PointOnObject(g34,g39)
    c: PointOnObject(g35,g39)
    c: PointOnObject(g36,g39)
    c: PointOnObject(g37,g39)
    c: Coincident(g40,g39)
    c: PointOnObject(g32,g39)
    c: Symmetric(g30,g40,g-1)
    c: PointOnObject(g30,g28)
    c: DistanceY(g40,g30) = 50
    c: Equal(g39,g10)
    c: Equal(g40,g30)
    c: Vertical(g35)
    c: Vertical(g16)
    c: Coincident(g41,g0)
    c: Coincident(g41,g1)
    c: Vertical(g41)
    c: PointOnObject(g-3,g41)
FEATURE [Sketcher::SketchExport] Export036
  Base = -> Sketch016
  BaseRefs = -> Sketch016 [edge32,edge31,edge41,edge30]
  MapMode = 5
  Placement = pos=(0,0,-15) rot=(1,0,0;3.14159rad)
  Refs = ;g41.edge32 | ;g40.edge31 | ;g54.edge41 | ;g39.edge30
  Support = -> [Binder010]
  SyncPlacement = true
  TreeRank = 482
FEATURE [Sketcher::SketchExport] Export037
  Base = -> Sketch016
  BaseRefs = -> Sketch016 [edge4,edge5,edge6,edge7,edge8,edge9,edge10,edge12,edge13,edge14,edge15,edge16,edge17,edge18,edge20,edge21,edge22,edge23,edge24,edge25,edge26,edge33,edge34,edge35,edge36,edge37,edge38,edge39]
  MapMode = 5
  Placement = pos=(0,0,-25) rot=(1,0,0;3.14159rad)
  Refs = ;g5.edge4 | ;g6.edge5 | ;g7.edge6 | ;g8.edge7 | ;g9.edge8 | ;g10.edge9 | ;g11.edge10 | ;g21.edge12 | ;g22.edge13 | ;g23.edge14 | ;g24.edge15 | ;g25.edge16 | ;g26.edge17 | ;g27.edge18 | ;g29.edge20 | ;g30.edge21 | ;g31.edge22 | ;g32.edge23 | ;g33.edge24 | ;g34.edge25 | ;g35.edge26 | ;g46.edge33 | ;g47.edge34 | ;g48.edge35 | ;g49.edge36 | ;g50.edge37 | ;g51.edge38 | ;g52.edge39
  Support = -> [Pocket003]
  SyncPlacement = true
  TreeRank = 483
FEATURE [Sketcher::SketchExport] Export038
  Base = -> Sketch016
  BaseRefs = -> Sketch016 [edge42,edge1,edge3,edge2]
  MapMode = 5
  Placement = pos=(0,0,-15) rot=(1,0,0;3.14159rad)
  Refs = ;g55.edge42 | ;g1.edge1 | ;g4.edge3 | ;g3.edge2
  Support = -> [Binder010]
  SyncPlacement = true
  TreeRank = 495
FEATURE [PartDesign::Pad] Pad039
  AddSubType = 0
  AlongSketchNormal = false
  BaseFeature = -> Pocket002
  CheckUpToFaceLimits = true
  ClaimChildren = false
  Direction = (0,0,-1)
  Fit = 0
  FitJoin = 0
  InnerFit = 0
  InnerFitJoin = 0
  InnerTaperAngle = 0
  InnerTaperAngleRev = 0
  Length = 10
  Length2 = 100
  Linearize = true
  NewSolid = false
  Profile = -> Export038
  Refine = true
  Suppress = false
  TreeRank = 496
  Type = 0
  _ProfileBasedVersion = 1
  expr: Length = <<measures>>.elipsefootthickness
FEATURE [PartDesign::Pocket] Pocket003
  AddSubType = 1
  BaseFeature = -> Fillet015
  CheckUpToFaceLimits = true
  ClaimChildren = false
  Fit = 0
  FitJoin = 0
  InnerFit = 0
  InnerFitJoin = 0
  InnerTaperAngle = 0
  InnerTaperAngleRev = 0
  Length = 20
  Length2 = 100
  Linearize = true
  NewSolid = false
  Profile = -> Export036
  Refine = true
  Reversed = true
  Suppress = false
  TreeRank = 497
  Type = 0
  _ProfileBasedVersion = 1
  _Version = 1
  expr: Length = <<measures>>.elipsefootthickness * 2
FEATURE [PartDesign::Pocket] Pocket004
  AddSubType = 1
  BaseFeature = -> Pocket003
  CheckUpToFaceLimits = true
  ClaimChildren = false
  Fit = 0
  FitJoin = 0
  InnerFit = 0
  InnerFitJoin = 0
  InnerTaperAngle = 0
  InnerTaperAngleRev = 0
  Length = 9.6
  Length2 = 100
  Linearize = true
  Midplane = true
  NewSolid = false
  Profile = -> Export037
  Refine = true
  Suppress = false
  TreeRank = 498
  Type = 0
  _ProfileBasedVersion = 1
  _Version = 1
  expr: Length = <<measures>>.elipsefeednutpocket * 2
FEATURE [PartDesign::Fillet] Fillet014
  AddSubType = 0
  Base = -> Pocket004 [Edge539,Edge537,Edge535,Edge65]
  BaseFeature = -> Pocket004
  NewSolid = false
  Radius = 4
  Refine = true
  SupportTransform = false
  Suppress = false
  TreeRank = 499
FEATURE [PartDesign::Fillet] Fillet015
  AddSubType = 0
  Base = -> Pad039 [Edge6]
  BaseFeature = -> Pad039
  NewSolid = false
  Radius = 36
  Refine = true
  SupportTransform = false
  Suppress = false
  TreeRank = 500
FEATURE [PartDesign::Fillet] Fillet016
  AddSubType = 0
  Base = -> Fillet014 [Edge14,Edge16,Edge12,Edge10]
  BaseFeature = -> Fillet014
  NewSolid = false
  Radius = 1
  Refine = true
  SupportTransform = false
  Suppress = false
  TreeRank = 501
FEATURE [PartDesign::Chamfer] Chamfer004
  AddSubType = 0
  Angle = 45
  Base = -> Fillet016 [Edge20,Edge22]
  BaseFeature = -> Fillet016
  ChamferType = 0
  FlipDirection = false
  NewSolid = false
  Refine = true
  Size = 2
  Size2 = 1
  SupportTransform = false
  Suppress = false
  TreeRank = 502
FEATURE [PartDesign::Chamfer] Chamfer005
  AddSubType = 0
  Angle = 45
  Base = -> Chamfer004 [Edge19]
  BaseFeature = -> Chamfer004
  ChamferType = 0
  FlipDirection = false
  NewSolid = false
  Refine = true
  Size = 2
  Size2 = 1
  SupportTransform = false
  Suppress = false
  TreeRank = 503
FEATURE [PartDesign::Body] Body011  label="Winkel"
  AutoGroupSolids = false
  ExportMode = 0
  Group = -> [Sketch021,Binder012,Export039,Export041,Pad040,Export043,Pad041,Pocket006,Export044,Pad042,Chamfer006,Export045,Pocket007,Sketch022,Export046,Export047,Pocket008,Pocket009,Pad045,Chamfer007,Fillet019,Fillet020,Export052]
  Origin = -> Origin011
  Tip = -> Fillet020
  TreeRank = 513
  _ExportChildren = -> [Sketch021,Binder012,Pad040,Pad041,Pocket006,Pad042,Chamfer006,Pocket007,Sketch022,Pocket008,Pocket009,Pad045,Chamfer007,Fillet019,Fillet020]
  _GroupVersion = 1
FEATURE [Sketcher::SketchObject] Sketch021  label="WinkelUnten"
  AttachmentOffset = pos=(0,0,0) rot=(0,0,1;-1.5708rad)
  Exports = -> [Export039,Export041,Export043,Export044,Export045,Export052]
  ExternalGeometry = -> [Binder012]
  FullyConstrained = true
  MapMode = 5
  Placement = pos=(0,0,-67) rot=(0,0,1;4.71239rad)
  Support = -> [Binder012]
  TreeRank = 514
  sketch-geometry (34):
    g0: LineSegment StartX=-128 StartY=-103 StartZ=0 EndX=-113 EndY=-103 EndZ=0
    g1: LineSegment StartX=-113 StartY=-103 StartZ=0 EndX=-113 EndY=-133 EndZ=0
    g2: LineSegment StartX=-113 StartY=-133 StartZ=0 EndX=-128 EndY=-133 EndZ=0
    g3: LineSegment StartX=-128 StartY=-133 StartZ=0 EndX=-128 EndY=-103 EndZ=0
    g4: ArcOfCircle CenterX=-120.5 CenterY=-110 CenterZ=0 NormalX=0 NormalY=0 NormalZ=1 AngleXU=0 Radius=3.5 StartAngle=-9e-16 EndAngle=3.14159
    g5: ArcOfCircle CenterX=-120.5 CenterY=-127.5 CenterZ=0 NormalX=0 NormalY=0 NormalZ=1 AngleXU=0 Radius=3.5 StartAngle=3.14159 EndAngle=6.28319
    g6: LineSegment StartX=-124 StartY=-110 StartZ=0 EndX=-124 EndY=-127.5 EndZ=0
    g7: LineSegment StartX=-117 StartY=-127.5 StartZ=0 EndX=-117 EndY=-110 EndZ=0
    g8: LineSegment StartX=-128 StartY=-103 StartZ=0 EndX=-113 EndY=-103 EndZ=0
    g9: LineSegment StartX=-113 StartY=-103 StartZ=0 EndX=-113 EndY=-106.5 EndZ=0
    g10: LineSegment StartX=-113 StartY=-106.5 StartZ=0 EndX=-128 EndY=-106.5 EndZ=0
    g11: LineSegment StartX=-128 StartY=-106.5 StartZ=0 EndX=-128 EndY=-103 EndZ=0
    g12: LineSegment [constr] StartX=-120.5 StartY=-103 StartZ=0 EndX=-120.5 EndY=-133 EndZ=0
    g13: LineSegment StartX=-115.5 StartY=-106.5 StartZ=0 EndX=-113 EndY=-106.5 EndZ=0
    g14: LineSegment StartX=-113 StartY=-106.5 StartZ=0 EndX=-113 EndY=-119.75 EndZ=0
    g15: LineSegment StartX=-113 StartY=-119.75 StartZ=0 EndX=-115.5 EndY=-119.75 EndZ=0
    g16: LineSegment StartX=-115.5 StartY=-119.75 StartZ=0 EndX=-115.5 EndY=-106.5 EndZ=0
    g17: LineSegment StartX=-128 StartY=-106.5 StartZ=0 EndX=-125.5 EndY=-106.5 EndZ=0
    g18: LineSegment StartX=-125.5 StartY=-106.5 StartZ=0 EndX=-125.5 EndY=-119.75 EndZ=0
    g19: LineSegment StartX=-125.5 StartY=-119.75 StartZ=0 EndX=-128 EndY=-119.75 EndZ=0
    g20: LineSegment StartX=-128 StartY=-119.75 StartZ=0 EndX=-128 EndY=-106.5 EndZ=0
    g21: GeomPoint [constr] X=-120.5 Y=-106.5 Z=0
    g22: ArcOfCircle CenterX=-120.5 CenterY=-110 CenterZ=0 NormalX=0 NormalY=0 NormalZ=1 AngleXU=0 Radius=2.1 StartAngle=3.2e-15 EndAngle=3.14159
    g23: ArcOfCircle CenterX=-120.5 CenterY=-127.5 CenterZ=0 NormalX=0 NormalY=0 NormalZ=1 AngleXU=0 Radius=2.1 StartAngle=3.14159 EndAngle=6.28319
    g24: LineSegment StartX=-122.6 StartY=-110 StartZ=0 EndX=-122.6 EndY=-127.5 EndZ=0
    g25: LineSegment StartX=-118.4 StartY=-127.5 StartZ=0 EndX=-118.4 EndY=-110 EndZ=0
    g26: LineSegment StartX=-128 StartY=-103 StartZ=0 EndX=-134 EndY=-103 EndZ=0
    g27: LineSegment StartX=-134 StartY=-103 StartZ=0 EndX=-134 EndY=-106.5 EndZ=0
    g28: LineSegment StartX=-134 StartY=-106.5 StartZ=0 EndX=-128 EndY=-106.5 EndZ=0
    g29: LineSegment StartX=-128 StartY=-106.5 StartZ=0 EndX=-128 EndY=-103 EndZ=0
    g30: LineSegment StartX=-113 StartY=-103 StartZ=0 EndX=-107 EndY=-103 EndZ=0
    g31: LineSegment StartX=-107 StartY=-103 StartZ=0 EndX=-107 EndY=-106.5 EndZ=0
    g32: LineSegment StartX=-107 StartY=-106.5 StartZ=0 EndX=-113 EndY=-106.5 EndZ=0
    g33: LineSegment StartX=-113 StartY=-106.5 StartZ=0 EndX=-113 EndY=-103 EndZ=0
  constraints (86):
    c: Coincident(g0,g1)
    c: Coincident(g1,g2)
    c: Coincident(g2,g3)
    c: Coincident(g3,g0)
    c: Horizontal(g0)
    c: Horizontal(g2)
    c: Vertical(g1)
    c: Vertical(g3)
    c: Tangent(g4,g6) = -1.5708
    c: Tangent(g6,g5) = -1.5708
    c: Tangent(g5,g7) = -1.5708
    c: Tangent(g7,g4) = -1.5708
    c: Equal(g4,g5)
    c: Vertical(g7)
    c: DistanceX(g2,g2) = 15
    c: DistanceY(g1,g1) = 30
    c: Coincident(g8,g9)
    c: Coincident(g9,g10)
    c: Coincident(g10,g11)
    c: Coincident(g11,g8)
    c: Horizontal(g8)
    c: Horizontal(g10)
    c: Vertical(g9)
    c: Vertical(g11)
    c: Coincident(g8,g0)
    c: DistanceY(g9,g9) = 3.5
    c: PointOnObject(g12,g0)
    c: Vertical(g12)
    c: Symmetric(g2,g1,g12)
    c: PointOnObject(g5,g12)
    c: DistanceX(g5,g5) = 7
    c: Coincident(g13,g14)
    c: Coincident(g14,g15)
    c: Coincident(g15,g16)
    c: Coincident(g16,g13)
    c: Horizontal(g13)
    c: Horizontal(g15)
    c: Vertical(g16)
    c: Coincident(g17,g18)
    c: Coincident(g18,g19)
    c: Coincident(g19,g20)
    c: Coincident(g20,g17)
    c: Horizontal(g17)
    c: Horizontal(g19)
    c: Vertical(g18)
    c: Coincident(g17,g10)
    c: Symmetric(g10,g2,g19)
    c: Symmetric(g9,g1,g14)
    c: DistanceX(g19,g19) = 2.5
    c: Equal(g19,g15)
    c: Coincident(g13,g9)
    c: PointOnObject(g9,g1)
    c: DistanceX(g1,g-1) = 113
    c: DistanceY(g1,g5) = 5.5
    c: PointOnObject(g21,g10)
    c: PointOnObject(g21,g12)
    c: DistanceY(g4,g21) = 3.5
    c: Tangent(g22,g24) = -1.5708
    c: Tangent(g24,g23) = -1.5708
    c: Tangent(g23,g25) = -1.5708
    c: Tangent(g25,g22) = -1.5708
    c: Equal(g22,g23)
    c: Coincident(g22,g4)
    c: Coincident(g23,g5)
    c: DistanceX(g23,g23) = 4.2
    c: DistanceY(g-3,g2) = 2
    c: Coincident(g26,g27)
    c: Coincident(g27,g28)
    c: Coincident(g28,g29)
    c: Coincident(g29,g26)
    c: Horizontal(g26)
    c: Horizontal(g28)
    c: Vertical(g27)
    c: Coincident(g26,g0)
    c: Coincident(g28,g10)
    c: Coincident(g30,g31)
    c: Coincident(g31,g32)
    c: Coincident(g32,g33)
    c: Coincident(g33,g30)
    c: Horizontal(g30)
    c: Horizontal(g32)
    c: Vertical(g31)
    c: Coincident(g30,g0)
    c: Coincident(g32,g9)
    c: Equal(g28,g32)
    c: DistanceX(g26,g0) = 6
FEATURE [Sketcher::SketchExport] Export039  label="WinkelFuss"
  Base = -> Sketch021
  BaseRefs = -> Sketch021 [edge4,edge1,edge2,edge3]
  Placement = pos=(0,0,-67) rot=(0,0,1;4.71239rad)
  Refs = ;g4.edge4 | ;g1.edge1 | ;g2.edge2 | ;g3.edge3
  SyncPlacement = true
  TreeRank = 516
FEATURE [Sketcher::SketchExport] Export041  label="Langloch"
  Base = -> Sketch021
  BaseRefs = -> Sketch021 [edge5,edge8,edge7,edge6]
  MapMode = 5
  Placement = pos=(0,0,-63) rot=(0,0,-1;1.5708rad)
  Refs = ;g5.edge5 | ;g8.edge8 | ;g7.edge7 | ;g6.edge6
  Support = -> [Pad041]
  SyncPlacement = true
  TreeRank = 518
FEATURE [PartDesign::Pad] Pad040
  AddSubType = 0
  AlongSketchNormal = false
  CheckUpToFaceLimits = true
  ClaimChildren = false
  Direction = (0,0,1)
  Fit = 0
  FitJoin = 0
  InnerFit = 0
  InnerFitJoin = 0
  InnerTaperAngle = 0
  InnerTaperAngleRev = 0
  Length = 4
  Length2 = 100
  Linearize = true
  NewSolid = false
  Placement = pos=(0,0,-67) rot=(0,0,1;4.71239rad)
  Profile = -> Export039
  Refine = true
  Suppress = false
  TreeRank = 519
  Type = 0
  _ProfileBasedVersion = 1
FEATURE [Sketcher::SketchExport] Export043  label="WinkelOben"
  Base = -> Sketch021
  BaseRefs = -> Sketch021 [edge9,edge10,edge11,edge12]
  Placement = pos=(0,0,-67) rot=(0,0,1;4.71239rad)
  Refs = ;g10.edge9 | ;g11.edge10 | ;g12.edge11 | ;g13.edge12
  SyncPlacement = true
  TreeRank = 523
FEATURE [PartDesign::Pad] Pad041
  AddSubType = 0
  AlongSketchNormal = false
  BaseFeature = -> Pad040
  CheckUpToFaceLimits = true
  ClaimChildren = false
  Direction = (0,0,1)
  Fit = 0
  FitJoin = 0
  InnerFit = 0
  InnerFitJoin = 0
  InnerTaperAngle = 0
  InnerTaperAngleRev = 0
  Length = 42
  Length2 = 100
  Linearize = true
  NewSolid = false
  Placement = pos=(0,0,-67) rot=(0,0,1;4.71239rad)
  Profile = -> Export043
  Refine = true
  Suppress = false
  TreeRank = 524
  Type = 0
  _ProfileBasedVersion = 1
FEATURE [PartDesign::Pocket] Pocket006
  AddSubType = 1
  BaseFeature = -> Pad041
  CheckUpToFaceLimits = true
  ClaimChildren = false
  Fit = 0
  FitJoin = 0
  InnerFit = 0
  InnerFitJoin = 0
  InnerTaperAngle = 0
  InnerTaperAngleRev = 0
  Length = 2
  Length2 = 100
  Linearize = true
  NewSolid = false
  Placement = pos=(0,0,-67) rot=(0,0,1;4.71239rad)
  Profile = -> Export041
  Refine = true
  Suppress = false
  TreeRank = 525
  Type = 0
  _ProfileBasedVersion = 1
  _Version = 1
FEATURE [Sketcher::SketchExport] Export044  label="Support"
  Base = -> Sketch021
  BaseRefs = -> Sketch021 [edge14,edge15,edge16,edge17,edge18,edge19,edge20,edge21]
  Placement = pos=(0,0,-67) rot=(0,0,1;4.71239rad)
  Refs = ;g15.edge14 | ;g16.edge15 | ;g17.edge16 | ;g18.edge17 | ;g19.edge18 | ;g20.edge19 | ;g21.edge20 | ;g22.edge21
  SyncPlacement = true
  TreeRank = 526
FEATURE [PartDesign::Pad] Pad042
  AddSubType = 0
  AlongSketchNormal = false
  BaseFeature = -> Pocket006
  CheckUpToFaceLimits = true
  ClaimChildren = false
  Direction = (0,0,1)
  Fit = 0
  FitJoin = 0
  InnerFit = 0
  InnerFitJoin = 0
  InnerTaperAngle = 0
  InnerTaperAngleRev = 0
  Length = 36
  Length2 = 100
  Linearize = true
  NewSolid = false
  Placement = pos=(0,0,-67) rot=(0,0,1;4.71239rad)
  Profile = -> Export044
  Refine = true
  Suppress = false
  TreeRank = 527
  Type = 0
  _ProfileBasedVersion = 1
FEATURE [PartDesign::Chamfer] Chamfer006
  AddSubType = 0
  Angle = 45
  Base = -> Pad042 [Edge19,Edge22]
  BaseFeature = -> Pad042
  ChamferType = 1
  FlipDirection = false
  NewSolid = false
  Placement = pos=(0,0,-67) rot=(0,0,1;4.71239rad)
  Refine = true
  Size = 11
  Size2 = 30
  SupportTransform = false
  Suppress = false
  TreeRank = 528
FEATURE [Sketcher::SketchExport] Export045  label="Langlochloch"
  Base = -> Sketch021
  BaseRefs = -> Sketch021 [edge23,edge24,edge25,edge26]
  Placement = pos=(0,0,-67) rot=(0,0,1;4.71239rad)
  Refs = ;g29.edge23 | ;g30.edge24 | ;g31.edge25 | ;g32.edge26
  SyncPlacement = true
  TreeRank = 529
FEATURE [PartDesign::Pocket] Pocket007
  AddSubType = 1
  BaseFeature = -> Chamfer006
  CheckUpToFaceLimits = true
  ClaimChildren = false
  Fit = 0
  FitJoin = 0
  InnerFit = 0
  InnerFitJoin = 0
  InnerTaperAngle = 0
  InnerTaperAngleRev = 0
  Length = 5
  Length2 = 100
  Linearize = true
  NewSolid = false
  Placement = pos=(0,0,-67) rot=(0,0,1;4.71239rad)
  Profile = -> Export045
  Refine = true
  Reversed = true
  Suppress = false
  TreeRank = 530
  Type = 0
  _ProfileBasedVersion = 1
  _Version = 1
FEATURE [Sketcher::SketchObject] Sketch022  label="horizontal"
  Exports = -> [Export046,Export047]
  ExternalGeometry = -> [Pocket007,Sketch021]
  FullyConstrained = true
  MapMode = 5
  Placement = pos=(-103,0,-67) rot=(0.57735,0.57735,0.57735;2.0944rad)
  Support = -> [Pocket007]
  TreeRank = 531
  sketch-geometry (9):
    g0: LineSegment [constr] StartX=120.5 StartY=42 StartZ=0 EndX=120.5 EndY=-1.42e-14 EndZ=0
    g1: ArcOfCircle CenterX=120.5 CenterY=36 CenterZ=0 NormalX=0 NormalY=0 NormalZ=1 AngleXU=0 Radius=3.95 StartAngle=-2.4e-14 EndAngle=3.14159
    g2: ArcOfCircle CenterX=120.5 CenterY=10.5 CenterZ=0 NormalX=0 NormalY=0 NormalZ=1 AngleXU=0 Radius=3.95 StartAngle=3.14159 EndAngle=6.28319
    g3: LineSegment StartX=116.55 StartY=36 StartZ=0 EndX=116.55 EndY=10.5 EndZ=0
    g4: LineSegment StartX=124.45 StartY=10.5 StartZ=0 EndX=124.45 EndY=36 EndZ=0
    g5: ArcOfCircle CenterX=120.5 CenterY=36 CenterZ=0 NormalX=0 NormalY=0 NormalZ=1 AngleXU=0 Radius=1.5 StartAngle=-9e-16 EndAngle=3.14159
    g6: ArcOfCircle CenterX=120.5 CenterY=10.5 CenterZ=0 NormalX=0 NormalY=0 NormalZ=1 AngleXU=0 Radius=1.5 StartAngle=3.14159 EndAngle=6.28319
    g7: LineSegment StartX=119 StartY=36 StartZ=0 EndX=119 EndY=10.5 EndZ=0
    g8: LineSegment StartX=122 StartY=10.5 StartZ=0 EndX=122 EndY=36 EndZ=0
  constraints (21):
    c: PointOnObject(g0,g-6)
    c: Vertical(g0)
    c: Symmetric(g-5,g-4,g0)
    c: Tangent(g1,g3) = -1.5708
    c: Tangent(g3,g2) = -1.5708
    c: Tangent(g2,g4) = -1.5708
    c: Tangent(g4,g1) = -1.5708
    c: Equal(g1,g2)
    c: PointOnObject(g1,g0)
    c: PointOnObject(g2,g0)
    c: Tangent(g5,g7) = -1.5708
    c: Tangent(g7,g6) = -1.5708
    c: Tangent(g6,g8) = -1.5708
    c: Tangent(g8,g5) = -1.5708
    c: Equal(g5,g6)
    c: Coincident(g6,g2)
    c: Coincident(g5,g1)
    c: DistanceX(g6,g6) = 3
    c: DistanceX(g2,g2) = 7.9
    c: DistanceY(g1,g0) = 6
    c: DistanceY(g0,g2) = 10.5
FEATURE [Sketcher::SketchExport] Export046
  Base = -> Sketch022
  BaseRefs = -> Sketch022 [edge2,edge3,edge4,edge5]
  Placement = pos=(-103,2.29e-14,-67) rot=(0.57735,0.57735,0.57735;2.0944rad)
  Refs = ;g9.edge2 | ;g10.edge3 | ;g11.edge4 | ;g12.edge5
  SyncPlacement = true
  TreeRank = 532
FEATURE [Sketcher::SketchExport] Export047
  Base = -> Sketch022
  BaseRefs = -> Sketch022 [edge6,edge7,edge8,edge9]
  Placement = pos=(-103,2.29e-14,-67) rot=(0.57735,0.57735,0.57735;2.0944rad)
  Refs = ;g13.edge6 | ;g14.edge7 | ;g15.edge8 | ;g16.edge9
  SyncPlacement = true
  TreeRank = 533
FEATURE [PartDesign::Pocket] Pocket008
  AddSubType = 1
  BaseFeature = -> Pocket007
  CheckUpToFaceLimits = true
  ClaimChildren = false
  Fit = 0
  FitJoin = 0
  InnerFit = 0
  InnerFitJoin = 0
  InnerTaperAngle = 0
  InnerTaperAngleRev = 0
  Length = 2
  Length2 = 100
  Linearize = true
  NewSolid = false
  Placement = pos=(0,0,-67) rot=(0,0,1;4.71239rad)
  Profile = -> Export046
  Refine = true
  Suppress = false
  TreeRank = 534
  Type = 0
  _ProfileBasedVersion = 1
  _Version = 1
FEATURE [PartDesign::Pocket] Pocket009
  AddSubType = 1
  BaseFeature = -> Pocket008
  CheckUpToFaceLimits = true
  ClaimChildren = false
  Fit = 0
  FitJoin = 0
  InnerFit = 0
  InnerFitJoin = 0
  InnerTaperAngle = 0
  InnerTaperAngleRev = 0
  Length = 5
  Length2 = 100
  Linearize = true
  NewSolid = false
  Placement = pos=(0,0,-67) rot=(0,0,1;4.71239rad)
  Profile = -> Export047
  Refine = true
  Suppress = false
  TreeRank = 535
  Type = 0
  _ProfileBasedVersion = 1
  _Version = 1
FEATURE [Part::Mirroring] Part__Mirroring002  label="Winkel (Mirror #3)"
  Base = (0,0,0)
  Normal = (0,1,0)
  Source = -> Body011
  TreeRank = 558
FEATURE [PartDesign::Body] Body012  label="AxelBearing"
  AutoGroupSolids = false
  ExportMode = 0
  Group = -> [Binder013,Sketch023,Export048,Export049,Export050,Pad043,DatumPlane004,Pocket010,DatumPlane005,Pad044,Fillet018,Export051,Pocket011]
  Origin = -> Origin013
  Tip = -> Pocket011
  TreeRank = 571
  _ExportChildren = -> [Binder013,Sketch023,Pad043,DatumPlane004,Pocket010,DatumPlane005,Pad044,Fillet018,Pocket011]
  _GroupVersion = 1
FEATURE [Sketcher::SketchObject] Sketch023
  Exports = -> [Export048,Export049,Export050,Export051]
  ExternalGeometry = -> [Binder013]
  FullyConstrained = true
  MapMode = 5
  Placement = pos=(-3.84e-14,128,1.02e-14) rot=(0,0.707107,0.707107;3.14159rad)
  Support = -> [Binder013]
  TreeRank = 573
  sketch-geometry (12):
    g0: LineSegment StartX=103 StartY=-29.5 StartZ=0 EndX=92 EndY=-29.5 EndZ=0
    g1: LineSegment StartX=103 StartY=-47.5 StartZ=0 EndX=92 EndY=-47.5 EndZ=0
    g2: ArcOfCircle CenterX=97 CenterY=-38.5 CenterZ=0 NormalX=0 NormalY=0 NormalZ=1 AngleXU=0 Radius=10.2956 StartAngle=2.07789 EndAngle=4.20529
    g3: LineSegment [constr] StartX=97 StartY=-29.5 StartZ=0 EndX=97 EndY=-47.5 EndZ=0
    g4: LineSegment StartX=103 StartY=-29.5 StartZ=0 EndX=103 EndY=-47.5 EndZ=0
    g5: Circle CenterX=97 CenterY=-38.5 CenterZ=0 NormalX=0 NormalY=0 NormalZ=1 AngleXU=0 Radius=3.1
    g6: LineSegment StartX=103 StartY=-33.5 StartZ=0 EndX=104.9 EndY=-33.5 EndZ=0
    g7: LineSegment StartX=104.9 StartY=-33.5 StartZ=0 EndX=104.9 EndY=-43.5 EndZ=0
    g8: LineSegment StartX=104.9 StartY=-43.5 StartZ=0 EndX=103 EndY=-43.5 EndZ=0
    g9: LineSegment StartX=103 StartY=-43.5 StartZ=0 EndX=103 EndY=-33.5 EndZ=0
    g10: GeomPoint [constr] X=103 Y=-38.5 Z=0
    g11: Circle CenterX=97 CenterY=-38.5 CenterZ=0 NormalX=0 NormalY=0 NormalZ=1 AngleXU=0 Radius=1.25
  constraints (32):
    c: Horizontal(g0)
    c: Horizontal(g1)
    c: Coincident(g2,g0)
    c: Coincident(g2,g1)
    c: PointOnObject(g3,g0)
    c: PointOnObject(g3,g1)
    c: Vertical(g3)
    c: Symmetric(g3,g3,g2)
    c: DistanceX(g1,g1) = 11
    c: Coincident(g4,g0)
    c: Coincident(g4,g1)
    c: DistanceY(g4,g4) = 18
    c: DistanceX(g3,g1) = 6
    c: Coincident(g5,g2)
    c: Diameter(g5) = 6.2
    c: Coincident(g6,g7)
    c: Coincident(g7,g8)
    c: Coincident(g8,g9)
    c: Coincident(g9,g6)
    c: Horizontal(g6)
    c: Horizontal(g8)
    c: Vertical(g7)
    c: Vertical(g9)
    c: DistanceX(g8,g8) = 1.9
    c: Symmetric(g6,g8,g10)
    c: Symmetric(g1,g0,g10)
    c: DistanceY(g7,g7) = 10
    c: Coincident(g11,g2)
    c: Diameter(g11) = 2.5
    c: PointOnObject(g6,g-3)
    c: PointOnObject(g6,g4)
    c: DistanceY(g6,g-3) = 4.5
FEATURE [Sketcher::SketchExport] Export048  label="bearingaxelall"
  Base = -> Sketch023
  BaseRefs = -> Sketch023 [edge1,edge3,edge2,edge5]
  Placement = pos=(-9.7e-15,128,1.08e-14) rot=(0,0.707107,0.707107;3.14159rad)
  Refs = ;g2.edge1 | ;g4.edge3 | ;g3.edge2 | ;g6.edge5
  SyncPlacement = true
  TreeRank = 575
FEATURE [Sketcher::SketchExport] Export049  label="axelhole"
  Base = -> Sketch023
  BaseRefs = -> Sketch023 [edge6]
  MapMode = 5
  Placement = pos=(-3.69e-14,123,9.1e-15) rot=(0,0.707107,0.707107;3.14159rad)
  Refs = ;g7.edge6
  Support = -> [DatumPlane004]
  SyncPlacement = true
  TreeRank = 576
FEATURE [Sketcher::SketchExport] Export050  label="supportbearingholder"
  Base = -> Sketch023
  BaseRefs = -> Sketch023 [edge7,edge8,edge9,edge10]
  MapMode = 5
  Placement = pos=(-3.62e-14,120.5,8.6e-15) rot=(0,0.707107,0.707107;3.14159rad)
  Refs = ;g8.edge7 | ;g9.edge8 | ;g10.edge9 | ;g11.edge10
  Support = -> [DatumPlane005]
  SyncPlacement = true
  TreeRank = 577
FEATURE [PartDesign::Pad] Pad043
  AddSubType = 0
  AlongSketchNormal = false
  CheckUpToFaceLimits = true
  ClaimChildren = false
  Direction = (-1e-16,1,2e-16)
  Fit = 0
  FitJoin = 0
  InnerFit = 0
  InnerFitJoin = 0
  InnerTaperAngle = 0
  InnerTaperAngleRev = 0
  Length = 15
  Length2 = 100
  Linearize = true
  NewSolid = false
  Placement = pos=(-9.7e-15,128,1.08e-14) rot=(0,0.707107,0.707107;3.14159rad)
  Profile = -> Export048
  Refine = true
  Reversed = true
  Suppress = false
  TreeRank = 578
  Type = 0
  _ProfileBasedVersion = 1
FEATURE [PartDesign::Pocket] Pocket010
  AddSubType = 1
  BaseFeature = -> Pad043
  CheckUpToFaceLimits = true
  ClaimChildren = false
  Fit = 0
  FitJoin = 0
  InnerFit = 0
  InnerFitJoin = 0
  InnerTaperAngle = 0
  InnerTaperAngleRev = 0
  Length = 14
  Length2 = 100
  Linearize = true
  NewSolid = false
  Placement = pos=(-9.7e-15,128,1.08e-14) rot=(0,0.707107,0.707107;3.14159rad)
  Profile = -> Export049
  Refine = true
  Suppress = false
  TreeRank = 580
  Type = 0
  _ProfileBasedVersion = 1
  _Version = 1
FEATURE [PartDesign::Pad] Pad044
  AddSubType = 0
  AlongSketchNormal = false
  BaseFeature = -> Pocket010
  CheckUpToFaceLimits = true
  ClaimChildren = false
  Direction = (-1e-16,1,2e-16)
  Fit = 0
  FitJoin = 0
  InnerFit = 0
  InnerFitJoin = 0
  InnerTaperAngle = 0
  InnerTaperAngleRev = 0
  Length = 7.8
  Length2 = 100
  Linearize = true
  Midplane = true
  NewSolid = false
  Placement = pos=(-9.7e-15,128,1.08e-14) rot=(0,0.707107,0.707107;3.14159rad)
  Profile = -> Export050
  Refine = true
  Suppress = false
  TreeRank = 582
  Type = 0
  _ProfileBasedVersion = 1
FEATURE [PartDesign::Fillet] Fillet018
  AddSubType = 0
  Base = -> Pad044 [Edge24,Edge21,Edge20,Edge19]
  BaseFeature = -> Pad044
  NewSolid = false
  Placement = pos=(-9.7e-15,128,1.08e-14) rot=(0,0.707107,0.707107;3.14159rad)
  Radius = 2
  Refine = true
  SupportTransform = false
  Suppress = false
  TreeRank = 583
FEATURE [Part::Mirroring] Part__Mirroring003  label="AxelBearing (Mirror #4)"
  Base = (0,0,0)
  Normal = (0,1,0)
  Source = -> Body012
  TreeRank = 584
FEATURE [Sketcher::SketchExport] Export051  label="gewinde"
  Base = -> Sketch023
  BaseRefs = -> Sketch023 [edge12]
  Placement = pos=(-9.7e-15,128,1.08e-14) rot=(0,0.707107,0.707107;3.14159rad)
  Refs = ;g13.edge12
  SyncPlacement = true
  TreeRank = 585
FEATURE [PartDesign::Pocket] Pocket011
  AddSubType = 1
  BaseFeature = -> Fillet018
  CheckUpToFaceLimits = true
  ClaimChildren = false
  Fit = 0
  FitJoin = 0
  InnerFit = 0
  InnerFitJoin = 0
  InnerTaperAngle = 0
  InnerTaperAngleRev = 0
  Length = 6
  Length2 = 100
  Linearize = true
  NewSolid = false
  Placement = pos=(-9.7e-15,128,1.08e-14) rot=(0,0.707107,0.707107;3.14159rad)
  Profile = -> Export051
  Refine = true
  Suppress = false
  TreeRank = 586
  Type = 0
  _ProfileBasedVersion = 1
  _Version = 1
FEATURE [Sketcher::SketchExport] Export052  label="SupportSide"
  Base = -> Sketch021
  BaseRefs = -> Sketch021 [edge27,edge28,edge29,edge30,edge31,edge32,edge33,edge34]
  Placement = pos=(0,0,-67) rot=(0,0,1;4.71239rad)
  Refs = ;g33.edge27 | ;g34.edge28 | ;g35.edge29 | ;g36.edge30 | ;g37.edge31 | ;g38.edge32 | ;g39.edge33 | ;g40.edge34
  SyncPlacement = true
  TreeRank = 588
FEATURE [PartDesign::Pad] Pad045
  AddSubType = 0
  AlongSketchNormal = false
  BaseFeature = -> Pocket009
  CheckUpToFaceLimits = true
  ClaimChildren = false
  Direction = (0,0,1)
  Fit = 0
  FitJoin = 0
  InnerFit = 0
  InnerFitJoin = 0
  InnerTaperAngle = 0
  InnerTaperAngleRev = 0
  Length = 36
  Length2 = 100
  Linearize = true
  NewSolid = false
  Placement = pos=(0,0,-67) rot=(0,0,1;4.71239rad)
  Profile = -> Export052
  Refine = true
  Suppress = false
  TreeRank = 589
  Type = 0
  _ProfileBasedVersion = 1
FEATURE [PartDesign::Chamfer] Chamfer007
  AddSubType = 0
  Angle = 45
  Base = -> Pad045 [Edge83,Edge85]
  BaseFeature = -> Pad045
  ChamferType = 1
  FlipDirection = false
  NewSolid = false
  Placement = pos=(0,0,-67) rot=(0,0,1;4.71239rad)
  Refine = true
  Size = 4
  Size2 = 30
  SupportTransform = false
  Suppress = false
  TreeRank = 590
FEATURE [PartDesign::Fillet] Fillet019
  AddSubType = 0
  Base = -> Chamfer007 [Edge57,Edge79,Edge25,Edge43]
  BaseFeature = -> Chamfer007
  NewSolid = false
  Placement = pos=(0,0,-67) rot=(0,0,1;4.71239rad)
  Radius = 4
  Refine = true
  SupportTransform = false
  Suppress = false
  TreeRank = 591
FEATURE [PartDesign::Fillet] Fillet020
  AddSubType = 0
  Base = -> Fillet019 [Edge111,Edge64,Edge68,Edge112,Edge75,Edge106,Edge81,Edge16,Edge90,Edge49,Edge67,Edge63,Edge92,Edge104,Edge74,Edge80]
  BaseFeature = -> Fillet019
  NewSolid = false
  Placement = pos=(0,0,-67) rot=(0,0,1;4.71239rad)
  Radius = 1
  Refine = true
  SupportTransform = false
  Suppress = false
  TreeRank = 592
FEATURE [PartDesign::Body] Body014  label="Driveholder"
  AutoGroupSolids = false
  ExportMode = 0
  Group = -> [Binder015,DatumPlane007,Sketch026,Sketch027,Pad046,Sketch028,Pad047,Sketch029,Fillet024,Pocket013,Fillet022,Sketch030,Export053,Export054,Pocket014,Pocket015,Fillet023,Chamfer014]
  Origin = -> Origin015
  Tip = -> Chamfer014
  TreeRank = 621
  _ExportChildren = -> [Binder015,DatumPlane007,Sketch026,Pad046,Pad047,Fillet024,Pocket013,Fillet022,Sketch030,Pocket014,Pocket015,Fillet023,Chamfer014]
  _GroupVersion = 1
FEATURE [Sketcher::SketchObject] Sketch030  label="driveholderxy"
  Exports = -> [Export053,Export054]
  ExternalGeometry = -> [Fillet022]
  FullyConstrained = false
  MapMode = 5
  Placement = pos=(1.85e-14,78,-59) rot=(0,0,1;0rad)
  Support = -> [Fillet022]
  TreeRank = 636
  sketch-geometry (18):
    g0: ArcOfCircle CenterX=-134.65 CenterY=-15 CenterZ=0 NormalX=0 NormalY=0 NormalZ=1 AngleXU=0 Radius=3.5 StartAngle=1.5708 EndAngle=4.71239
    g1: ArcOfCircle CenterX=-89.7812 CenterY=-15 CenterZ=0 NormalX=0 NormalY=0 NormalZ=1 AngleXU=0 Radius=3.5 StartAngle=4.71239 EndAngle=7.85398
    g2: LineSegment StartX=-134.65 StartY=-18.5 StartZ=0 EndX=-89.7812 EndY=-18.5 EndZ=0
    g3: LineSegment StartX=-89.7812 StartY=-11.5 StartZ=0 EndX=-134.65 EndY=-11.5 EndZ=0
    g4: ArcOfCircle CenterX=-134.742 CenterY=-33 CenterZ=0 NormalX=0 NormalY=0 NormalZ=1 AngleXU=0 Radius=3.5 StartAngle=1.5708 EndAngle=4.71239
    g5: ArcOfCircle CenterX=-89.7812 CenterY=-33 CenterZ=0 NormalX=0 NormalY=0 NormalZ=1 AngleXU=0 Radius=3.5 StartAngle=4.71239 EndAngle=7.85398
    g6: LineSegment StartX=-134.742 StartY=-36.5 StartZ=0 EndX=-89.7812 EndY=-36.5 EndZ=0
    g7: LineSegment StartX=-89.7812 StartY=-29.5 StartZ=0 EndX=-134.742 EndY=-29.5 EndZ=0
    g8: LineSegment [constr] StartX=-89.7812 StartY=1.42e-14 StartZ=0 EndX=-89.7812 EndY=-48 EndZ=0
    g9: LineSegment [constr] StartX=-134.781 StartY=-4.6498e-12 StartZ=0 EndX=-134.781 EndY=-48 EndZ=0
    g10: ArcOfCircle CenterX=-134.65 CenterY=-15 CenterZ=0 NormalX=0 NormalY=0 NormalZ=1 AngleXU=0 Radius=2.1 StartAngle=1.5708 EndAngle=4.71239
    g11: ArcOfCircle CenterX=-89.7812 CenterY=-15 CenterZ=0 NormalX=0 NormalY=0 NormalZ=1 AngleXU=0 Radius=2.1 StartAngle=4.71239 EndAngle=7.85398
    g12: LineSegment StartX=-134.65 StartY=-17.1 StartZ=0 EndX=-89.7812 EndY=-17.1 EndZ=0
    g13: LineSegment StartX=-89.7812 StartY=-12.9 StartZ=0 EndX=-134.65 EndY=-12.9 EndZ=0
    g14: ArcOfCircle CenterX=-134.742 CenterY=-33 CenterZ=0 NormalX=0 NormalY=0 NormalZ=1 AngleXU=0 Radius=2.1 StartAngle=1.5708 EndAngle=4.71239
    g15: ArcOfCircle CenterX=-89.7812 CenterY=-33 CenterZ=0 NormalX=0 NormalY=0 NormalZ=1 AngleXU=0 Radius=2.1 StartAngle=4.71239 EndAngle=7.85398
    g16: LineSegment StartX=-134.742 StartY=-35.1 StartZ=0 EndX=-89.7812 EndY=-35.1 EndZ=0
    g17: LineSegment StartX=-89.7812 StartY=-30.9 StartZ=0 EndX=-134.742 EndY=-30.9 EndZ=0
  constraints (40):
    c: Tangent(g0,g2) = -1.5708
    c: Tangent(g2,g1) = -1.5708
    c: Tangent(g1,g3) = -1.5708
    c: Tangent(g3,g0) = -1.5708
    c: Equal(g0,g1)
    c: Tangent(g4,g6) = -1.5708
    c: Tangent(g6,g5) = -1.5708
    c: Tangent(g5,g7) = -1.5708
    c: Tangent(g7,g4) = -1.5708
    c: Equal(g4,g5)
    c: Coincident(g8,g-5)
    c: Coincident(g8,g-4)
    c: PointOnObject(g1,g8)
    c: PointOnObject(g5,g8)
    c: PointOnObject(g9,g-5)
    c: PointOnObject(g9,g-4)
    c: Vertical(g9)
    c: DistanceX(g-5,g9) = 7
    c: Horizontal(g3)
    c: Horizontal(g7)
    c: DistanceY(g1,g1) = 7
    c: DistanceY(g5,g5) = 7
    c: Tangent(g10,g12) = -1.5708
    c: Tangent(g12,g11) = -1.5708
    c: Tangent(g11,g13) = -1.5708
    c: Tangent(g13,g10) = -1.5708
    c: Equal(g10,g11)
    c: Coincident(g10,g0)
    c: Coincident(g11,g1)
    c: Tangent(g14,g16) = -1.5708
    c: Tangent(g16,g15) = -1.5708
    c: Tangent(g15,g17) = -1.5708
    c: Tangent(g17,g14) = -1.5708
    c: Equal(g14,g15)
    c: Coincident(g14,g4)
    c: Coincident(g15,g5)
    c: DistanceY(g11,g11) = 4.2
    c: DistanceY(g15,g15) = 4.2
    c: DistanceY(g1,g-5) = 15
    c: DistanceY(g-4,g5) = 15
FEATURE [Sketcher::SketchExport] Export053
  Base = -> Sketch030
  BaseRefs = -> Sketch030 [edge1,edge2,edge3,edge4,edge5,edge6,edge7,edge8]
  Placement = pos=(2.02e-14,78,-59) rot=(0,0,1;0rad)
  Refs = ;g4.edge1 | ;g5.edge2 | ;g6.edge3 | ;g7.edge4 | ;g8.edge5 | ;g9.edge6 | ;g10.edge7 | ;g11.edge8
  SyncPlacement = true
  TreeRank = 637
FEATURE [Sketcher::SketchExport] Export054
  Base = -> Sketch030
  BaseRefs = -> Sketch030 [edge11,edge12,edge13,edge14,edge15,edge16,edge17,edge18]
  Placement = pos=(2.02e-14,78,-59) rot=(0,0,1;0rad)
  Refs = ;g17.edge11 | ;g18.edge12 | ;g19.edge13 | ;g20.edge14 | ;g21.edge15 | ;g22.edge16 | ;g23.edge17 | ;g24.edge18
  SyncPlacement = true
  TreeRank = 638
FEATURE [PartDesign::Pocket] Pocket014
  AddSubType = 1
  BaseFeature = -> Fillet022
  CheckUpToFaceLimits = true
  ClaimChildren = false
  Fit = 0
  FitJoin = 0
  InnerFit = 0
  InnerFitJoin = 0
  InnerTaperAngle = 0
  InnerTaperAngleRev = 0
  Length = 17
  Length2 = 100
  Linearize = true
  NewSolid = false
  Placement = pos=(1.73e-14,78,1.1e-15) rot=(0,0.707107,0.707107;3.14159rad)
  Profile = -> Export054
  Refine = true
  Suppress = false
  TreeRank = 639
  Type = 0
  _ProfileBasedVersion = 1
  _Version = 1
FEATURE [PartDesign::Pocket] Pocket015
  AddSubType = 1
  BaseFeature = -> Pocket014
  CheckUpToFaceLimits = true
  ClaimChildren = false
  Fit = 0
  FitJoin = 0
  InnerFit = 0
  InnerFitJoin = 0
  InnerTaperAngle = 0
  InnerTaperAngleRev = 0
  Length = 2.5
  Length2 = 100
  Linearize = true
  NewSolid = false
  Placement = pos=(1.73e-14,78,1.1e-15) rot=(0,0.707107,0.707107;3.14159rad)
  Profile = -> Export053
  Refine = true
  Suppress = false
  TreeRank = 640
  Type = 0
  _ProfileBasedVersion = 1
  _Version = 1
FEATURE [PartDesign::Fillet] Fillet023
  AddSubType = 0
  Base = -> Pocket015 [Edge142,Edge133]
  BaseFeature = -> Pocket015
  NewSolid = false
  Placement = pos=(1.73e-14,78,1.1e-15) rot=(0,0.707107,0.707107;3.14159rad)
  Radius = 7
  Refine = true
  SupportTransform = false
  Suppress = false
  TreeRank = 642
FEATURE [PartDesign::Chamfer] Chamfer014
  AddSubType = 0
  Angle = 45
  Base = -> Fillet023 [Edge82]
  BaseFeature = -> Fillet023
  ChamferType = 0
  FlipDirection = false
  NewSolid = false
  Placement = pos=(1.73e-14,78,1.1e-15) rot=(0,0.707107,0.707107;3.14159rad)
  Refine = true
  Size = 1.5
  Size2 = 1
  SupportTransform = false
  Suppress = false
  TreeRank = 644
FEATURE [PartDesign::Body] Body015  label="LinearMotorHolder"
  AutoGroupSolids = false
  ExportMode = 0
  Group = -> [Binder016,Sketch031,Binder017,Export055,Pad048,Export056,Pad049,Fillet025]
  Origin = -> Origin016
  Tip = -> Fillet025
  TreeRank = 654
  _ExportChildren = -> [Binder016,Sketch031,Binder017,Pad048,Pad049,Fillet025]
  _GroupVersion = 1
FEATURE [Sketcher::SketchObject] Sketch031  label="linearholder"
  AttachmentOffset = pos=(0,0,0) rot=(0,0,1;1.5708rad)
  Exports = -> [Export055,Export056]
  ExternalGeometry = -> [Binder016]
  FullyConstrained = true
  MapMode = 5
  Placement = pos=(0,0,-67) rot=(0,0,1;1.5708rad)
  Support = -> [Binder017]
  TreeRank = 656
  sketch-geometry (15):
    g0: Circle CenterX=7.53e-14 CenterY=-317.656 CenterZ=0 NormalX=0 NormalY=0 NormalZ=1 AngleXU=0 Radius=5.25
    g1: LineSegment StartX=-19.8997 StartY=-315.656 StartZ=0 EndX=-27.3622 EndY=-389.906 EndZ=0
    g2: LineSegment StartX=19.8997 StartY=-315.656 StartZ=0 EndX=27.3622 EndY=-389.906 EndZ=0
    g3: ArcOfCircle CenterX=7.53e-14 CenterY=-317.656 CenterZ=0 NormalX=0 NormalY=0 NormalZ=1 AngleXU=0 Radius=20 StartAngle=0.100167 EndAngle=3.04143
    g4: Circle CenterX=0 CenterY=-349.656 CenterZ=0 NormalX=0 NormalY=0 NormalZ=1 AngleXU=0 Radius=5.25
    g5: ArcOfCircle CenterX=3.37e-14 CenterY=-392.656 CenterZ=0 NormalX=0 NormalY=0 NormalZ=1 AngleXU=0 Radius=27.5 StartAngle=5.14383 EndAngle=6.38335
    g6: ArcOfCircle CenterX=3.37e-14 CenterY=-392.656 CenterZ=0 NormalX=0 NormalY=0 NormalZ=1 AngleXU=0 Radius=17.5 StartAngle=4.79821 EndAngle=10.9098
    g7: LineSegment StartX=-1.5 StartY=-410.092 StartZ=0 EndX=-1.5 EndY=-435.636 EndZ=0
    g8: LineSegment StartX=1.5 StartY=-410.092 StartZ=0 EndX=1.5 EndY=-435.636 EndZ=0
    g9: LineSegment StartX=11.5 StartY=-417.636 StartZ=0 EndX=11.5 EndY=-435.636 EndZ=0
    g10: LineSegment StartX=-11.5 StartY=-417.636 StartZ=0 EndX=-11.5 EndY=-435.636 EndZ=0
    g11: LineSegment StartX=-11.5 StartY=-435.636 StartZ=0 EndX=-1.5 EndY=-435.636 EndZ=0
    g12: LineSegment StartX=1.5 StartY=-435.636 StartZ=0 EndX=11.5 EndY=-435.636 EndZ=0
    g13: ArcOfCircle CenterX=3.37e-14 CenterY=-392.656 CenterZ=0 NormalX=0 NormalY=0 NormalZ=1 AngleXU=0 Radius=27.5 StartAngle=3.04143 EndAngle=4.28095
    g14: ArcOfCircle CenterX=3.37e-14 CenterY=-392.656 CenterZ=0 NormalX=0 NormalY=0 NormalZ=1 AngleXU=0 Radius=27.5 StartAngle=5.14383 EndAngle=10.5641
  constraints (39):
    c: Coincident(g0,g-3)
    c: Diameter(g0) = 10.5
    c: Coincident(g3,g0)
    c: Coincident(g3,g2)
    c: Tangent(g3,g1) = -1.5708
    c: Tangent(g2,g3) = 1.5708
    c: PointOnObject(g4,g-2)
    c: Symmetric(g13,g5,g-2)
    c: DistanceY(g4,g0) = 32
    c: Coincident(g6,g5)
    c: Coincident(g7,g6)
    c: Vertical(g7)
    c: Coincident(g8,g6)
    c: Symmetric(g6,g6,g-2)
    c: Vertical(g9)
    c: Vertical(g10)
    c: Coincident(g11,g10)
    c: Coincident(g11,g7)
    c: Coincident(g12,g8)
    c: Coincident(g12,g9)
    c: Perpendicular(g10,g11)
    c: Perpendicular(g12,g8)
    c: Coincident(g9,g5)
    c: Coincident(g10,g13)
    c: Radius(g3) = 20
    c: Tangent(g5,g2) = 1.5708
    c: Tangent(g13,g1) = -1.5708
    c: Coincident(g5,g13)
    c: DistanceX(g7,g8) = 3
    c: Diameter(g6) = 35
    c: Diameter(g5) = 55
    c: DistanceX(g12,g12) = 10
    c: Symmetric(g7,g8,g-2)
    c: DistanceY(g9,g9) = 18
    c: DistanceY(g5,g0) = 75
    c: Equal(g4,g0)
    c: Coincident(g14,g5)
    c: Coincident(g14,g10)
    c: Coincident(g14,g5)
FEATURE [Sketcher::SketchExport] Export055  label="bottomshapelinear"
  AttachmentOffset = pos=(0,0,0) rot=(0,0,1;1.5708rad)
  Base = -> Sketch031
  BaseRefs = -> Sketch031 [edge2,edge4,edge3,edge1,edge5,edge6,edge7,edge14,edge11,edge12,edge13,edge10,edge8,edge9]
  MapMode = 5
  Placement = pos=(0,0,-67) rot=(0,0,1;1.5708rad)
  Refs = ;g11.edge2 | ;g16.edge4 | ;g14.edge3 | ;g2.edge1 | ;g17.edge5 | ;g19.edge6 | ;g20.edge7 | ;g28.edge14 | ;g26.edge11 | ;g23.edge12 | ;g27.edge13 | ;g25.edge10 | ;g21.edge8 | ;g22.edge9
  Support = -> [Binder017]
  SyncPlacement = true
  TreeRank = 658
FEATURE [PartDesign::Pad] Pad048
  AddSubType = 0
  AlongSketchNormal = false
  CheckUpToFaceLimits = true
  ClaimChildren = false
  Direction = (0,0,1)
  Fit = 0
  FitJoin = 0
  InnerFit = 0
  InnerFitJoin = 0
  InnerTaperAngle = 0
  InnerTaperAngleRev = 0
  Length = 10
  Length2 = 100
  Linearize = true
  NewSolid = false
  Profile = -> Export055
  Refine = true
  Suppress = false
  TreeRank = 660
  Type = 0
  _ProfileBasedVersion = 1
FEATURE [Sketcher::SketchExport] Export056  label="topshapelineare"
  AttachmentOffset = pos=(0,0,0) rot=(0,0,1;1.5708rad)
  Base = -> Sketch031
  BaseRefs = -> Sketch031 [edge7,edge15,edge11,edge12,edge8,edge9,edge13,edge10]
  MapMode = 5
  Placement = pos=(0,0,-67) rot=(0,0,1;1.5708rad)
  Refs = ;g20.edge7 | ;g29.edge15 | ;g26.edge11 | ;g23.edge12 | ;g21.edge8 | ;g22.edge9 | ;g27.edge13 | ;g25.edge10
  Support = -> [Binder017]
  SyncPlacement = true
  TreeRank = 661
FEATURE [PartDesign::Pad] Pad049
  AddSubType = 0
  AlongSketchNormal = false
  BaseFeature = -> Pad048
  CheckUpToFaceLimits = true
  ClaimChildren = false
  Direction = (0,0,1)
  Fit = 0
  FitJoin = 0
  InnerFit = 0
  InnerFitJoin = 0
  InnerTaperAngle = 0
  InnerTaperAngleRev = 0
  Length = 40
  Length2 = 100
  Linearize = true
  NewSolid = false
  Profile = -> Export056
  Refine = true
  Suppress = false
  TreeRank = 662
  Type = 0
  _ProfileBasedVersion = 1
FEATURE [PartDesign::Fillet] Fillet025
  AddSubType = 0
  Base = -> Pad049 [Edge32,Edge4]
  BaseFeature = -> Pad049
  NewSolid = false
  Radius = 2
  Refine = true
  SupportTransform = false
  Suppress = false
  TreeRank = 663
